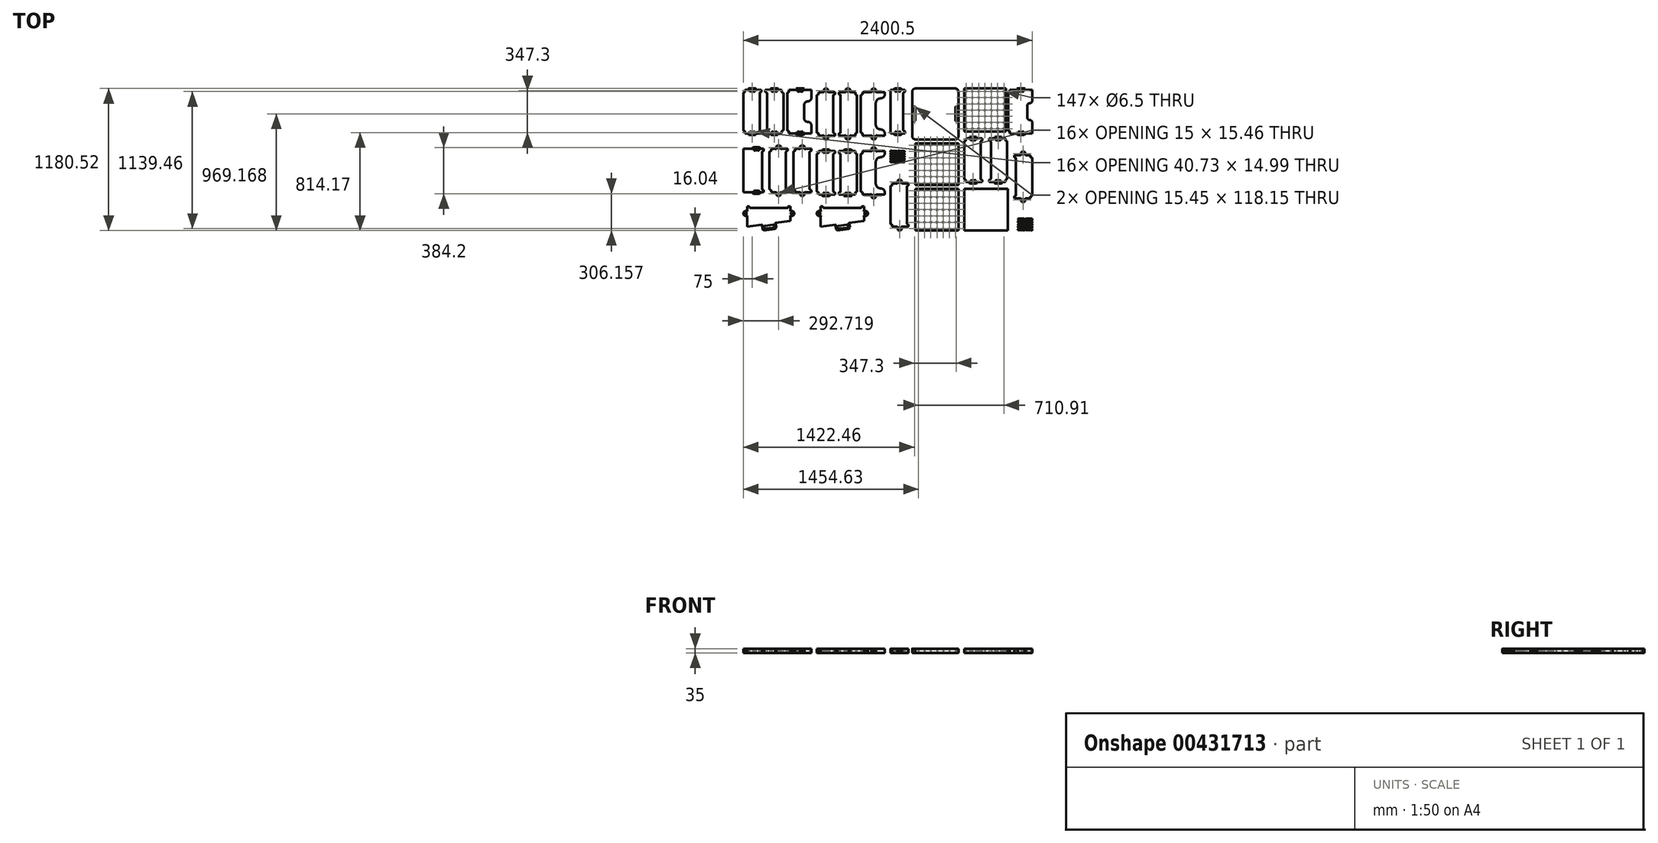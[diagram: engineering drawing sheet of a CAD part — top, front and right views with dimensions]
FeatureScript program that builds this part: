
annotation { "Feature Type Name" : "Feature", "Feature Type Description" : "" }
export const myFeature = defineFeature(function(context is Context, id is Id, definition is map)
    precondition{}
    {
        {
            var Q0;
            Q0=qCreatedBy(makeId("Top.planeOp"),FACE);
            var sketch = newSketch(context, id + "F0", { "sketchPlane" : qUnion([Q0])});
            skArc(sketch, "E0", {"start": v(1194.81, -507.13) * mm, "mid": v(1198.63, -505.83) * mm, "end": v(1200.25, -502.15) * mm});
            skLineSegment(sketch, "E1", {"start": v(1195.25, -492.72) * mm, "end": v(1150.25, -492.72) * mm});
            skArc(sketch, "E2", {"start": v(1150.25, -492.72) * mm, "mid": v(1145, -497.73) * mm, "end": v(1149.8, -503.19) * mm});
            skArc(sketch, "E3", {"start": v(1200.25, -497.72) * mm, "mid": v(1198.79, -494.18) * mm, "end": v(1195.25, -492.72) * mm});
            skLineSegment(sketch, "E4", {"start": v(1200.25, -502.15) * mm, "end": v(1200.25, -497.72) * mm});
            skLineSegment(sketch, "E5", {"start": v(1149.8, -503.19) * mm, "end": v(1194.81, -507.13) * mm});
            skArc(sketch, "E6", {"start": v(1136.95, -580.84) * mm, "mid": v(1135.49, -577.3) * mm, "end": v(1131.95, -575.84) * mm});
            skLineSegment(sketch, "E7", {"start": v(1131.95, -575.84) * mm, "end": v(1086.95, -575.84) * mm});
            skArc(sketch, "E8", {"start": v(1086.95, -575.84) * mm, "mid": v(1081.7, -580.86) * mm, "end": v(1086.5, -586.31) * mm});
            skLineSegment(sketch, "E9", {"start": v(1136.95, -585.27) * mm, "end": v(1136.95, -580.84) * mm});
            skArc(sketch, "E10", {"start": v(1131.52, -590.25) * mm, "mid": v(1135.33, -588.96) * mm, "end": v(1136.95, -585.27) * mm});
            skLineSegment(sketch, "E11", {"start": v(1086.5, -586.31) * mm, "end": v(1131.52, -590.25) * mm});
            skArc(sketch, "E12", {"start": v(91.86, -8.3) * mm, "mid": v(88.05, -9.6) * mm, "end": v(86.42, -13.28) * mm});
            skLineSegment(sketch, "E13", {"start": v(136.88, -12.24) * mm, "end": v(91.86, -8.3) * mm});
            skLineSegment(sketch, "E14", {"start": v(91.42, -22.71) * mm, "end": v(136.42, -22.71) * mm});
            skArc(sketch, "E15", {"start": v(136.42, -22.71) * mm, "mid": v(141.67, -17.7) * mm, "end": v(136.88, -12.24) * mm});
            skArc(sketch, "E16", {"start": v(86.42, -17.71) * mm, "mid": v(87.89, -21.25) * mm, "end": v(91.42, -22.71) * mm});
            skLineSegment(sketch, "E17", {"start": v(86.42, -13.28) * mm, "end": v(86.42, -17.71) * mm});
            skLineSegment(sketch, "E18", {"start": v(28.12, -22.71) * mm, "end": v(73.12, -22.71) * mm});
            skArc(sketch, "E19", {"start": v(28.56, -8.3) * mm, "mid": v(24.75, -9.6) * mm, "end": v(23.12, -13.28) * mm});
            skArc(sketch, "E20", {"start": v(23.12, -17.71) * mm, "mid": v(24.59, -21.25) * mm, "end": v(28.12, -22.71) * mm});
            skLineSegment(sketch, "E21", {"start": v(73.58, -12.24) * mm, "end": v(28.56, -8.3) * mm});
            skArc(sketch, "E22", {"start": v(73.12, -22.71) * mm, "mid": v(78.37, -17.7) * mm, "end": v(73.58, -12.24) * mm});
            skLineSegment(sketch, "E23", {"start": v(23.12, -13.28) * mm, "end": v(23.12, -17.71) * mm});
            skLineSegment(sketch, "E24", {"start": v(73.58, 8.54) * mm, "end": v(28.56, 12.48) * mm});
            skArc(sketch, "E25", {"start": v(28.56, 12.48) * mm, "mid": v(24.75, 11.19) * mm, "end": v(23.12, 7.5) * mm});
            skArc(sketch, "E26", {"start": v(73.12, -1.93) * mm, "mid": v(78.37, 3.09) * mm, "end": v(73.58, 8.54) * mm});
            skArc(sketch, "E27", {"start": v(23.12, 3.07) * mm, "mid": v(24.59, -0.47) * mm, "end": v(28.12, -1.93) * mm});
            skLineSegment(sketch, "E28", {"start": v(28.12, -1.93) * mm, "end": v(73.12, -1.93) * mm});
            skLineSegment(sketch, "E29", {"start": v(23.12, 7.5) * mm, "end": v(23.12, 3.07) * mm});
            skArc(sketch, "E30", {"start": v(91.86, 12.48) * mm, "mid": v(88.05, 11.19) * mm, "end": v(86.42, 7.5) * mm});
            skLineSegment(sketch, "E31", {"start": v(136.88, 8.54) * mm, "end": v(91.86, 12.48) * mm});
            skArc(sketch, "E32", {"start": v(136.42, -1.93) * mm, "mid": v(141.67, 3.09) * mm, "end": v(136.88, 8.54) * mm});
            skArc(sketch, "E33", {"start": v(86.42, 3.07) * mm, "mid": v(87.89, -0.47) * mm, "end": v(91.42, -1.93) * mm});
            skLineSegment(sketch, "E34", {"start": v(91.42, -1.93) * mm, "end": v(136.42, -1.93) * mm});
            skLineSegment(sketch, "E35", {"start": v(86.42, 7.5) * mm, "end": v(86.42, 3.07) * mm});
            skArc(sketch, "E36", {"start": v(136.42, 18.85) * mm, "mid": v(141.67, 23.87) * mm, "end": v(136.88, 29.32) * mm});
            skLineSegment(sketch, "E37", {"start": v(136.88, 29.32) * mm, "end": v(91.86, 33.26) * mm});
            skArc(sketch, "E38", {"start": v(91.86, 33.26) * mm, "mid": v(88.05, 31.97) * mm, "end": v(86.42, 28.28) * mm});
            skArc(sketch, "E39", {"start": v(86.42, 23.85) * mm, "mid": v(87.89, 20.31) * mm, "end": v(91.42, 18.85) * mm});
            skLineSegment(sketch, "E40", {"start": v(91.42, 18.85) * mm, "end": v(136.42, 18.85) * mm});
            skLineSegment(sketch, "E41", {"start": v(86.42, 28.28) * mm, "end": v(86.42, 23.85) * mm});
            skArc(sketch, "E42", {"start": v(28.56, 33.26) * mm, "mid": v(24.75, 31.97) * mm, "end": v(23.12, 28.28) * mm});
            skLineSegment(sketch, "E43", {"start": v(73.58, 29.32) * mm, "end": v(28.56, 33.26) * mm});
            skArc(sketch, "E44", {"start": v(73.12, 18.85) * mm, "mid": v(78.37, 23.87) * mm, "end": v(73.58, 29.32) * mm});
            skArc(sketch, "E45", {"start": v(23.12, 23.85) * mm, "mid": v(24.59, 20.31) * mm, "end": v(28.12, 18.85) * mm});
            skLineSegment(sketch, "E46", {"start": v(28.12, 18.85) * mm, "end": v(73.12, 18.85) * mm});
            skLineSegment(sketch, "E47", {"start": v(23.12, 28.28) * mm, "end": v(23.12, 23.85) * mm});
            skArc(sketch, "E48", {"start": v(23.12, 44.63) * mm, "mid": v(24.59, 41.1) * mm, "end": v(28.12, 39.63) * mm});
            skArc(sketch, "E49", {"start": v(28.56, 54.04) * mm, "mid": v(24.75, 52.75) * mm, "end": v(23.12, 49.06) * mm});
            skArc(sketch, "E50", {"start": v(73.12, 39.63) * mm, "mid": v(78.37, 44.65) * mm, "end": v(73.58, 50.1) * mm});
            skLineSegment(sketch, "E51", {"start": v(73.58, 50.1) * mm, "end": v(28.56, 54.04) * mm});
            skLineSegment(sketch, "E52", {"start": v(28.12, 39.63) * mm, "end": v(73.12, 39.63) * mm});
            skLineSegment(sketch, "E53", {"start": v(23.12, 49.06) * mm, "end": v(23.12, 44.63) * mm});
            skLineSegment(sketch, "E54", {"start": v(91.42, 39.63) * mm, "end": v(136.42, 39.63) * mm});
            skArc(sketch, "E55", {"start": v(91.86, 54.04) * mm, "mid": v(88.05, 52.75) * mm, "end": v(86.42, 49.06) * mm});
            skLineSegment(sketch, "E56", {"start": v(136.88, 50.1) * mm, "end": v(91.86, 54.04) * mm});
            skArc(sketch, "E57", {"start": v(136.42, 39.63) * mm, "mid": v(141.67, 44.65) * mm, "end": v(136.88, 50.1) * mm});
            skArc(sketch, "E58", {"start": v(86.42, 44.63) * mm, "mid": v(87.89, 41.1) * mm, "end": v(91.42, 39.63) * mm});
            skLineSegment(sketch, "E59", {"start": v(86.42, 49.06) * mm, "end": v(86.42, 44.63) * mm});
            skArc(sketch, "E60", {"start": v(136.42, 60.41) * mm, "mid": v(141.67, 65.43) * mm, "end": v(136.88, 70.88) * mm});
            skArc(sketch, "E61", {"start": v(91.86, 74.82) * mm, "mid": v(88.05, 73.53) * mm, "end": v(86.42, 69.84) * mm});
            skLineSegment(sketch, "E62", {"start": v(136.88, 70.88) * mm, "end": v(91.86, 74.82) * mm});
            skArc(sketch, "E63", {"start": v(86.42, 65.41) * mm, "mid": v(87.89, 61.88) * mm, "end": v(91.42, 60.41) * mm});
            skLineSegment(sketch, "E64", {"start": v(91.42, 60.41) * mm, "end": v(136.42, 60.41) * mm});
            skLineSegment(sketch, "E65", {"start": v(86.42, 69.84) * mm, "end": v(86.42, 65.41) * mm});
            skArc(sketch, "E66", {"start": v(28.56, 74.82) * mm, "mid": v(24.75, 73.53) * mm, "end": v(23.12, 69.84) * mm});
            skLineSegment(sketch, "E67", {"start": v(73.58, 70.88) * mm, "end": v(28.56, 74.82) * mm});
            skArc(sketch, "E68", {"start": v(73.12, 60.41) * mm, "mid": v(78.37, 65.43) * mm, "end": v(73.58, 70.88) * mm});
            skLineSegment(sketch, "E69", {"start": v(28.12, 60.41) * mm, "end": v(73.12, 60.41) * mm});
            skArc(sketch, "E70", {"start": v(23.12, 65.41) * mm, "mid": v(24.59, 61.88) * mm, "end": v(28.12, 60.41) * mm});
            skLineSegment(sketch, "E71", {"start": v(23.12, 69.84) * mm, "end": v(23.12, 65.41) * mm});
            skArc(sketch, "E72", {"start": v(1194.81, -527.9) * mm, "mid": v(1198.63, -526.61) * mm, "end": v(1200.25, -522.93) * mm});
            skLineSegment(sketch, "E73", {"start": v(1149.8, -523.97) * mm, "end": v(1194.81, -527.9) * mm});
            skArc(sketch, "E74", {"start": v(1150.25, -513.5) * mm, "mid": v(1145, -518.51) * mm, "end": v(1149.8, -523.97) * mm});
            skLineSegment(sketch, "E75", {"start": v(1195.25, -513.5) * mm, "end": v(1150.25, -513.5) * mm});
            skArc(sketch, "E76", {"start": v(1200.25, -518.5) * mm, "mid": v(1198.79, -514.96) * mm, "end": v(1195.25, -513.5) * mm});
            skLineSegment(sketch, "E77", {"start": v(1200.25, -522.93) * mm, "end": v(1200.25, -518.5) * mm});
            skArc(sketch, "E78", {"start": v(1150.25, -534.28) * mm, "mid": v(1145, -539.3) * mm, "end": v(1149.8, -544.75) * mm});
            skArc(sketch, "E79", {"start": v(1194.81, -548.69) * mm, "mid": v(1198.63, -547.4) * mm, "end": v(1200.25, -543.7) * mm});
            skLineSegment(sketch, "E80", {"start": v(1149.8, -544.75) * mm, "end": v(1194.81, -548.69) * mm});
            skLineSegment(sketch, "E81", {"start": v(1195.25, -534.28) * mm, "end": v(1150.25, -534.28) * mm});
            skArc(sketch, "E82", {"start": v(1200.25, -539.28) * mm, "mid": v(1198.79, -535.74) * mm, "end": v(1195.25, -534.28) * mm});
            skLineSegment(sketch, "E83", {"start": v(1200.25, -543.7) * mm, "end": v(1200.25, -539.28) * mm});
            skArc(sketch, "E84", {"start": v(1194.81, -569.47) * mm, "mid": v(1198.63, -568.17) * mm, "end": v(1200.25, -564.49) * mm});
            skLineSegment(sketch, "E85", {"start": v(1149.8, -565.53) * mm, "end": v(1194.81, -569.47) * mm});
            skArc(sketch, "E86", {"start": v(1150.25, -555.06) * mm, "mid": v(1145, -560.08) * mm, "end": v(1149.8, -565.53) * mm});
            skLineSegment(sketch, "E87", {"start": v(1195.25, -555.06) * mm, "end": v(1150.25, -555.06) * mm});
            skArc(sketch, "E88", {"start": v(1200.25, -560.06) * mm, "mid": v(1198.79, -556.52) * mm, "end": v(1195.25, -555.06) * mm});
            skLineSegment(sketch, "E89", {"start": v(1200.25, -564.49) * mm, "end": v(1200.25, -560.06) * mm});
            skArc(sketch, "E90", {"start": v(1150.25, -575.84) * mm, "mid": v(1145, -580.86) * mm, "end": v(1149.8, -586.31) * mm});
            skArc(sketch, "E91", {"start": v(1194.81, -590.25) * mm, "mid": v(1198.63, -588.96) * mm, "end": v(1200.25, -585.27) * mm});
            skLineSegment(sketch, "E92", {"start": v(1149.8, -586.31) * mm, "end": v(1194.81, -590.25) * mm});
            skLineSegment(sketch, "E93", {"start": v(1195.25, -575.84) * mm, "end": v(1150.25, -575.84) * mm});
            skArc(sketch, "E94", {"start": v(1200.25, -580.84) * mm, "mid": v(1198.79, -577.3) * mm, "end": v(1195.25, -575.84) * mm});
            skLineSegment(sketch, "E95", {"start": v(1200.25, -585.27) * mm, "end": v(1200.25, -580.84) * mm});
            skArc(sketch, "E96", {"start": v(1131.52, -569.47) * mm, "mid": v(1135.33, -568.17) * mm, "end": v(1136.95, -564.49) * mm});
            skLineSegment(sketch, "E97", {"start": v(1086.5, -565.53) * mm, "end": v(1131.52, -569.47) * mm});
            skLineSegment(sketch, "E98", {"start": v(1131.95, -555.06) * mm, "end": v(1086.95, -555.06) * mm});
            skArc(sketch, "E99", {"start": v(1086.95, -555.06) * mm, "mid": v(1081.7, -560.08) * mm, "end": v(1086.5, -565.53) * mm});
            skArc(sketch, "E100", {"start": v(1136.95, -560.06) * mm, "mid": v(1135.49, -556.52) * mm, "end": v(1131.95, -555.06) * mm});
            skLineSegment(sketch, "E101", {"start": v(1136.95, -564.49) * mm, "end": v(1136.95, -560.06) * mm});
            skArc(sketch, "E102", {"start": v(1131.52, -548.69) * mm, "mid": v(1135.33, -547.4) * mm, "end": v(1136.95, -543.7) * mm});
            skLineSegment(sketch, "E103", {"start": v(1086.5, -544.75) * mm, "end": v(1131.52, -548.69) * mm});
            skArc(sketch, "E104", {"start": v(1086.95, -534.28) * mm, "mid": v(1081.7, -539.3) * mm, "end": v(1086.5, -544.75) * mm});
            skLineSegment(sketch, "E105", {"start": v(1131.95, -534.28) * mm, "end": v(1086.95, -534.28) * mm});
            skArc(sketch, "E106", {"start": v(1136.95, -539.28) * mm, "mid": v(1135.49, -535.74) * mm, "end": v(1131.95, -534.28) * mm});
            skLineSegment(sketch, "E107", {"start": v(1136.95, -543.7) * mm, "end": v(1136.95, -539.28) * mm});
            skArc(sketch, "E108", {"start": v(1131.52, -527.9) * mm, "mid": v(1135.33, -526.61) * mm, "end": v(1136.95, -522.93) * mm});
            skLineSegment(sketch, "E109", {"start": v(1086.5, -523.97) * mm, "end": v(1131.52, -527.9) * mm});
            skArc(sketch, "E110", {"start": v(1086.95, -513.5) * mm, "mid": v(1081.7, -518.51) * mm, "end": v(1086.5, -523.97) * mm});
            skArc(sketch, "E111", {"start": v(1136.95, -518.5) * mm, "mid": v(1135.49, -514.96) * mm, "end": v(1131.95, -513.5) * mm});
            skLineSegment(sketch, "E112", {"start": v(1131.95, -513.5) * mm, "end": v(1086.95, -513.5) * mm});
            skLineSegment(sketch, "E113", {"start": v(1136.95, -522.93) * mm, "end": v(1136.95, -518.5) * mm});
            skLineSegment(sketch, "E114", {"start": v(1131.95, -492.72) * mm, "end": v(1086.95, -492.72) * mm});
            skArc(sketch, "E115", {"start": v(1131.52, -507.13) * mm, "mid": v(1135.33, -505.83) * mm, "end": v(1136.95, -502.15) * mm});
            skLineSegment(sketch, "E116", {"start": v(1086.5, -503.19) * mm, "end": v(1131.52, -507.13) * mm});
            skArc(sketch, "E117", {"start": v(1086.95, -492.72) * mm, "mid": v(1081.7, -497.73) * mm, "end": v(1086.5, -503.19) * mm});
            skArc(sketch, "E118", {"start": v(1136.95, -497.72) * mm, "mid": v(1135.49, -494.18) * mm, "end": v(1131.95, -492.72) * mm});
            skLineSegment(sketch, "E119", {"start": v(1136.95, -502.15) * mm, "end": v(1136.95, -497.72) * mm});
            skCircle(sketch, "E120", {"center": v(860.47, 462.18) * mm, "radius": 3.25 * mm});
            skCircle(sketch, "E121", {"center": v(860.47, 565.23) * mm, "radius": 3.25 * mm});
            skLineSegment(sketch, "E122", {"start": v(634.81, 231.05) * mm, "end": v(981.31, 231.05) * mm});
            skCircle(sketch, "E123", {"center": v(965.3, 462.18) * mm, "radius": 3.25 * mm});
            skCircle(sketch, "E124", {"center": v(965.3, 410.65) * mm, "radius": 3.25 * mm});
            skCircle(sketch, "E125", {"center": v(965.3, 513.7) * mm, "radius": 3.25 * mm});
            skCircle(sketch, "E126", {"center": v(965.3, 307.6) * mm, "radius": 3.25 * mm});
            skCircle(sketch, "E127", {"center": v(912.88, 462.18) * mm, "radius": 3.25 * mm});
            skCircle(sketch, "E128", {"center": v(860.47, 513.7) * mm, "radius": 3.25 * mm});
            skCircle(sketch, "E129", {"center": v(912.88, 513.7) * mm, "radius": 3.25 * mm});
            skCircle(sketch, "E130", {"center": v(912.88, 565.23) * mm, "radius": 3.25 * mm});
            skCircle(sketch, "E131", {"center": v(965.3, 565.23) * mm, "radius": 3.25 * mm});
            skCircle(sketch, "E132", {"center": v(965.3, 359.12) * mm, "radius": 3.25 * mm});
            skCircle(sketch, "E133", {"center": v(860.47, 410.65) * mm, "radius": 3.25 * mm});
            skCircle(sketch, "E134", {"center": v(912.88, 410.65) * mm, "radius": 3.25 * mm});
            skCircle(sketch, "E135", {"center": v(860.47, 359.12) * mm, "radius": 3.25 * mm});
            skCircle(sketch, "E136", {"center": v(912.88, 359.12) * mm, "radius": 3.25 * mm});
            skCircle(sketch, "E137", {"center": v(755.65, 462.18) * mm, "radius": 3.25 * mm});
            skCircle(sketch, "E138", {"center": v(860.47, 307.6) * mm, "radius": 3.25 * mm});
            skCircle(sketch, "E139", {"center": v(912.88, 307.6) * mm, "radius": 3.25 * mm});
            skCircle(sketch, "E140", {"center": v(860.47, 256.07) * mm, "radius": 3.25 * mm});
            skCircle(sketch, "E141", {"center": v(912.88, 256.07) * mm, "radius": 3.25 * mm});
            skCircle(sketch, "E142", {"center": v(965.3, 256.07) * mm, "radius": 3.25 * mm});
            skCircle(sketch, "E143", {"center": v(755.65, 513.7) * mm, "radius": 3.25 * mm});
            skCircle(sketch, "E144", {"center": v(650.83, 462.18) * mm, "radius": 3.25 * mm});
            skCircle(sketch, "E145", {"center": v(650.83, 513.7) * mm, "radius": 3.25 * mm});
            skCircle(sketch, "E146", {"center": v(808.06, 462.18) * mm, "radius": 3.25 * mm});
            skCircle(sketch, "E147", {"center": v(755.65, 359.12) * mm, "radius": 3.25 * mm});
            skCircle(sketch, "E148", {"center": v(703.24, 462.18) * mm, "radius": 3.25 * mm});
            skCircle(sketch, "E149", {"center": v(808.06, 513.7) * mm, "radius": 3.25 * mm});
            skCircle(sketch, "E150", {"center": v(703.24, 513.7) * mm, "radius": 3.25 * mm});
            skCircle(sketch, "E151", {"center": v(808.06, 565.23) * mm, "radius": 3.25 * mm});
            skCircle(sketch, "E152", {"center": v(755.65, 565.23) * mm, "radius": 3.25 * mm});
            skCircle(sketch, "E153", {"center": v(703.24, 565.23) * mm, "radius": 3.25 * mm});
            skCircle(sketch, "E154", {"center": v(703.24, 359.12) * mm, "radius": 3.25 * mm});
            skCircle(sketch, "E155", {"center": v(650.83, 565.23) * mm, "radius": 3.25 * mm});
            skCircle(sketch, "E156", {"center": v(650.83, 410.65) * mm, "radius": 3.25 * mm});
            skCircle(sketch, "E157", {"center": v(650.83, 359.12) * mm, "radius": 3.25 * mm});
            skCircle(sketch, "E158", {"center": v(650.83, 307.6) * mm, "radius": 3.25 * mm});
            skCircle(sketch, "E159", {"center": v(808.06, 410.65) * mm, "radius": 3.25 * mm});
            skCircle(sketch, "E160", {"center": v(755.65, 410.65) * mm, "radius": 3.25 * mm});
            skCircle(sketch, "E161", {"center": v(703.24, 410.65) * mm, "radius": 3.25 * mm});
            skCircle(sketch, "E162", {"center": v(808.06, 359.12) * mm, "radius": 3.25 * mm});
            skCircle(sketch, "E163", {"center": v(808.06, 307.6) * mm, "radius": 3.25 * mm});
            skLineSegment(sketch, "E164", {"start": v(634.81, 590.25) * mm, "end": v(981.31, 590.25) * mm});
            skCircle(sketch, "E165", {"center": v(755.65, 307.6) * mm, "radius": 3.25 * mm});
            skCircle(sketch, "E166", {"center": v(703.24, 307.6) * mm, "radius": 3.25 * mm});
            skCircle(sketch, "E167", {"center": v(808.06, 256.07) * mm, "radius": 3.25 * mm});
            skCircle(sketch, "E168", {"center": v(755.65, 256.07) * mm, "radius": 3.25 * mm});
            skCircle(sketch, "E169", {"center": v(703.24, 256.07) * mm, "radius": 3.25 * mm});
            skCircle(sketch, "E170", {"center": v(650.83, 256.07) * mm, "radius": 3.25 * mm});
            skLineSegment(sketch, "E171", {"start": v(634.81, 590.25) * mm, "end": v(634.81, 231.05) * mm});
            skLineSegment(sketch, "E172", {"start": v(981.31, 590.25) * mm, "end": v(981.31, 231.05) * mm});
            skArc(sketch, "E173", {"start": v(1092.97, 217.38) * mm, "mid": v(1092.64, 217.32) * mm, "end": v(1092.34, 217.15) * mm});
            skArc(sketch, "E174", {"start": v(1087.86, 572.6) * mm, "mid": v(1087.8, 572.94) * mm, "end": v(1087.63, 573.24) * mm});
            skArc(sketch, "E175", {"start": v(1122.16, 564.45) * mm, "mid": v(1126.64, 564.68) * mm, "end": v(1126.87, 569.16) * mm});
            skLineSegment(sketch, "E176", {"start": v(1014.25, 564.45) * mm, "end": v(1014.25, 577.55) * mm});
            skArc(sketch, "E177", {"start": v(1087.63, 569.16) * mm, "mid": v(1087.8, 569.46) * mm, "end": v(1087.86, 569.8) * mm});
            skLineSegment(sketch, "E178", {"start": v(1087.86, 569.8) * mm, "end": v(1087.86, 572.6) * mm});
            skArc(sketch, "E179", {"start": v(1087.63, 569.16) * mm, "mid": v(1087.86, 564.68) * mm, "end": v(1092.34, 564.45) * mm});
            skArc(sketch, "E180", {"start": v(1092.97, 564.68) * mm, "mid": v(1092.64, 564.62) * mm, "end": v(1092.34, 564.45) * mm});
            skArc(sketch, "E181", {"start": v(1200.25, 307.55) * mm, "mid": v(1194.4, 321.7) * mm, "end": v(1180.25, 327.55) * mm});
            skArc(sketch, "E182", {"start": v(1122.16, 564.45) * mm, "mid": v(1121.86, 564.62) * mm, "end": v(1121.53, 564.68) * mm});
            skLineSegment(sketch, "E183", {"start": v(1121.53, 564.68) * mm, "end": v(1092.97, 564.68) * mm});
            skArc(sketch, "E184", {"start": v(1126.64, 569.8) * mm, "mid": v(1126.7, 569.46) * mm, "end": v(1126.87, 569.16) * mm});
            skLineSegment(sketch, "E185", {"start": v(1126.64, 572.6) * mm, "end": v(1126.64, 569.8) * mm});
            skArc(sketch, "E186", {"start": v(1126.87, 573.24) * mm, "mid": v(1126.7, 572.94) * mm, "end": v(1126.64, 572.6) * mm});
            skArc(sketch, "E187", {"start": v(1126.87, 573.24) * mm, "mid": v(1126.64, 577.72) * mm, "end": v(1122.16, 577.95) * mm});
            skArc(sketch, "E188", {"start": v(1121.53, 577.72) * mm, "mid": v(1121.86, 577.78) * mm, "end": v(1122.16, 577.95) * mm});
            skArc(sketch, "E189", {"start": v(1075.16, 582.66) * mm, "mid": v(1075.22, 582.33) * mm, "end": v(1075.39, 582.03) * mm});
            skLineSegment(sketch, "E190", {"start": v(1092.97, 577.72) * mm, "end": v(1121.53, 577.72) * mm});
            skArc(sketch, "E191", {"start": v(1092.34, 577.95) * mm, "mid": v(1092.64, 577.78) * mm, "end": v(1092.97, 577.72) * mm});
            skArc(sketch, "E192", {"start": v(1092.34, 577.95) * mm, "mid": v(1087.86, 577.72) * mm, "end": v(1087.63, 573.24) * mm});
            skLineSegment(sketch, "E193", {"start": v(1014.25, 577.55) * mm, "end": v(1070.05, 577.55) * mm});
            skArc(sketch, "E194", {"start": v(1070.68, 577.32) * mm, "mid": v(1070.38, 577.5) * mm, "end": v(1070.05, 577.55) * mm});
            skArc(sketch, "E195", {"start": v(1070.68, 577.32) * mm, "mid": v(1075.16, 577.55) * mm, "end": v(1075.39, 582.03) * mm});
            skArc(sketch, "E196", {"start": v(1180.25, 467.55) * mm, "mid": v(1194.4, 473.4) * mm, "end": v(1200.25, 487.55) * mm});
            skLineSegment(sketch, "E197", {"start": v(1075.16, 582.66) * mm, "end": v(1075.16, 586.46) * mm});
            skLineSegment(sketch, "E198", {"start": v(1075.16, 586.46) * mm, "end": v(1078.95, 590.25) * mm});
            skArc(sketch, "E199", {"start": v(1180.25, 467.55) * mm, "mid": v(1166.1, 461.7) * mm, "end": v(1160.25, 447.55) * mm});
            skLineSegment(sketch, "E200", {"start": v(1078.95, 590.25) * mm, "end": v(1135.55, 590.25) * mm});
            skLineSegment(sketch, "E201", {"start": v(1135.55, 590.25) * mm, "end": v(1139.34, 586.46) * mm});
            skLineSegment(sketch, "E202", {"start": v(1139.34, 586.46) * mm, "end": v(1139.34, 582.66) * mm});
            skArc(sketch, "E203", {"start": v(1139.11, 582.03) * mm, "mid": v(1139.28, 582.33) * mm, "end": v(1139.34, 582.66) * mm});
            skArc(sketch, "E204", {"start": v(1139.11, 582.03) * mm, "mid": v(1139.34, 577.55) * mm, "end": v(1143.82, 577.32) * mm});
            skArc(sketch, "E205", {"start": v(1144.45, 577.55) * mm, "mid": v(1144.12, 577.5) * mm, "end": v(1143.82, 577.32) * mm});
            skLineSegment(sketch, "E206", {"start": v(1144.45, 577.55) * mm, "end": v(1200.25, 577.55) * mm});
            skArc(sketch, "E207", {"start": v(1143.82, 217.78) * mm, "mid": v(1144.12, 217.6) * mm, "end": v(1144.45, 217.55) * mm});
            skLineSegment(sketch, "E208", {"start": v(1200.25, 577.55) * mm, "end": v(1200.25, 487.55) * mm});
            skLineSegment(sketch, "E209", {"start": v(1160.25, 347.55) * mm, "end": v(1160.25, 447.55) * mm});
            skArc(sketch, "E210", {"start": v(1160.25, 347.55) * mm, "mid": v(1166.1, 333.4) * mm, "end": v(1180.25, 327.55) * mm});
            skLineSegment(sketch, "E211", {"start": v(1200.25, 217.55) * mm, "end": v(1200.25, 307.55) * mm});
            skLineSegment(sketch, "E212", {"start": v(1144.45, 217.55) * mm, "end": v(1200.25, 217.55) * mm});
            skArc(sketch, "E213", {"start": v(1143.82, 217.78) * mm, "mid": v(1139.34, 217.55) * mm, "end": v(1139.11, 213.07) * mm});
            skLineSegment(sketch, "E214", {"start": v(1139.34, 208.64) * mm, "end": v(1139.34, 212.44) * mm});
            skArc(sketch, "E215", {"start": v(1139.34, 212.44) * mm, "mid": v(1139.28, 212.77) * mm, "end": v(1139.11, 213.07) * mm});
            skLineSegment(sketch, "E216", {"start": v(1135.55, 204.85) * mm, "end": v(1139.34, 208.64) * mm});
            skLineSegment(sketch, "E217", {"start": v(1078.95, 204.85) * mm, "end": v(1135.55, 204.85) * mm});
            skLineSegment(sketch, "E218", {"start": v(1075.16, 208.64) * mm, "end": v(1078.95, 204.85) * mm});
            skLineSegment(sketch, "E219", {"start": v(1075.16, 212.44) * mm, "end": v(1075.16, 208.64) * mm});
            skArc(sketch, "E220", {"start": v(1075.39, 213.07) * mm, "mid": v(1075.22, 212.77) * mm, "end": v(1075.16, 212.44) * mm});
            skArc(sketch, "E221", {"start": v(1075.39, 213.07) * mm, "mid": v(1075.16, 217.55) * mm, "end": v(1070.68, 217.78) * mm});
            skArc(sketch, "E222", {"start": v(1070.05, 217.55) * mm, "mid": v(1070.38, 217.6) * mm, "end": v(1070.68, 217.78) * mm});
            skLineSegment(sketch, "E223", {"start": v(1014.25, 217.55) * mm, "end": v(1070.05, 217.55) * mm});
            skLineSegment(sketch, "E224", {"start": v(1014.25, 230.65) * mm, "end": v(1014.25, 217.55) * mm});
            skArc(sketch, "E225", {"start": v(1014.25, 230.65) * mm, "mid": v(1012.2, 235.6) * mm, "end": v(1007.25, 237.65) * mm});
            skArc(sketch, "E226", {"start": v(1000.25, 244.65) * mm, "mid": v(1002.3, 239.7) * mm, "end": v(1007.25, 237.65) * mm});
            skLineSegment(sketch, "E227", {"start": v(1000.25, 550.45) * mm, "end": v(1000.25, 244.65) * mm});
            skLineSegment(sketch, "E228", {"start": v(1126.64, 222.5) * mm, "end": v(1126.64, 225.3) * mm});
            skArc(sketch, "E229", {"start": v(1007.25, 557.45) * mm, "mid": v(1002.3, 555.4) * mm, "end": v(1000.25, 550.45) * mm});
            skArc(sketch, "E230", {"start": v(1087.86, 225.3) * mm, "mid": v(1087.8, 225.64) * mm, "end": v(1087.63, 225.94) * mm});
            skArc(sketch, "E231", {"start": v(1007.25, 557.45) * mm, "mid": v(1012.2, 559.5) * mm, "end": v(1014.25, 564.45) * mm});
            skArc(sketch, "E232", {"start": v(1122.16, 217.15) * mm, "mid": v(1121.86, 217.32) * mm, "end": v(1121.53, 217.38) * mm});
            skLineSegment(sketch, "E233", {"start": v(1092.97, 217.38) * mm, "end": v(1121.53, 217.38) * mm});
            skArc(sketch, "E234", {"start": v(1122.16, 217.15) * mm, "mid": v(1126.64, 217.38) * mm, "end": v(1126.87, 221.86) * mm});
            skArc(sketch, "E235", {"start": v(1126.64, 222.5) * mm, "mid": v(1126.7, 222.16) * mm, "end": v(1126.87, 221.86) * mm});
            skArc(sketch, "E236", {"start": v(1126.87, 225.94) * mm, "mid": v(1126.7, 225.64) * mm, "end": v(1126.64, 225.3) * mm});
            skArc(sketch, "E237", {"start": v(1126.87, 225.94) * mm, "mid": v(1126.64, 230.42) * mm, "end": v(1122.16, 230.65) * mm});
            skArc(sketch, "E238", {"start": v(1121.53, 230.42) * mm, "mid": v(1121.86, 230.48) * mm, "end": v(1122.16, 230.65) * mm});
            skLineSegment(sketch, "E239", {"start": v(1121.53, 230.42) * mm, "end": v(1092.97, 230.42) * mm});
            skArc(sketch, "E240", {"start": v(1092.34, 230.65) * mm, "mid": v(1092.64, 230.48) * mm, "end": v(1092.97, 230.42) * mm});
            skArc(sketch, "E241", {"start": v(1092.34, 230.65) * mm, "mid": v(1087.86, 230.42) * mm, "end": v(1087.63, 225.94) * mm});
            skArc(sketch, "E242", {"start": v(1087.63, 221.86) * mm, "mid": v(1087.86, 217.38) * mm, "end": v(1092.34, 217.15) * mm});
            skLineSegment(sketch, "E243", {"start": v(1087.86, 225.3) * mm, "end": v(1087.86, 222.5) * mm});
            skArc(sketch, "E244", {"start": v(1087.63, 221.86) * mm, "mid": v(1087.8, 222.16) * mm, "end": v(1087.86, 222.5) * mm});
            skArc(sketch, "E245", {"start": v(1149.1, -323.83) * mm, "mid": v(1144.47, -323.93) * mm, "end": v(1144.37, -328.55) * mm});
            skLineSegment(sketch, "E246", {"start": v(1186.25, -310.83) * mm, "end": v(1186.25, -323.93) * mm});
            skArc(sketch, "E247", {"start": v(1131.77, -337.9) * mm, "mid": v(1131.8, -338.04) * mm, "end": v(1131.87, -338.16) * mm});
            skArc(sketch, "E248", {"start": v(1123.35, 55.02) * mm, "mid": v(1123.48, 54.94) * mm, "end": v(1123.62, 54.92) * mm});
            skArc(sketch, "E249", {"start": v(1149.1, -323.83) * mm, "mid": v(1149.22, -323.9) * mm, "end": v(1149.36, -323.93) * mm});
            skLineSegment(sketch, "E250", {"start": v(1186.25, -323.93) * mm, "end": v(1149.36, -323.93) * mm});
            skArc(sketch, "E251", {"start": v(1106.13, -328.55) * mm, "mid": v(1106.03, -323.93) * mm, "end": v(1101.4, -323.83) * mm});
            skArc(sketch, "E252", {"start": v(1144.47, -328.82) * mm, "mid": v(1144.44, -328.68) * mm, "end": v(1144.37, -328.55) * mm});
            skLineSegment(sketch, "E253", {"start": v(1144.47, -343.24) * mm, "end": v(1132.23, -355.48) * mm});
            skLineSegment(sketch, "E254", {"start": v(1144.47, -328.82) * mm, "end": v(1144.47, -343.24) * mm});
            skLineSegment(sketch, "E255", {"start": v(1132.23, -355.48) * mm, "end": v(1118.27, -355.48) * mm});
            skLineSegment(sketch, "E256", {"start": v(1118.27, -355.48) * mm, "end": v(1106.03, -343.24) * mm});
            skLineSegment(sketch, "E257", {"start": v(1106.03, -343.24) * mm, "end": v(1106.03, -328.82) * mm});
            skArc(sketch, "E258", {"start": v(1106.13, -328.55) * mm, "mid": v(1106.06, -328.68) * mm, "end": v(1106.03, -328.82) * mm});
            skArc(sketch, "E259", {"start": v(1050.25, 23.37) * mm, "mid": v(1052.3, 18.42) * mm, "end": v(1057.25, 16.37) * mm});
            skArc(sketch, "E260", {"start": v(1101.14, -323.93) * mm, "mid": v(1101.28, -323.9) * mm, "end": v(1101.4, -323.83) * mm});
            skLineSegment(sketch, "E261", {"start": v(1101.14, -323.93) * mm, "end": v(1050.25, -323.93) * mm});
            skLineSegment(sketch, "E262", {"start": v(1050.25, -323.93) * mm, "end": v(1050.25, -311.23) * mm});
            skArc(sketch, "E263", {"start": v(1057.25, -304.23) * mm, "mid": v(1052.3, -306.28) * mm, "end": v(1050.25, -311.23) * mm});
            skArc(sketch, "E264", {"start": v(1057.25, -304.23) * mm, "mid": v(1062.2, -302.18) * mm, "end": v(1064.25, -297.23) * mm});
            skArc(sketch, "E265", {"start": v(1101.4, 35.96) * mm, "mid": v(1106.03, 36.07) * mm, "end": v(1106.13, 40.69) * mm});
            skLineSegment(sketch, "E266", {"start": v(1064.25, 9.37) * mm, "end": v(1064.25, -297.23) * mm});
            skArc(sketch, "E267", {"start": v(1064.25, 9.37) * mm, "mid": v(1062.2, 14.32) * mm, "end": v(1057.25, 16.37) * mm});
            skLineSegment(sketch, "E268", {"start": v(1050.25, 36.07) * mm, "end": v(1050.25, 23.37) * mm});
            skArc(sketch, "E269", {"start": v(1101.4, 35.96) * mm, "mid": v(1101.28, 36.04) * mm, "end": v(1101.14, 36.07) * mm});
            skLineSegment(sketch, "E270", {"start": v(1101.14, 36.07) * mm, "end": v(1050.25, 36.07) * mm});
            skArc(sketch, "E271", {"start": v(1106.03, 40.96) * mm, "mid": v(1106.06, 40.81) * mm, "end": v(1106.13, 40.69) * mm});
            skArc(sketch, "E272", {"start": v(1127.15, 41.31) * mm, "mid": v(1127.02, 41.4) * mm, "end": v(1126.88, 41.42) * mm});
            skLineSegment(sketch, "E273", {"start": v(1106.03, 55.38) * mm, "end": v(1106.03, 40.96) * mm});
            skLineSegment(sketch, "E274", {"start": v(1118.27, 67.62) * mm, "end": v(1106.03, 55.38) * mm});
            skLineSegment(sketch, "E275", {"start": v(1132.23, 67.62) * mm, "end": v(1118.27, 67.62) * mm});
            skArc(sketch, "E276", {"start": v(1186.25, 22.97) * mm, "mid": v(1188.3, 18.02) * mm, "end": v(1193.25, 15.97) * mm});
            skLineSegment(sketch, "E277", {"start": v(1144.47, 55.38) * mm, "end": v(1132.23, 67.62) * mm});
            skArc(sketch, "E278", {"start": v(1123.62, 41.42) * mm, "mid": v(1123.48, 41.4) * mm, "end": v(1123.35, 41.31) * mm});
            skLineSegment(sketch, "E279", {"start": v(1144.47, 40.96) * mm, "end": v(1144.47, 55.38) * mm});
            skArc(sketch, "E280", {"start": v(1144.37, 40.69) * mm, "mid": v(1144.44, 40.81) * mm, "end": v(1144.47, 40.96) * mm});
            skArc(sketch, "E281", {"start": v(1144.37, 40.69) * mm, "mid": v(1144.47, 36.07) * mm, "end": v(1149.1, 35.96) * mm});
            skArc(sketch, "E282", {"start": v(1149.36, 36.07) * mm, "mid": v(1149.22, 36.04) * mm, "end": v(1149.1, 35.96) * mm});
            skLineSegment(sketch, "E283", {"start": v(1186.25, 36.07) * mm, "end": v(1149.36, 36.07) * mm});
            skLineSegment(sketch, "E284", {"start": v(1186.25, 22.97) * mm, "end": v(1186.25, 36.07) * mm});
            skArc(sketch, "E285", {"start": v(1200.25, 8.97) * mm, "mid": v(1198.2, 13.92) * mm, "end": v(1193.25, 15.97) * mm});
            skLineSegment(sketch, "E286", {"start": v(1200.25, -296.83) * mm, "end": v(1200.25, 8.97) * mm});
            skArc(sketch, "E287", {"start": v(1193.25, -303.83) * mm, "mid": v(1198.2, -301.78) * mm, "end": v(1200.25, -296.83) * mm});
            skArc(sketch, "E288", {"start": v(1193.25, -303.83) * mm, "mid": v(1188.3, -305.88) * mm, "end": v(1186.25, -310.83) * mm});
            skArc(sketch, "E289", {"start": v(1123.35, 55.02) * mm, "mid": v(1118.73, 54.92) * mm, "end": v(1118.63, 50.3) * mm});
            skArc(sketch, "E290", {"start": v(1118.73, 50.03) * mm, "mid": v(1118.7, 50.17) * mm, "end": v(1118.63, 50.3) * mm});
            skLineSegment(sketch, "E291", {"start": v(1118.73, 50.03) * mm, "end": v(1118.73, 46.3) * mm});
            skArc(sketch, "E292", {"start": v(1118.63, 46.04) * mm, "mid": v(1118.7, 46.16) * mm, "end": v(1118.73, 46.3) * mm});
            skArc(sketch, "E293", {"start": v(1118.63, 46.04) * mm, "mid": v(1118.73, 41.42) * mm, "end": v(1123.35, 41.31) * mm});
            skArc(sketch, "E294", {"start": v(1131.87, 50.3) * mm, "mid": v(1131.8, 50.17) * mm, "end": v(1131.77, 50.03) * mm});
            skLineSegment(sketch, "E295", {"start": v(1123.62, 41.42) * mm, "end": v(1126.88, 41.42) * mm});
            skArc(sketch, "E296", {"start": v(1127.15, 41.31) * mm, "mid": v(1131.77, 41.42) * mm, "end": v(1131.87, 46.04) * mm});
            skArc(sketch, "E297", {"start": v(1131.77, 46.3) * mm, "mid": v(1131.8, 46.16) * mm, "end": v(1131.87, 46.04) * mm});
            skArc(sketch, "E298", {"start": v(1118.73, -334.17) * mm, "mid": v(1118.7, -334.03) * mm, "end": v(1118.63, -333.9) * mm});
            skLineSegment(sketch, "E299", {"start": v(1131.77, 46.3) * mm, "end": v(1131.77, 50.03) * mm});
            skArc(sketch, "E300", {"start": v(1131.87, 50.3) * mm, "mid": v(1131.77, 54.92) * mm, "end": v(1127.15, 55.02) * mm});
            skArc(sketch, "E301", {"start": v(1126.88, 54.92) * mm, "mid": v(1127.02, 54.94) * mm, "end": v(1127.15, 55.02) * mm});
            skArc(sketch, "E302", {"start": v(1123.35, -329.18) * mm, "mid": v(1118.73, -329.28) * mm, "end": v(1118.63, -333.9) * mm});
            skLineSegment(sketch, "E303", {"start": v(1126.88, 54.92) * mm, "end": v(1123.62, 54.92) * mm});
            skLineSegment(sketch, "E304", {"start": v(1131.77, -334.17) * mm, "end": v(1131.77, -337.9) * mm});
            skArc(sketch, "E305", {"start": v(1131.87, -333.9) * mm, "mid": v(1131.8, -334.03) * mm, "end": v(1131.77, -334.17) * mm});
            skArc(sketch, "E306", {"start": v(1131.87, -333.9) * mm, "mid": v(1131.77, -329.28) * mm, "end": v(1127.15, -329.18) * mm});
            skArc(sketch, "E307", {"start": v(1126.88, -329.28) * mm, "mid": v(1127.02, -329.26) * mm, "end": v(1127.15, -329.18) * mm});
            skArc(sketch, "E308", {"start": v(1123.62, -342.78) * mm, "mid": v(1123.48, -342.8) * mm, "end": v(1123.35, -342.89) * mm});
            skLineSegment(sketch, "E309", {"start": v(1123.62, -329.28) * mm, "end": v(1126.88, -329.28) * mm});
            skArc(sketch, "E310", {"start": v(1123.35, -329.18) * mm, "mid": v(1123.48, -329.26) * mm, "end": v(1123.62, -329.28) * mm});
            skArc(sketch, "E311", {"start": v(1127.15, -342.89) * mm, "mid": v(1127.02, -342.8) * mm, "end": v(1126.88, -342.78) * mm});
            skLineSegment(sketch, "E312", {"start": v(1118.73, -337.9) * mm, "end": v(1118.73, -334.17) * mm});
            skArc(sketch, "E313", {"start": v(1118.63, -338.16) * mm, "mid": v(1118.73, -342.78) * mm, "end": v(1123.35, -342.89) * mm});
            skArc(sketch, "E314", {"start": v(1118.63, -338.16) * mm, "mid": v(1118.7, -338.04) * mm, "end": v(1118.73, -337.9) * mm});
            skLineSegment(sketch, "E315", {"start": v(1126.88, -342.78) * mm, "end": v(1123.62, -342.78) * mm});
            skArc(sketch, "E316", {"start": v(1127.15, -342.89) * mm, "mid": v(1131.77, -342.78) * mm, "end": v(1131.87, -338.16) * mm});
            skArc(sketch, "E317", {"start": v(931.8, 173.82) * mm, "mid": v(932.14, 173.88) * mm, "end": v(932.44, 174.05) * mm});
            skArc(sketch, "E318", {"start": v(936.92, -181.4) * mm, "mid": v(936.98, -181.74) * mm, "end": v(937.15, -182.04) * mm});
            skLineSegment(sketch, "E319", {"start": v(978.53, -173.25) * mm, "end": v(978.53, -186.35) * mm});
            skArc(sketch, "E320", {"start": v(937.15, -177.96) * mm, "mid": v(936.98, -178.26) * mm, "end": v(936.92, -178.6) * mm});
            skLineSegment(sketch, "E321", {"start": v(936.92, -178.6) * mm, "end": v(936.92, -181.4) * mm});
            skArc(sketch, "E322", {"start": v(937.15, -177.96) * mm, "mid": v(936.92, -173.48) * mm, "end": v(932.44, -173.25) * mm});
            skArc(sketch, "E323", {"start": v(903.25, -186.52) * mm, "mid": v(902.92, -186.58) * mm, "end": v(902.62, -186.75) * mm});
            skArc(sketch, "E324", {"start": v(931.8, -173.48) * mm, "mid": v(932.14, -173.42) * mm, "end": v(932.44, -173.25) * mm});
            skArc(sketch, "E325", {"start": v(932.44, -186.75) * mm, "mid": v(932.14, -186.58) * mm, "end": v(931.8, -186.52) * mm});
            skLineSegment(sketch, "E326", {"start": v(903.25, -173.48) * mm, "end": v(931.8, -173.48) * mm});
            skArc(sketch, "E327", {"start": v(902.62, -173.25) * mm, "mid": v(902.92, -173.42) * mm, "end": v(903.25, -173.48) * mm});
            skArc(sketch, "E328", {"start": v(902.62, -173.25) * mm, "mid": v(898.14, -173.48) * mm, "end": v(897.92, -177.96) * mm});
            skArc(sketch, "E329", {"start": v(898.14, -178.6) * mm, "mid": v(898.08, -178.26) * mm, "end": v(897.92, -177.96) * mm});
            skLineSegment(sketch, "E330", {"start": v(978.53, -186.35) * mm, "end": v(954.73, -186.35) * mm});
            skLineSegment(sketch, "E331", {"start": v(898.14, -181.4) * mm, "end": v(898.14, -178.6) * mm});
            skArc(sketch, "E332", {"start": v(897.92, -182.04) * mm, "mid": v(898.08, -181.74) * mm, "end": v(898.14, -181.4) * mm});
            skArc(sketch, "E333", {"start": v(897.92, -182.04) * mm, "mid": v(898.14, -186.52) * mm, "end": v(902.62, -186.75) * mm});
            skLineSegment(sketch, "E334", {"start": v(931.8, -186.52) * mm, "end": v(903.25, -186.52) * mm});
            skArc(sketch, "E335", {"start": v(932.44, -186.75) * mm, "mid": v(936.92, -186.52) * mm, "end": v(937.15, -182.04) * mm});
            skArc(sketch, "E336", {"start": v(954.1, -186.12) * mm, "mid": v(954.4, -186.3) * mm, "end": v(954.73, -186.35) * mm});
            skArc(sketch, "E337", {"start": v(954.1, -186.12) * mm, "mid": v(949.62, -186.35) * mm, "end": v(949.4, -190.83) * mm});
            skArc(sketch, "E338", {"start": v(949.62, -191.46) * mm, "mid": v(949.56, -191.13) * mm, "end": v(949.4, -190.83) * mm});
            skLineSegment(sketch, "E339", {"start": v(949.62, -191.46) * mm, "end": v(949.62, -195.26) * mm});
            skLineSegment(sketch, "E340", {"start": v(949.62, -195.26) * mm, "end": v(945.83, -199.05) * mm});
            skLineSegment(sketch, "E341", {"start": v(945.83, -199.05) * mm, "end": v(889.23, -199.05) * mm});
            skLineSegment(sketch, "E342", {"start": v(889.23, -199.05) * mm, "end": v(885.44, -195.26) * mm});
            skLineSegment(sketch, "E343", {"start": v(885.44, -195.26) * mm, "end": v(885.44, -191.46) * mm});
            skArc(sketch, "E344", {"start": v(885.67, -190.83) * mm, "mid": v(885.5, -191.13) * mm, "end": v(885.44, -191.46) * mm});
            skArc(sketch, "E345", {"start": v(885.67, -190.83) * mm, "mid": v(885.44, -186.35) * mm, "end": v(880.96, -186.12) * mm});
            skArc(sketch, "E346", {"start": v(880.33, -186.35) * mm, "mid": v(880.66, -186.3) * mm, "end": v(880.96, -186.12) * mm});
            skLineSegment(sketch, "E347", {"start": v(880.33, -186.35) * mm, "end": v(842.53, -186.35) * mm});
            skLineSegment(sketch, "E348", {"start": v(842.53, -186.35) * mm, "end": v(842.53, -173.65) * mm});
            skArc(sketch, "E349", {"start": v(849.53, -166.65) * mm, "mid": v(844.58, -168.7) * mm, "end": v(842.53, -173.65) * mm});
            skArc(sketch, "E350", {"start": v(849.53, -166.65) * mm, "mid": v(854.48, -164.6) * mm, "end": v(856.53, -159.65) * mm});
            skLineSegment(sketch, "E351", {"start": v(856.53, 146.95) * mm, "end": v(856.53, -159.65) * mm});
            skArc(sketch, "E352", {"start": v(842.53, 160.95) * mm, "mid": v(844.58, 156) * mm, "end": v(849.53, 153.95) * mm});
            skArc(sketch, "E353", {"start": v(856.53, 146.95) * mm, "mid": v(854.48, 151.9) * mm, "end": v(849.53, 153.95) * mm});
            skArc(sketch, "E354", {"start": v(880.96, 173.42) * mm, "mid": v(880.66, 173.6) * mm, "end": v(880.33, 173.65) * mm});
            skLineSegment(sketch, "E355", {"start": v(880.33, 173.65) * mm, "end": v(842.53, 173.65) * mm});
            skLineSegment(sketch, "E356", {"start": v(842.53, 173.65) * mm, "end": v(842.53, 160.95) * mm});
            skArc(sketch, "E357", {"start": v(949.4, 178.13) * mm, "mid": v(949.56, 178.43) * mm, "end": v(949.62, 178.76) * mm});
            skArc(sketch, "E358", {"start": v(880.96, 173.42) * mm, "mid": v(885.44, 173.65) * mm, "end": v(885.67, 178.13) * mm});
            skArc(sketch, "E359", {"start": v(885.44, 178.76) * mm, "mid": v(885.5, 178.43) * mm, "end": v(885.67, 178.13) * mm});
            skLineSegment(sketch, "E360", {"start": v(885.44, 182.56) * mm, "end": v(885.44, 178.76) * mm});
            skLineSegment(sketch, "E361", {"start": v(889.23, 186.35) * mm, "end": v(885.44, 182.56) * mm});
            skLineSegment(sketch, "E362", {"start": v(945.83, 186.35) * mm, "end": v(889.23, 186.35) * mm});
            skLineSegment(sketch, "E363", {"start": v(949.62, 182.56) * mm, "end": v(945.83, 186.35) * mm});
            skLineSegment(sketch, "E364", {"start": v(949.62, 178.76) * mm, "end": v(949.62, 182.56) * mm});
            skArc(sketch, "E365", {"start": v(949.4, 178.13) * mm, "mid": v(949.62, 173.65) * mm, "end": v(954.1, 173.42) * mm});
            skArc(sketch, "E366", {"start": v(954.73, 173.65) * mm, "mid": v(954.4, 173.6) * mm, "end": v(954.1, 173.42) * mm});
            skLineSegment(sketch, "E367", {"start": v(978.53, 173.65) * mm, "end": v(954.73, 173.65) * mm});
            skLineSegment(sketch, "E368", {"start": v(978.53, 160.55) * mm, "end": v(978.53, 173.65) * mm});
            skArc(sketch, "E369", {"start": v(978.53, 160.55) * mm, "mid": v(980.58, 155.6) * mm, "end": v(985.53, 153.55) * mm});
            skArc(sketch, "E370", {"start": v(992.53, 146.55) * mm, "mid": v(990.48, 151.5) * mm, "end": v(985.53, 153.55) * mm});
            skLineSegment(sketch, "E371", {"start": v(992.53, -159.25) * mm, "end": v(992.53, 146.55) * mm});
            skArc(sketch, "E372", {"start": v(985.53, -166.25) * mm, "mid": v(990.48, -164.2) * mm, "end": v(992.53, -159.25) * mm});
            skArc(sketch, "E373", {"start": v(985.53, -166.25) * mm, "mid": v(980.58, -168.3) * mm, "end": v(978.53, -173.25) * mm});
            skLineSegment(sketch, "E374", {"start": v(931.8, 173.82) * mm, "end": v(903.25, 173.82) * mm});
            skArc(sketch, "E375", {"start": v(937.15, 169.34) * mm, "mid": v(936.92, 173.82) * mm, "end": v(932.44, 174.05) * mm});
            skArc(sketch, "E376", {"start": v(902.62, 174.05) * mm, "mid": v(902.92, 173.88) * mm, "end": v(903.25, 173.82) * mm});
            skArc(sketch, "E377", {"start": v(902.62, 174.05) * mm, "mid": v(898.14, 173.82) * mm, "end": v(897.92, 169.34) * mm});
            skArc(sketch, "E378", {"start": v(898.14, 168.7) * mm, "mid": v(898.08, 169.04) * mm, "end": v(897.92, 169.34) * mm});
            skLineSegment(sketch, "E379", {"start": v(898.14, 168.7) * mm, "end": v(898.14, 165.9) * mm});
            skArc(sketch, "E380", {"start": v(897.92, 165.26) * mm, "mid": v(898.08, 165.56) * mm, "end": v(898.14, 165.9) * mm});
            skArc(sketch, "E381", {"start": v(897.92, 165.26) * mm, "mid": v(898.14, 160.78) * mm, "end": v(902.62, 160.55) * mm});
            skArc(sketch, "E382", {"start": v(903.25, 160.78) * mm, "mid": v(902.92, 160.72) * mm, "end": v(902.62, 160.55) * mm});
            skLineSegment(sketch, "E383", {"start": v(903.25, 160.78) * mm, "end": v(931.8, 160.78) * mm});
            skArc(sketch, "E384", {"start": v(932.44, 160.55) * mm, "mid": v(932.14, 160.72) * mm, "end": v(931.8, 160.78) * mm});
            skArc(sketch, "E385", {"start": v(932.44, 160.55) * mm, "mid": v(936.92, 160.78) * mm, "end": v(937.15, 165.26) * mm});
            skArc(sketch, "E386", {"start": v(936.92, 165.9) * mm, "mid": v(936.98, 165.56) * mm, "end": v(937.15, 165.26) * mm});
            skLineSegment(sketch, "E387", {"start": v(936.92, 165.9) * mm, "end": v(936.92, 168.7) * mm});
            skArc(sketch, "E388", {"start": v(937.15, 169.34) * mm, "mid": v(936.98, 169.04) * mm, "end": v(936.92, 168.7) * mm});
            skArc(sketch, "E389", {"start": v(695.54, -186.52) * mm, "mid": v(695.2, -186.58) * mm, "end": v(694.9, -186.75) * mm});
            skArc(sketch, "E390", {"start": v(690.42, 168.7) * mm, "mid": v(690.36, 169.04) * mm, "end": v(690.2, 169.34) * mm});
            skLineSegment(sketch, "E391", {"start": v(648.81, 160.55) * mm, "end": v(648.81, 173.65) * mm});
            skLineSegment(sketch, "E392", {"start": v(690.42, 165.9) * mm, "end": v(690.42, 168.7) * mm});
            skArc(sketch, "E393", {"start": v(690.2, 165.26) * mm, "mid": v(690.36, 165.56) * mm, "end": v(690.42, 165.9) * mm});
            skArc(sketch, "E394", {"start": v(690.2, 165.26) * mm, "mid": v(690.42, 160.78) * mm, "end": v(694.9, 160.55) * mm});
            skArc(sketch, "E395", {"start": v(695.54, 160.78) * mm, "mid": v(695.2, 160.72) * mm, "end": v(694.9, 160.55) * mm});
            skArc(sketch, "E396", {"start": v(724.72, 160.55) * mm, "mid": v(724.42, 160.72) * mm, "end": v(724.09, 160.78) * mm});
            skLineSegment(sketch, "E397", {"start": v(724.09, 160.78) * mm, "end": v(695.54, 160.78) * mm});
            skArc(sketch, "E398", {"start": v(729.2, 165.9) * mm, "mid": v(729.26, 165.56) * mm, "end": v(729.43, 165.26) * mm});
            skArc(sketch, "E399", {"start": v(724.72, 160.55) * mm, "mid": v(729.2, 160.78) * mm, "end": v(729.43, 165.26) * mm});
            skLineSegment(sketch, "E400", {"start": v(729.2, 168.7) * mm, "end": v(729.2, 165.9) * mm});
            skArc(sketch, "E401", {"start": v(729.43, 169.34) * mm, "mid": v(729.26, 169.04) * mm, "end": v(729.2, 168.7) * mm});
            skArc(sketch, "E402", {"start": v(729.43, 169.34) * mm, "mid": v(729.2, 173.82) * mm, "end": v(724.72, 174.05) * mm});
            skLineSegment(sketch, "E403", {"start": v(695.54, 173.82) * mm, "end": v(724.09, 173.82) * mm});
            skArc(sketch, "E404", {"start": v(724.09, 173.82) * mm, "mid": v(724.42, 173.88) * mm, "end": v(724.72, 174.05) * mm});
            skArc(sketch, "E405", {"start": v(694.9, 174.05) * mm, "mid": v(695.2, 173.88) * mm, "end": v(695.54, 173.82) * mm});
            skArc(sketch, "E406", {"start": v(694.9, 174.05) * mm, "mid": v(690.42, 173.82) * mm, "end": v(690.2, 169.34) * mm});
            skLineSegment(sketch, "E407", {"start": v(648.81, 173.65) * mm, "end": v(672.6, 173.65) * mm});
            skArc(sketch, "E408", {"start": v(673.24, 173.42) * mm, "mid": v(672.94, 173.6) * mm, "end": v(672.6, 173.65) * mm});
            skArc(sketch, "E409", {"start": v(677.72, 178.76) * mm, "mid": v(677.78, 178.43) * mm, "end": v(677.95, 178.13) * mm});
            skArc(sketch, "E410", {"start": v(673.24, 173.42) * mm, "mid": v(677.72, 173.65) * mm, "end": v(677.95, 178.13) * mm});
            skLineSegment(sketch, "E411", {"start": v(677.72, 178.76) * mm, "end": v(677.72, 182.56) * mm});
            skLineSegment(sketch, "E412", {"start": v(677.72, 182.56) * mm, "end": v(681.52, 186.35) * mm});
            skLineSegment(sketch, "E413", {"start": v(681.52, 186.35) * mm, "end": v(738.1, 186.35) * mm});
            skLineSegment(sketch, "E414", {"start": v(738.1, 186.35) * mm, "end": v(741.9, 182.56) * mm});
            skLineSegment(sketch, "E415", {"start": v(741.9, 182.56) * mm, "end": v(741.9, 178.76) * mm});
            skArc(sketch, "E416", {"start": v(741.68, 178.13) * mm, "mid": v(741.84, 178.43) * mm, "end": v(741.9, 178.76) * mm});
            skArc(sketch, "E417", {"start": v(741.68, 178.13) * mm, "mid": v(741.9, 173.65) * mm, "end": v(746.38, 173.42) * mm});
            skArc(sketch, "E418", {"start": v(747.02, 173.65) * mm, "mid": v(746.68, 173.6) * mm, "end": v(746.38, 173.42) * mm});
            skLineSegment(sketch, "E419", {"start": v(747.02, 173.65) * mm, "end": v(784.81, 173.65) * mm});
            skLineSegment(sketch, "E420", {"start": v(784.81, 173.65) * mm, "end": v(784.81, 160.95) * mm});
            skArc(sketch, "E421", {"start": v(777.81, 153.95) * mm, "mid": v(782.76, 156) * mm, "end": v(784.81, 160.95) * mm});
            skArc(sketch, "E422", {"start": v(777.81, 153.95) * mm, "mid": v(772.86, 151.9) * mm, "end": v(770.81, 146.95) * mm});
            skLineSegment(sketch, "E423", {"start": v(770.81, -159.65) * mm, "end": v(770.81, 146.95) * mm});
            skArc(sketch, "E424", {"start": v(770.81, -159.65) * mm, "mid": v(772.86, -164.6) * mm, "end": v(777.81, -166.65) * mm});
            skArc(sketch, "E425", {"start": v(784.81, -173.65) * mm, "mid": v(782.76, -168.7) * mm, "end": v(777.81, -166.65) * mm});
            skLineSegment(sketch, "E426", {"start": v(784.81, -186.35) * mm, "end": v(784.81, -173.65) * mm});
            skArc(sketch, "E427", {"start": v(677.95, -190.83) * mm, "mid": v(677.78, -191.13) * mm, "end": v(677.72, -191.46) * mm});
            skLineSegment(sketch, "E428", {"start": v(747.02, -186.35) * mm, "end": v(784.81, -186.35) * mm});
            skArc(sketch, "E429", {"start": v(746.38, -186.12) * mm, "mid": v(746.68, -186.3) * mm, "end": v(747.02, -186.35) * mm});
            skArc(sketch, "E430", {"start": v(746.38, -186.12) * mm, "mid": v(741.9, -186.35) * mm, "end": v(741.68, -190.83) * mm});
            skArc(sketch, "E431", {"start": v(741.9, -191.46) * mm, "mid": v(741.84, -191.13) * mm, "end": v(741.68, -190.83) * mm});
            skLineSegment(sketch, "E432", {"start": v(741.9, -195.26) * mm, "end": v(741.9, -191.46) * mm});
            skLineSegment(sketch, "E433", {"start": v(738.1, -199.05) * mm, "end": v(741.9, -195.26) * mm});
            skLineSegment(sketch, "E434", {"start": v(681.52, -199.05) * mm, "end": v(738.1, -199.05) * mm});
            skArc(sketch, "E435", {"start": v(634.81, -159.25) * mm, "mid": v(636.86, -164.2) * mm, "end": v(641.81, -166.25) * mm});
            skLineSegment(sketch, "E436", {"start": v(677.72, -195.26) * mm, "end": v(681.52, -199.05) * mm});
            skLineSegment(sketch, "E437", {"start": v(677.72, -191.46) * mm, "end": v(677.72, -195.26) * mm});
            skArc(sketch, "E438", {"start": v(677.95, -190.83) * mm, "mid": v(677.72, -186.35) * mm, "end": v(673.24, -186.12) * mm});
            skArc(sketch, "E439", {"start": v(672.6, -186.35) * mm, "mid": v(672.94, -186.3) * mm, "end": v(673.24, -186.12) * mm});
            skLineSegment(sketch, "E440", {"start": v(648.81, -186.35) * mm, "end": v(672.6, -186.35) * mm});
            skLineSegment(sketch, "E441", {"start": v(648.81, -173.25) * mm, "end": v(648.81, -186.35) * mm});
            skArc(sketch, "E442", {"start": v(648.81, -173.25) * mm, "mid": v(646.76, -168.3) * mm, "end": v(641.81, -166.25) * mm});
            skArc(sketch, "E443", {"start": v(641.81, 153.55) * mm, "mid": v(636.86, 151.5) * mm, "end": v(634.81, 146.55) * mm});
            skLineSegment(sketch, "E444", {"start": v(634.81, 146.55) * mm, "end": v(634.81, -159.25) * mm});
            skLineSegment(sketch, "E445", {"start": v(729.2, -181.4) * mm, "end": v(729.2, -178.6) * mm});
            skArc(sketch, "E446", {"start": v(641.81, 153.55) * mm, "mid": v(646.76, 155.6) * mm, "end": v(648.81, 160.55) * mm});
            skLineSegment(sketch, "E447", {"start": v(695.54, -186.52) * mm, "end": v(724.09, -186.52) * mm});
            skArc(sketch, "E448", {"start": v(724.72, -186.75) * mm, "mid": v(724.42, -186.58) * mm, "end": v(724.09, -186.52) * mm});
            skArc(sketch, "E449", {"start": v(724.72, -186.75) * mm, "mid": v(729.2, -186.52) * mm, "end": v(729.43, -182.04) * mm});
            skArc(sketch, "E450", {"start": v(729.2, -181.4) * mm, "mid": v(729.26, -181.74) * mm, "end": v(729.43, -182.04) * mm});
            skArc(sketch, "E451", {"start": v(729.43, -177.96) * mm, "mid": v(729.2, -173.48) * mm, "end": v(724.72, -173.25) * mm});
            skArc(sketch, "E452", {"start": v(729.43, -177.96) * mm, "mid": v(729.26, -178.26) * mm, "end": v(729.2, -178.6) * mm});
            skArc(sketch, "E453", {"start": v(724.09, -173.48) * mm, "mid": v(724.42, -173.42) * mm, "end": v(724.72, -173.25) * mm});
            skLineSegment(sketch, "E454", {"start": v(724.09, -173.48) * mm, "end": v(695.54, -173.48) * mm});
            skArc(sketch, "E455", {"start": v(694.9, -173.25) * mm, "mid": v(695.2, -173.42) * mm, "end": v(695.54, -173.48) * mm});
            skArc(sketch, "E456", {"start": v(694.9, -173.25) * mm, "mid": v(690.42, -173.48) * mm, "end": v(690.2, -177.96) * mm});
            skArc(sketch, "E457", {"start": v(690.42, -178.6) * mm, "mid": v(690.36, -178.26) * mm, "end": v(690.2, -177.96) * mm});
            skLineSegment(sketch, "E458", {"start": v(690.42, -178.6) * mm, "end": v(690.42, -181.4) * mm});
            skArc(sketch, "E459", {"start": v(690.2, -182.04) * mm, "mid": v(690.36, -181.74) * mm, "end": v(690.42, -181.4) * mm});
            skArc(sketch, "E460", {"start": v(690.2, -182.04) * mm, "mid": v(690.42, -186.52) * mm, "end": v(694.9, -186.75) * mm});
            skLineSegment(sketch, "E461", {"start": v(997.82, -590.25) * mm, "end": v(997.82, -243.75) * mm});
            skLineSegment(sketch, "E462", {"start": v(634.81, -590.25) * mm, "end": v(997.82, -590.25) * mm});
            skLineSegment(sketch, "E463", {"start": v(634.81, -243.75) * mm, "end": v(634.81, -590.25) * mm});
            skLineSegment(sketch, "E464", {"start": v(634.81, -243.75) * mm, "end": v(997.82, -243.75) * mm});
            skCircle(sketch, "E465", {"center": v(357.44, -259.77) * mm, "radius": 3.25 * mm});
            skCircle(sketch, "E466", {"center": v(357.44, -574.23) * mm, "radius": 3.25 * mm});
            skCircle(sketch, "E467", {"center": v(305.9, -312.18) * mm, "radius": 3.25 * mm});
            skCircle(sketch, "E468", {"center": v(254.38, -364.6) * mm, "radius": 3.25 * mm});
            skLineSegment(sketch, "E469", {"start": v(588.56, -590.25) * mm, "end": v(588.56, -243.75) * mm});
            skCircle(sketch, "E470", {"center": v(254.38, -312.18) * mm, "radius": 3.25 * mm});
            skCircle(sketch, "E471", {"center": v(305.9, -259.77) * mm, "radius": 3.25 * mm});
            skCircle(sketch, "E472", {"center": v(357.44, -364.6) * mm, "radius": 3.25 * mm});
            skCircle(sketch, "E473", {"center": v(357.44, -312.18) * mm, "radius": 3.25 * mm});
            skCircle(sketch, "E474", {"center": v(305.9, -364.6) * mm, "radius": 3.25 * mm});
            skCircle(sketch, "E475", {"center": v(460.49, -364.6) * mm, "radius": 3.25 * mm});
            skCircle(sketch, "E476", {"center": v(357.44, -521.82) * mm, "radius": 3.25 * mm});
            skCircle(sketch, "E477", {"center": v(305.9, -469.4) * mm, "radius": 3.25 * mm});
            skCircle(sketch, "E478", {"center": v(254.38, -259.77) * mm, "radius": 3.25 * mm});
            skCircle(sketch, "E479", {"center": v(408.96, -259.77) * mm, "radius": 3.25 * mm});
            skCircle(sketch, "E480", {"center": v(460.49, -259.77) * mm, "radius": 3.25 * mm});
            skCircle(sketch, "E481", {"center": v(512.02, -259.77) * mm, "radius": 3.25 * mm});
            skCircle(sketch, "E482", {"center": v(408.96, -364.6) * mm, "radius": 3.25 * mm});
            skCircle(sketch, "E483", {"center": v(408.96, -312.18) * mm, "radius": 3.25 * mm});
            skCircle(sketch, "E484", {"center": v(512.02, -521.82) * mm, "radius": 3.25 * mm});
            skCircle(sketch, "E485", {"center": v(460.49, -312.18) * mm, "radius": 3.25 * mm});
            skCircle(sketch, "E486", {"center": v(512.02, -364.6) * mm, "radius": 3.25 * mm});
            skCircle(sketch, "E487", {"center": v(512.02, -312.18) * mm, "radius": 3.25 * mm});
            skCircle(sketch, "E488", {"center": v(563.54, -364.6) * mm, "radius": 3.25 * mm});
            skCircle(sketch, "E489", {"center": v(563.54, -312.18) * mm, "radius": 3.25 * mm});
            skCircle(sketch, "E490", {"center": v(563.54, -259.77) * mm, "radius": 3.25 * mm});
            skCircle(sketch, "E491", {"center": v(254.38, -417) * mm, "radius": 3.25 * mm});
            skCircle(sketch, "E492", {"center": v(460.49, -469.4) * mm, "radius": 3.25 * mm});
            skCircle(sketch, "E493", {"center": v(305.9, -574.23) * mm, "radius": 3.25 * mm});
            skCircle(sketch, "E494", {"center": v(357.44, -417) * mm, "radius": 3.25 * mm});
            skCircle(sketch, "E495", {"center": v(357.44, -469.4) * mm, "radius": 3.25 * mm});
            skCircle(sketch, "E496", {"center": v(305.9, -417) * mm, "radius": 3.25 * mm});
            skCircle(sketch, "E497", {"center": v(305.9, -521.82) * mm, "radius": 3.25 * mm});
            skCircle(sketch, "E498", {"center": v(254.38, -469.4) * mm, "radius": 3.25 * mm});
            skCircle(sketch, "E499", {"center": v(254.38, -521.82) * mm, "radius": 3.25 * mm});
            skCircle(sketch, "E500", {"center": v(254.38, -574.23) * mm, "radius": 3.25 * mm});
            skCircle(sketch, "E501", {"center": v(408.96, -574.23) * mm, "radius": 3.25 * mm});
            skCircle(sketch, "E502", {"center": v(460.49, -574.23) * mm, "radius": 3.25 * mm});
            skCircle(sketch, "E503", {"center": v(512.02, -574.23) * mm, "radius": 3.25 * mm});
            skCircle(sketch, "E504", {"center": v(408.96, -417) * mm, "radius": 3.25 * mm});
            skCircle(sketch, "E505", {"center": v(408.96, -469.4) * mm, "radius": 3.25 * mm});
            skCircle(sketch, "E506", {"center": v(408.96, -521.82) * mm, "radius": 3.25 * mm});
            skCircle(sketch, "E507", {"center": v(460.49, -417) * mm, "radius": 3.25 * mm});
            skCircle(sketch, "E508", {"center": v(460.49, -521.82) * mm, "radius": 3.25 * mm});
            skCircle(sketch, "E509", {"center": v(512.02, -417) * mm, "radius": 3.25 * mm});
            skCircle(sketch, "E510", {"center": v(512.02, -469.4) * mm, "radius": 3.25 * mm});
            skCircle(sketch, "E511", {"center": v(563.54, -417) * mm, "radius": 3.25 * mm});
            skCircle(sketch, "E512", {"center": v(563.54, -469.4) * mm, "radius": 3.25 * mm});
            skCircle(sketch, "E513", {"center": v(563.54, -521.82) * mm, "radius": 3.25 * mm});
            skCircle(sketch, "E514", {"center": v(563.54, -574.23) * mm, "radius": 3.25 * mm});
            skLineSegment(sketch, "E515", {"start": v(229.36, -590.25) * mm, "end": v(588.56, -590.25) * mm});
            skLineSegment(sketch, "E516", {"start": v(229.36, -590.25) * mm, "end": v(229.36, -243.75) * mm});
            skLineSegment(sketch, "E517", {"start": v(229.36, -243.75) * mm, "end": v(588.56, -243.75) * mm});
            skArc(sketch, "E518", {"start": v(74.28, -198.8) * mm, "mid": v(78.9, -198.7) * mm, "end": v(79, -194.08) * mm});
            skArc(sketch, "E519", {"start": v(91.6, -184.74) * mm, "mid": v(91.58, -184.6) * mm, "end": v(91.5, -184.47) * mm});
            skLineSegment(sketch, "E520", {"start": v(37.12, -211.8) * mm, "end": v(37.12, -198.7) * mm});
            skArc(sketch, "E521", {"start": v(100.02, -577.65) * mm, "mid": v(99.9, -577.58) * mm, "end": v(99.75, -577.55) * mm});
            skLineSegment(sketch, "E522", {"start": v(37.12, -198.7) * mm, "end": v(74.01, -198.7) * mm});
            skArc(sketch, "E523", {"start": v(74.28, -198.8) * mm, "mid": v(74.16, -198.73) * mm, "end": v(74.01, -198.7) * mm});
            skArc(sketch, "E524", {"start": v(78.9, -193.8) * mm, "mid": v(78.93, -193.95) * mm, "end": v(79, -194.08) * mm});
            skLineSegment(sketch, "E525", {"start": v(78.9, -193.8) * mm, "end": v(78.9, -179.4) * mm});
            skLineSegment(sketch, "E526", {"start": v(78.9, -179.4) * mm, "end": v(91.15, -167.15) * mm});
            skLineSegment(sketch, "E527", {"start": v(91.15, -167.15) * mm, "end": v(105.1, -167.15) * mm});
            skLineSegment(sketch, "E528", {"start": v(105.1, -167.15) * mm, "end": v(117.35, -179.4) * mm});
            skArc(sketch, "E529", {"start": v(117.24, -194.08) * mm, "mid": v(117.32, -193.95) * mm, "end": v(117.34, -193.8) * mm});
            skLineSegment(sketch, "E530", {"start": v(117.35, -179.4) * mm, "end": v(117.35, -193.8) * mm});
            skArc(sketch, "E531", {"start": v(117.24, -194.08) * mm, "mid": v(117.34, -198.7) * mm, "end": v(121.97, -198.8) * mm});
            skArc(sketch, "E532", {"start": v(122.24, -198.7) * mm, "mid": v(122.1, -198.73) * mm, "end": v(121.97, -198.8) * mm});
            skArc(sketch, "E533", {"start": v(173.12, -546) * mm, "mid": v(171.07, -541.05) * mm, "end": v(166.12, -539) * mm});
            skLineSegment(sketch, "E534", {"start": v(122.24, -198.7) * mm, "end": v(173.12, -198.7) * mm});
            skLineSegment(sketch, "E535", {"start": v(173.12, -198.7) * mm, "end": v(173.12, -211.4) * mm});
            skArc(sketch, "E536", {"start": v(166.12, -218.4) * mm, "mid": v(171.07, -216.35) * mm, "end": v(173.12, -211.4) * mm});
            skArc(sketch, "E537", {"start": v(166.12, -218.4) * mm, "mid": v(161.18, -220.45) * mm, "end": v(159.12, -225.4) * mm});
            skLineSegment(sketch, "E538", {"start": v(159.13, -532) * mm, "end": v(159.13, -225.4) * mm});
            skArc(sketch, "E539", {"start": v(159.12, -532) * mm, "mid": v(161.18, -536.95) * mm, "end": v(166.12, -539) * mm});
            skArc(sketch, "E540", {"start": v(121.97, -558.6) * mm, "mid": v(117.34, -558.7) * mm, "end": v(117.24, -563.32) * mm});
            skLineSegment(sketch, "E541", {"start": v(173.12, -558.7) * mm, "end": v(173.12, -546) * mm});
            skLineSegment(sketch, "E542", {"start": v(122.24, -558.7) * mm, "end": v(173.12, -558.7) * mm});
            skArc(sketch, "E543", {"start": v(121.97, -558.6) * mm, "mid": v(122.1, -558.67) * mm, "end": v(122.24, -558.7) * mm});
            skArc(sketch, "E544", {"start": v(117.34, -563.6) * mm, "mid": v(117.32, -563.45) * mm, "end": v(117.24, -563.32) * mm});
            skLineSegment(sketch, "E545", {"start": v(117.35, -578) * mm, "end": v(117.35, -563.6) * mm});
            skLineSegment(sketch, "E546", {"start": v(105.1, -590.25) * mm, "end": v(117.35, -578) * mm});
            skLineSegment(sketch, "E547", {"start": v(91.15, -590.25) * mm, "end": v(105.1, -590.25) * mm});
            skLineSegment(sketch, "E548", {"start": v(78.9, -578) * mm, "end": v(91.15, -590.25) * mm});
            skLineSegment(sketch, "E549", {"start": v(78.9, -563.6) * mm, "end": v(78.9, -578) * mm});
            skArc(sketch, "E550", {"start": v(79, -563.32) * mm, "mid": v(78.93, -563.45) * mm, "end": v(78.9, -563.6) * mm});
            skArc(sketch, "E551", {"start": v(79, -563.32) * mm, "mid": v(78.9, -558.7) * mm, "end": v(74.28, -558.6) * mm});
            skArc(sketch, "E552", {"start": v(74.01, -558.7) * mm, "mid": v(74.16, -558.67) * mm, "end": v(74.28, -558.6) * mm});
            skLineSegment(sketch, "E553", {"start": v(37.12, -545.6) * mm, "end": v(37.12, -558.7) * mm});
            skLineSegment(sketch, "E554", {"start": v(37.12, -558.7) * mm, "end": v(74.01, -558.7) * mm});
            skArc(sketch, "E555", {"start": v(37.12, -545.6) * mm, "mid": v(35.07, -540.65) * mm, "end": v(30.12, -538.6) * mm});
            skArc(sketch, "E556", {"start": v(23.12, -531.6) * mm, "mid": v(25.18, -536.55) * mm, "end": v(30.12, -538.6) * mm});
            skArc(sketch, "E557", {"start": v(99.75, -564.05) * mm, "mid": v(99.9, -564.02) * mm, "end": v(100.02, -563.95) * mm});
            skArc(sketch, "E558", {"start": v(30.12, -218.8) * mm, "mid": v(25.18, -220.85) * mm, "end": v(23.12, -225.8) * mm});
            skLineSegment(sketch, "E559", {"start": v(23.12, -225.8) * mm, "end": v(23.12, -531.6) * mm});
            skArc(sketch, "E560", {"start": v(30.12, -218.8) * mm, "mid": v(35.07, -216.75) * mm, "end": v(37.12, -211.8) * mm});
            skArc(sketch, "E561", {"start": v(100.02, -577.65) * mm, "mid": v(104.65, -577.55) * mm, "end": v(104.75, -572.93) * mm});
            skArc(sketch, "E562", {"start": v(104.65, -572.66) * mm, "mid": v(104.67, -572.8) * mm, "end": v(104.75, -572.93) * mm});
            skLineSegment(sketch, "E563", {"start": v(104.64, -572.66) * mm, "end": v(104.64, -568.94) * mm});
            skArc(sketch, "E564", {"start": v(104.75, -568.67) * mm, "mid": v(104.67, -568.8) * mm, "end": v(104.65, -568.94) * mm});
            skArc(sketch, "E565", {"start": v(104.75, -568.67) * mm, "mid": v(104.64, -564.05) * mm, "end": v(100.02, -563.95) * mm});
            skLineSegment(sketch, "E566", {"start": v(99.75, -564.05) * mm, "end": v(96.5, -564.05) * mm});
            skArc(sketch, "E567", {"start": v(96.23, -563.95) * mm, "mid": v(96.35, -564.02) * mm, "end": v(96.5, -564.05) * mm});
            skArc(sketch, "E568", {"start": v(96.23, -563.95) * mm, "mid": v(91.6, -564.05) * mm, "end": v(91.5, -568.67) * mm});
            skArc(sketch, "E569", {"start": v(91.6, -568.94) * mm, "mid": v(91.58, -568.8) * mm, "end": v(91.5, -568.67) * mm});
            skLineSegment(sketch, "E570", {"start": v(91.6, -568.94) * mm, "end": v(91.6, -572.66) * mm});
            skArc(sketch, "E571", {"start": v(91.5, -572.93) * mm, "mid": v(91.58, -572.8) * mm, "end": v(91.6, -572.66) * mm});
            skArc(sketch, "E572", {"start": v(91.5, -572.93) * mm, "mid": v(91.6, -577.55) * mm, "end": v(96.23, -577.65) * mm});
            skArc(sketch, "E573", {"start": v(96.5, -577.55) * mm, "mid": v(96.35, -577.58) * mm, "end": v(96.23, -577.65) * mm});
            skArc(sketch, "E574", {"start": v(100.02, -193.45) * mm, "mid": v(99.9, -193.38) * mm, "end": v(99.75, -193.35) * mm});
            skLineSegment(sketch, "E575", {"start": v(96.5, -577.55) * mm, "end": v(99.75, -577.55) * mm});
            skLineSegment(sketch, "E576", {"start": v(91.6, -188.46) * mm, "end": v(91.6, -184.74) * mm});
            skArc(sketch, "E577", {"start": v(99.75, -179.85) * mm, "mid": v(99.9, -179.82) * mm, "end": v(100.02, -179.75) * mm});
            skArc(sketch, "E578", {"start": v(91.5, -188.73) * mm, "mid": v(91.58, -188.6) * mm, "end": v(91.6, -188.46) * mm});
            skArc(sketch, "E579", {"start": v(91.5, -188.73) * mm, "mid": v(91.6, -193.35) * mm, "end": v(96.23, -193.45) * mm});
            skLineSegment(sketch, "E580", {"start": v(99.75, -193.35) * mm, "end": v(96.5, -193.35) * mm});
            skArc(sketch, "E581", {"start": v(96.5, -193.35) * mm, "mid": v(96.35, -193.38) * mm, "end": v(96.23, -193.45) * mm});
            skArc(sketch, "E582", {"start": v(100.02, -193.45) * mm, "mid": v(104.65, -193.35) * mm, "end": v(104.75, -188.73) * mm});
            skArc(sketch, "E583", {"start": v(104.65, -188.46) * mm, "mid": v(104.67, -188.6) * mm, "end": v(104.75, -188.73) * mm});
            skLineSegment(sketch, "E584", {"start": v(104.64, -184.74) * mm, "end": v(104.64, -188.46) * mm});
            skArc(sketch, "E585", {"start": v(104.75, -184.47) * mm, "mid": v(104.67, -184.6) * mm, "end": v(104.65, -184.74) * mm});
            skArc(sketch, "E586", {"start": v(104.75, -184.47) * mm, "mid": v(104.64, -179.85) * mm, "end": v(100.02, -179.75) * mm});
            skLineSegment(sketch, "E587", {"start": v(96.5, -179.85) * mm, "end": v(99.75, -179.85) * mm});
            skArc(sketch, "E588", {"start": v(96.23, -179.75) * mm, "mid": v(96.35, -179.82) * mm, "end": v(96.5, -179.85) * mm});
            skArc(sketch, "E589", {"start": v(96.23, -179.75) * mm, "mid": v(91.6, -179.85) * mm, "end": v(91.5, -184.47) * mm});
            skCircle(sketch, "E590", {"center": v(408.96, 118.25) * mm, "radius": 3.25 * mm});
            skCircle(sketch, "E591", {"center": v(357.44, 65.84) * mm, "radius": 3.25 * mm});
            skCircle(sketch, "E592", {"center": v(305.9, 13.43) * mm, "radius": 3.25 * mm});
            skLineSegment(sketch, "E593", {"start": v(588.56, -212.23) * mm, "end": v(588.56, 134.27) * mm});
            skCircle(sketch, "E594", {"center": v(357.44, 118.25) * mm, "radius": 3.25 * mm});
            skCircle(sketch, "E595", {"center": v(305.9, 118.25) * mm, "radius": 3.25 * mm});
            skCircle(sketch, "E596", {"center": v(460.49, 65.84) * mm, "radius": 3.25 * mm});
            skCircle(sketch, "E597", {"center": v(357.44, 13.43) * mm, "radius": 3.25 * mm});
            skCircle(sketch, "E598", {"center": v(460.49, 118.25) * mm, "radius": 3.25 * mm});
            skCircle(sketch, "E599", {"center": v(305.9, 65.84) * mm, "radius": 3.25 * mm});
            skCircle(sketch, "E600", {"center": v(254.38, 13.43) * mm, "radius": 3.25 * mm});
            skCircle(sketch, "E601", {"center": v(254.38, 65.84) * mm, "radius": 3.25 * mm});
            skCircle(sketch, "E602", {"center": v(254.38, 118.25) * mm, "radius": 3.25 * mm});
            skCircle(sketch, "E603", {"center": v(512.02, 13.43) * mm, "radius": 3.25 * mm});
            skCircle(sketch, "E604", {"center": v(512.02, 118.25) * mm, "radius": 3.25 * mm});
            skCircle(sketch, "E605", {"center": v(563.54, 13.43) * mm, "radius": 3.25 * mm});
            skCircle(sketch, "E606", {"center": v(408.96, 13.43) * mm, "radius": 3.25 * mm});
            skCircle(sketch, "E607", {"center": v(512.02, -143.8) * mm, "radius": 3.25 * mm});
            skCircle(sketch, "E608", {"center": v(408.96, 65.84) * mm, "radius": 3.25 * mm});
            skCircle(sketch, "E609", {"center": v(460.49, 13.43) * mm, "radius": 3.25 * mm});
            skCircle(sketch, "E610", {"center": v(512.02, 65.84) * mm, "radius": 3.25 * mm});
            skCircle(sketch, "E611", {"center": v(305.9, -143.8) * mm, "radius": 3.25 * mm});
            skCircle(sketch, "E612", {"center": v(563.54, 65.84) * mm, "radius": 3.25 * mm});
            skCircle(sketch, "E613", {"center": v(563.54, 118.25) * mm, "radius": 3.25 * mm});
            skCircle(sketch, "E614", {"center": v(357.44, -196.21) * mm, "radius": 3.25 * mm});
            skCircle(sketch, "E615", {"center": v(305.9, -196.21) * mm, "radius": 3.25 * mm});
            skCircle(sketch, "E616", {"center": v(357.44, -38.98) * mm, "radius": 3.25 * mm});
            skCircle(sketch, "E617", {"center": v(357.44, -91.4) * mm, "radius": 3.25 * mm});
            skCircle(sketch, "E618", {"center": v(357.44, -143.8) * mm, "radius": 3.25 * mm});
            skCircle(sketch, "E619", {"center": v(305.9, -38.98) * mm, "radius": 3.25 * mm});
            skCircle(sketch, "E620", {"center": v(305.9, -91.4) * mm, "radius": 3.25 * mm});
            skCircle(sketch, "E621", {"center": v(254.38, -38.98) * mm, "radius": 3.25 * mm});
            skCircle(sketch, "E622", {"center": v(254.38, -91.4) * mm, "radius": 3.25 * mm});
            skCircle(sketch, "E623", {"center": v(254.38, -143.8) * mm, "radius": 3.25 * mm});
            skCircle(sketch, "E624", {"center": v(254.38, -196.21) * mm, "radius": 3.25 * mm});
            skCircle(sketch, "E625", {"center": v(408.96, -196.21) * mm, "radius": 3.25 * mm});
            skCircle(sketch, "E626", {"center": v(460.49, -196.21) * mm, "radius": 3.25 * mm});
            skCircle(sketch, "E627", {"center": v(512.02, -196.21) * mm, "radius": 3.25 * mm});
            skCircle(sketch, "E628", {"center": v(512.02, -91.4) * mm, "radius": 3.25 * mm});
            skCircle(sketch, "E629", {"center": v(408.96, -38.98) * mm, "radius": 3.25 * mm});
            skCircle(sketch, "E630", {"center": v(408.96, -91.4) * mm, "radius": 3.25 * mm});
            skCircle(sketch, "E631", {"center": v(408.96, -143.8) * mm, "radius": 3.25 * mm});
            skCircle(sketch, "E632", {"center": v(460.49, -38.98) * mm, "radius": 3.25 * mm});
            skCircle(sketch, "E633", {"center": v(460.49, -91.4) * mm, "radius": 3.25 * mm});
            skCircle(sketch, "E634", {"center": v(460.49, -143.8) * mm, "radius": 3.25 * mm});
            skCircle(sketch, "E635", {"center": v(512.02, -38.98) * mm, "radius": 3.25 * mm});
            skCircle(sketch, "E636", {"center": v(563.54, -38.98) * mm, "radius": 3.25 * mm});
            skCircle(sketch, "E637", {"center": v(563.54, -91.4) * mm, "radius": 3.25 * mm});
            skCircle(sketch, "E638", {"center": v(563.54, -143.8) * mm, "radius": 3.25 * mm});
            skCircle(sketch, "E639", {"center": v(563.54, -196.21) * mm, "radius": 3.25 * mm});
            skLineSegment(sketch, "E640", {"start": v(229.36, -212.23) * mm, "end": v(229.36, 134.27) * mm});
            skLineSegment(sketch, "E641", {"start": v(229.36, -212.23) * mm, "end": v(588.56, -212.23) * mm});
            skLineSegment(sketch, "E642", {"start": v(229.36, 134.27) * mm, "end": v(588.56, 134.27) * mm});
            skArc(sketch, "E643", {"start": v(143.12, 230.25) * mm, "mid": v(141.07, 235.2) * mm, "end": v(136.12, 237.25) * mm});
            skArc(sketch, "E644", {"start": v(63.73, 572.51) * mm, "mid": v(63.67, 572.93) * mm, "end": v(63.47, 573.3) * mm});
            skLineSegment(sketch, "E645", {"start": v(129.12, 244.25) * mm, "end": v(129.12, 550.85) * mm});
            skArc(sketch, "E646", {"start": v(98.09, 217.11) * mm, "mid": v(97.72, 217.31) * mm, "end": v(97.3, 217.38) * mm});
            skArc(sketch, "E647", {"start": v(129.12, 244.25) * mm, "mid": v(131.18, 239.3) * mm, "end": v(136.12, 237.25) * mm});
            skLineSegment(sketch, "E648", {"start": v(143.12, 217.55) * mm, "end": v(143.12, 230.25) * mm});
            skLineSegment(sketch, "E649", {"start": v(115.21, 217.55) * mm, "end": v(143.12, 217.55) * mm});
            skLineSegment(sketch, "E650", {"start": v(57.38, 204.85) * mm, "end": v(108.87, 204.85) * mm});
            skLineSegment(sketch, "E651", {"start": v(115.21, 211.2) * mm, "end": v(115.21, 217.55) * mm});
            skLineSegment(sketch, "E652", {"start": v(108.87, 204.85) * mm, "end": v(115.21, 211.2) * mm});
            skLineSegment(sketch, "E653", {"start": v(51.04, 211.2) * mm, "end": v(57.38, 204.85) * mm});
            skLineSegment(sketch, "E654", {"start": v(51.04, 217.55) * mm, "end": v(51.04, 211.2) * mm});
            skLineSegment(sketch, "E655", {"start": v(23.12, 217.55) * mm, "end": v(51.04, 217.55) * mm});
            skLineSegment(sketch, "E656", {"start": v(23.12, 577.55) * mm, "end": v(23.12, 217.55) * mm});
            skLineSegment(sketch, "E657", {"start": v(23.12, 577.55) * mm, "end": v(51.04, 577.55) * mm});
            skLineSegment(sketch, "E658", {"start": v(51.04, 583.9) * mm, "end": v(57.38, 590.25) * mm});
            skLineSegment(sketch, "E659", {"start": v(51.04, 577.55) * mm, "end": v(51.04, 583.9) * mm});
            skLineSegment(sketch, "E660", {"start": v(57.38, 590.25) * mm, "end": v(108.87, 590.25) * mm});
            skArc(sketch, "E661", {"start": v(136.12, 557.85) * mm, "mid": v(131.18, 555.8) * mm, "end": v(129.12, 550.85) * mm});
            skLineSegment(sketch, "E662", {"start": v(108.87, 590.25) * mm, "end": v(115.21, 583.9) * mm});
            skLineSegment(sketch, "E663", {"start": v(115.21, 583.9) * mm, "end": v(115.21, 577.55) * mm});
            skLineSegment(sketch, "E664", {"start": v(115.21, 577.55) * mm, "end": v(143.12, 577.55) * mm});
            skLineSegment(sketch, "E665", {"start": v(143.12, 577.55) * mm, "end": v(143.12, 564.85) * mm});
            skArc(sketch, "E666", {"start": v(102.78, 226) * mm, "mid": v(102.58, 225.63) * mm, "end": v(102.52, 225.21) * mm});
            skArc(sketch, "E667", {"start": v(136.12, 557.85) * mm, "mid": v(141.07, 559.9) * mm, "end": v(143.12, 564.85) * mm});
            skArc(sketch, "E668", {"start": v(98.09, 217.11) * mm, "mid": v(102.52, 217.38) * mm, "end": v(102.78, 221.8) * mm});
            skArc(sketch, "E669", {"start": v(102.52, 222.59) * mm, "mid": v(102.58, 222.17) * mm, "end": v(102.78, 221.8) * mm});
            skLineSegment(sketch, "E670", {"start": v(102.52, 222.59) * mm, "end": v(102.52, 225.21) * mm});
            skArc(sketch, "E671", {"start": v(63.73, 225.21) * mm, "mid": v(63.67, 225.63) * mm, "end": v(63.47, 226) * mm});
            skArc(sketch, "E672", {"start": v(102.78, 226) * mm, "mid": v(102.51, 230.42) * mm, "end": v(98.09, 230.69) * mm});
            skArc(sketch, "E673", {"start": v(97.3, 230.42) * mm, "mid": v(97.72, 230.49) * mm, "end": v(98.09, 230.69) * mm});
            skLineSegment(sketch, "E674", {"start": v(97.3, 230.42) * mm, "end": v(68.94, 230.42) * mm});
            skArc(sketch, "E675", {"start": v(68.16, 230.69) * mm, "mid": v(68.53, 230.49) * mm, "end": v(68.94, 230.42) * mm});
            skArc(sketch, "E676", {"start": v(63.47, 569.1) * mm, "mid": v(63.67, 569.47) * mm, "end": v(63.73, 569.89) * mm});
            skArc(sketch, "E677", {"start": v(68.16, 230.69) * mm, "mid": v(63.73, 230.42) * mm, "end": v(63.47, 226) * mm});
            skLineSegment(sketch, "E678", {"start": v(63.74, 225.21) * mm, "end": v(63.74, 222.59) * mm});
            skArc(sketch, "E679", {"start": v(63.47, 221.8) * mm, "mid": v(63.67, 222.17) * mm, "end": v(63.73, 222.59) * mm});
            skArc(sketch, "E680", {"start": v(63.47, 221.8) * mm, "mid": v(63.73, 217.38) * mm, "end": v(68.16, 217.11) * mm});
            skArc(sketch, "E681", {"start": v(68.94, 217.38) * mm, "mid": v(68.53, 217.31) * mm, "end": v(68.16, 217.11) * mm});
            skLineSegment(sketch, "E682", {"start": v(68.94, 217.38) * mm, "end": v(97.3, 217.38) * mm});
            skLineSegment(sketch, "E683", {"start": v(63.74, 569.89) * mm, "end": v(63.74, 572.51) * mm});
            skArc(sketch, "E684", {"start": v(102.78, 573.3) * mm, "mid": v(102.58, 572.93) * mm, "end": v(102.52, 572.51) * mm});
            skArc(sketch, "E685", {"start": v(63.47, 569.1) * mm, "mid": v(63.73, 564.68) * mm, "end": v(68.16, 564.41) * mm});
            skArc(sketch, "E686", {"start": v(102.78, 573.3) * mm, "mid": v(102.51, 577.72) * mm, "end": v(98.09, 577.99) * mm});
            skArc(sketch, "E687", {"start": v(68.94, 564.68) * mm, "mid": v(68.53, 564.61) * mm, "end": v(68.16, 564.41) * mm});
            skLineSegment(sketch, "E688", {"start": v(97.3, 564.68) * mm, "end": v(68.94, 564.68) * mm});
            skArc(sketch, "E689", {"start": v(98.09, 564.41) * mm, "mid": v(97.72, 564.61) * mm, "end": v(97.3, 564.68) * mm});
            skArc(sketch, "E690", {"start": v(98.09, 564.41) * mm, "mid": v(102.52, 564.68) * mm, "end": v(102.78, 569.1) * mm});
            skArc(sketch, "E691", {"start": v(102.52, 569.89) * mm, "mid": v(102.58, 569.47) * mm, "end": v(102.78, 569.1) * mm});
            skArc(sketch, "E692", {"start": v(68.16, 577.99) * mm, "mid": v(63.73, 577.72) * mm, "end": v(63.47, 573.3) * mm});
            skLineSegment(sketch, "E693", {"start": v(102.52, 572.51) * mm, "end": v(102.52, 569.89) * mm});
            skArc(sketch, "E694", {"start": v(97.3, 577.72) * mm, "mid": v(97.72, 577.79) * mm, "end": v(98.09, 577.99) * mm});
            skArc(sketch, "E695", {"start": v(68.16, 577.99) * mm, "mid": v(68.53, 577.79) * mm, "end": v(68.94, 577.72) * mm});
            skLineSegment(sketch, "E696", {"start": v(68.94, 577.72) * mm, "end": v(97.3, 577.72) * mm});
            skArc(sketch, "E697", {"start": v(219.89, 437.27) * mm, "mid": v(220.26, 437.07) * mm, "end": v(220.67, 437) * mm});
            skArc(sketch, "E698", {"start": v(215.46, 431.79) * mm, "mid": v(215.4, 432.2) * mm, "end": v(215.2, 432.57) * mm});
            skArc(sketch, "E699", {"start": v(558.56, 165.78) * mm, "mid": v(579.78, 174.57) * mm, "end": v(588.56, 195.78) * mm});
            skArc(sketch, "E700", {"start": v(223.75, 437) * mm, "mid": v(224.17, 437.07) * mm, "end": v(224.54, 437.27) * mm});
            skArc(sketch, "E701", {"start": v(571.05, 437) * mm, "mid": v(571.47, 437.07) * mm, "end": v(571.84, 437.27) * mm});
            skLineSegment(sketch, "E702", {"start": v(223.75, 437) * mm, "end": v(220.67, 437) * mm});
            skArc(sketch, "E703", {"start": v(219.89, 437.27) * mm, "mid": v(215.46, 437) * mm, "end": v(215.2, 432.57) * mm});
            skArc(sketch, "E704", {"start": v(224.54, 320.53) * mm, "mid": v(228.96, 320.8) * mm, "end": v(229.23, 325.22) * mm});
            skArc(sketch, "E705", {"start": v(562.76, 431.79) * mm, "mid": v(562.7, 432.2) * mm, "end": v(562.5, 432.57) * mm});
            skArc(sketch, "E706", {"start": v(215.2, 325.22) * mm, "mid": v(215.4, 325.6) * mm, "end": v(215.46, 326) * mm});
            skLineSegment(sketch, "E707", {"start": v(215.46, 431.79) * mm, "end": v(215.46, 326) * mm});
            skArc(sketch, "E708", {"start": v(215.2, 325.22) * mm, "mid": v(215.46, 320.8) * mm, "end": v(219.89, 320.53) * mm});
            skArc(sketch, "E709", {"start": v(229.23, 432.57) * mm, "mid": v(228.96, 437) * mm, "end": v(224.54, 437.27) * mm});
            skArc(sketch, "E710", {"start": v(220.67, 320.8) * mm, "mid": v(220.26, 320.73) * mm, "end": v(219.89, 320.53) * mm});
            skLineSegment(sketch, "E711", {"start": v(220.67, 320.8) * mm, "end": v(223.75, 320.8) * mm});
            skArc(sketch, "E712", {"start": v(224.54, 320.53) * mm, "mid": v(224.17, 320.73) * mm, "end": v(223.75, 320.8) * mm});
            skArc(sketch, "E713", {"start": v(228.96, 326) * mm, "mid": v(229.03, 325.6) * mm, "end": v(229.23, 325.22) * mm});
            skArc(sketch, "E714", {"start": v(229.23, 432.57) * mm, "mid": v(229.03, 432.2) * mm, "end": v(228.96, 431.79) * mm});
            skLineSegment(sketch, "E715", {"start": v(228.96, 326) * mm, "end": v(228.96, 431.79) * mm});
            skLineSegment(sketch, "E716", {"start": v(571.05, 437) * mm, "end": v(567.97, 437) * mm});
            skArc(sketch, "E717", {"start": v(567.19, 437.27) * mm, "mid": v(567.56, 437.07) * mm, "end": v(567.97, 437) * mm});
            skArc(sketch, "E718", {"start": v(567.19, 437.27) * mm, "mid": v(562.76, 437) * mm, "end": v(562.5, 432.57) * mm});
            skLineSegment(sketch, "E719", {"start": v(562.76, 431.79) * mm, "end": v(562.76, 326) * mm});
            skArc(sketch, "E720", {"start": v(562.5, 325.22) * mm, "mid": v(562.7, 325.6) * mm, "end": v(562.76, 326) * mm});
            skArc(sketch, "E721", {"start": v(562.5, 325.22) * mm, "mid": v(562.76, 320.8) * mm, "end": v(567.19, 320.53) * mm});
            skArc(sketch, "E722", {"start": v(567.97, 320.8) * mm, "mid": v(567.56, 320.73) * mm, "end": v(567.19, 320.53) * mm});
            skArc(sketch, "E723", {"start": v(203.16, 195.78) * mm, "mid": v(211.95, 174.57) * mm, "end": v(233.16, 165.78) * mm});
            skArc(sketch, "E724", {"start": v(571.84, 320.53) * mm, "mid": v(571.47, 320.73) * mm, "end": v(571.05, 320.8) * mm});
            skLineSegment(sketch, "E725", {"start": v(567.97, 320.8) * mm, "end": v(571.05, 320.8) * mm});
            skArc(sketch, "E726", {"start": v(571.84, 320.53) * mm, "mid": v(576.26, 320.8) * mm, "end": v(576.53, 325.22) * mm});
            skArc(sketch, "E727", {"start": v(576.26, 326) * mm, "mid": v(576.33, 325.6) * mm, "end": v(576.53, 325.22) * mm});
            skLineSegment(sketch, "E728", {"start": v(576.26, 326) * mm, "end": v(576.26, 431.79) * mm});
            skArc(sketch, "E729", {"start": v(576.53, 432.57) * mm, "mid": v(576.33, 432.2) * mm, "end": v(576.26, 431.79) * mm});
            skArc(sketch, "E730", {"start": v(588.56, 560.25) * mm, "mid": v(579.78, 581.46) * mm, "end": v(558.56, 590.25) * mm});
            skArc(sketch, "E731", {"start": v(576.53, 432.57) * mm, "mid": v(576.26, 437) * mm, "end": v(571.84, 437.27) * mm});
            skLineSegment(sketch, "E732", {"start": v(233.16, 165.78) * mm, "end": v(558.56, 165.78) * mm});
            skLineSegment(sketch, "E733", {"start": v(203.16, 560.25) * mm, "end": v(203.16, 195.78) * mm});
            skArc(sketch, "E734", {"start": v(233.16, 590.25) * mm, "mid": v(211.95, 581.46) * mm, "end": v(203.16, 560.25) * mm});
            skLineSegment(sketch, "E735", {"start": v(558.56, 590.25) * mm, "end": v(233.16, 590.25) * mm});
            skLineSegment(sketch, "E736", {"start": v(588.56, 195.78) * mm, "end": v(588.56, 560.25) * mm});
            skArc(sketch, "E737", {"start": v(-520.08, 572.66) * mm, "mid": v(-520.1, 572.8) * mm, "end": v(-520.19, 572.93) * mm});
            skLineSegment(sketch, "E738", {"start": v(-574.56, 545.6) * mm, "end": v(-574.56, 558.7) * mm});
            skArc(sketch, "E739", {"start": v(-511.66, 179.75) * mm, "mid": v(-511.79, 179.82) * mm, "end": v(-511.93, 179.85) * mm});
            skLineSegment(sketch, "E740", {"start": v(-574.56, 558.7) * mm, "end": v(-537.67, 558.7) * mm});
            skArc(sketch, "E741", {"start": v(-537.4, 558.6) * mm, "mid": v(-537.53, 558.67) * mm, "end": v(-537.67, 558.7) * mm});
            skArc(sketch, "E742", {"start": v(-537.4, 558.6) * mm, "mid": v(-532.78, 558.7) * mm, "end": v(-532.68, 563.32) * mm});
            skArc(sketch, "E743", {"start": v(-532.78, 563.6) * mm, "mid": v(-532.76, 563.45) * mm, "end": v(-532.68, 563.32) * mm});
            skArc(sketch, "E744", {"start": v(-445.56, 539) * mm, "mid": v(-440.61, 541.05) * mm, "end": v(-438.56, 546) * mm});
            skLineSegment(sketch, "E745", {"start": v(-532.78, 563.6) * mm, "end": v(-532.78, 578) * mm});
            skLineSegment(sketch, "E746", {"start": v(-532.78, 578) * mm, "end": v(-520.54, 590.25) * mm});
            skLineSegment(sketch, "E747", {"start": v(-520.54, 590.25) * mm, "end": v(-506.58, 590.25) * mm});
            skLineSegment(sketch, "E748", {"start": v(-506.58, 590.25) * mm, "end": v(-494.34, 578) * mm});
            skArc(sketch, "E749", {"start": v(-494.45, 563.32) * mm, "mid": v(-494.37, 563.45) * mm, "end": v(-494.34, 563.6) * mm});
            skLineSegment(sketch, "E750", {"start": v(-494.34, 578) * mm, "end": v(-494.34, 563.6) * mm});
            skArc(sketch, "E751", {"start": v(-489.72, 198.8) * mm, "mid": v(-489.6, 198.73) * mm, "end": v(-489.45, 198.7) * mm});
            skArc(sketch, "E752", {"start": v(-494.45, 563.32) * mm, "mid": v(-494.34, 558.7) * mm, "end": v(-489.72, 558.6) * mm});
            skArc(sketch, "E753", {"start": v(-489.45, 558.7) * mm, "mid": v(-489.6, 558.67) * mm, "end": v(-489.72, 558.6) * mm});
            skLineSegment(sketch, "E754", {"start": v(-489.45, 558.7) * mm, "end": v(-438.56, 558.7) * mm});
            skArc(sketch, "E755", {"start": v(-489.72, 198.8) * mm, "mid": v(-494.34, 198.7) * mm, "end": v(-494.45, 194.08) * mm});
            skLineSegment(sketch, "E756", {"start": v(-438.56, 558.7) * mm, "end": v(-438.56, 546) * mm});
            skArc(sketch, "E757", {"start": v(-445.56, 539) * mm, "mid": v(-450.51, 536.95) * mm, "end": v(-452.56, 532) * mm});
            skLineSegment(sketch, "E758", {"start": v(-452.56, 225.4) * mm, "end": v(-452.56, 532) * mm});
            skArc(sketch, "E759", {"start": v(-452.56, 225.4) * mm, "mid": v(-450.51, 220.45) * mm, "end": v(-445.56, 218.4) * mm});
            skArc(sketch, "E760", {"start": v(-438.56, 211.4) * mm, "mid": v(-440.61, 216.35) * mm, "end": v(-445.56, 218.4) * mm});
            skLineSegment(sketch, "E761", {"start": v(-438.56, 198.7) * mm, "end": v(-438.56, 211.4) * mm});
            skLineSegment(sketch, "E762", {"start": v(-489.45, 198.7) * mm, "end": v(-438.56, 198.7) * mm});
            skArc(sketch, "E763", {"start": v(-494.34, 193.8) * mm, "mid": v(-494.37, 193.95) * mm, "end": v(-494.45, 194.08) * mm});
            skLineSegment(sketch, "E764", {"start": v(-494.34, 179.4) * mm, "end": v(-494.34, 193.8) * mm});
            skLineSegment(sketch, "E765", {"start": v(-506.58, 167.15) * mm, "end": v(-494.34, 179.4) * mm});
            skLineSegment(sketch, "E766", {"start": v(-520.54, 167.15) * mm, "end": v(-506.58, 167.15) * mm});
            skLineSegment(sketch, "E767", {"start": v(-532.78, 179.4) * mm, "end": v(-520.54, 167.15) * mm});
            skLineSegment(sketch, "E768", {"start": v(-574.56, 211.8) * mm, "end": v(-574.56, 198.7) * mm});
            skLineSegment(sketch, "E769", {"start": v(-532.78, 193.8) * mm, "end": v(-532.78, 179.4) * mm});
            skArc(sketch, "E770", {"start": v(-532.68, 194.08) * mm, "mid": v(-532.76, 193.95) * mm, "end": v(-532.78, 193.8) * mm});
            skArc(sketch, "E771", {"start": v(-532.68, 194.08) * mm, "mid": v(-532.78, 198.7) * mm, "end": v(-537.4, 198.8) * mm});
            skArc(sketch, "E772", {"start": v(-537.67, 198.7) * mm, "mid": v(-537.53, 198.73) * mm, "end": v(-537.4, 198.8) * mm});
            skLineSegment(sketch, "E773", {"start": v(-574.56, 198.7) * mm, "end": v(-537.67, 198.7) * mm});
            skArc(sketch, "E774", {"start": v(-574.56, 211.8) * mm, "mid": v(-576.61, 216.75) * mm, "end": v(-581.56, 218.8) * mm});
            skArc(sketch, "E775", {"start": v(-588.56, 225.8) * mm, "mid": v(-586.51, 220.85) * mm, "end": v(-581.56, 218.8) * mm});
            skArc(sketch, "E776", {"start": v(-581.56, 538.6) * mm, "mid": v(-586.51, 536.55) * mm, "end": v(-588.56, 531.6) * mm});
            skLineSegment(sketch, "E777", {"start": v(-588.56, 531.6) * mm, "end": v(-588.56, 225.8) * mm});
            skArc(sketch, "E778", {"start": v(-581.56, 538.6) * mm, "mid": v(-576.61, 540.65) * mm, "end": v(-574.56, 545.6) * mm});
            skArc(sketch, "E779", {"start": v(-511.66, 179.75) * mm, "mid": v(-507.04, 179.85) * mm, "end": v(-506.94, 184.47) * mm});
            skArc(sketch, "E780", {"start": v(-507.04, 184.74) * mm, "mid": v(-507.02, 184.6) * mm, "end": v(-506.94, 184.47) * mm});
            skArc(sketch, "E781", {"start": v(-520.19, 568.67) * mm, "mid": v(-520.08, 564.05) * mm, "end": v(-515.46, 563.95) * mm});
            skLineSegment(sketch, "E782", {"start": v(-507.04, 184.74) * mm, "end": v(-507.04, 188.46) * mm});
            skArc(sketch, "E783", {"start": v(-506.94, 188.73) * mm, "mid": v(-507.04, 193.35) * mm, "end": v(-511.66, 193.45) * mm});
            skArc(sketch, "E784", {"start": v(-506.94, 188.73) * mm, "mid": v(-507.02, 188.6) * mm, "end": v(-507.04, 188.46) * mm});
            skArc(sketch, "E785", {"start": v(-511.93, 193.35) * mm, "mid": v(-511.79, 193.38) * mm, "end": v(-511.66, 193.45) * mm});
            skLineSegment(sketch, "E786", {"start": v(-511.93, 193.35) * mm, "end": v(-515.2, 193.35) * mm});
            skArc(sketch, "E787", {"start": v(-515.46, 193.45) * mm, "mid": v(-520.08, 193.35) * mm, "end": v(-520.19, 188.73) * mm});
            skArc(sketch, "E788", {"start": v(-515.46, 193.45) * mm, "mid": v(-515.34, 193.38) * mm, "end": v(-515.2, 193.35) * mm});
            skArc(sketch, "E789", {"start": v(-520.08, 188.46) * mm, "mid": v(-520.1, 188.6) * mm, "end": v(-520.19, 188.73) * mm});
            skArc(sketch, "E790", {"start": v(-520.19, 184.47) * mm, "mid": v(-520.1, 184.6) * mm, "end": v(-520.08, 184.74) * mm});
            skLineSegment(sketch, "E791", {"start": v(-520.08, 188.46) * mm, "end": v(-520.08, 184.74) * mm});
            skArc(sketch, "E792", {"start": v(-520.19, 184.47) * mm, "mid": v(-520.08, 179.85) * mm, "end": v(-515.46, 179.75) * mm});
            skArc(sketch, "E793", {"start": v(-515.2, 179.85) * mm, "mid": v(-515.34, 179.82) * mm, "end": v(-515.46, 179.75) * mm});
            skLineSegment(sketch, "E794", {"start": v(-515.2, 179.85) * mm, "end": v(-511.93, 179.85) * mm});
            skLineSegment(sketch, "E795", {"start": v(-520.08, 568.94) * mm, "end": v(-520.08, 572.66) * mm});
            skArc(sketch, "E796", {"start": v(-520.19, 568.67) * mm, "mid": v(-520.1, 568.8) * mm, "end": v(-520.08, 568.94) * mm});
            skArc(sketch, "E797", {"start": v(-507.04, 568.94) * mm, "mid": v(-507.02, 568.8) * mm, "end": v(-506.94, 568.67) * mm});
            skArc(sketch, "E798", {"start": v(-515.2, 564.05) * mm, "mid": v(-515.34, 564.02) * mm, "end": v(-515.46, 563.95) * mm});
            skLineSegment(sketch, "E799", {"start": v(-511.93, 564.05) * mm, "end": v(-515.2, 564.05) * mm});
            skArc(sketch, "E800", {"start": v(-511.66, 563.95) * mm, "mid": v(-511.79, 564.02) * mm, "end": v(-511.93, 564.05) * mm});
            skArc(sketch, "E801", {"start": v(-511.66, 563.95) * mm, "mid": v(-507.04, 564.05) * mm, "end": v(-506.94, 568.67) * mm});
            skArc(sketch, "E802", {"start": v(-515.46, 577.65) * mm, "mid": v(-515.34, 577.58) * mm, "end": v(-515.2, 577.55) * mm});
            skArc(sketch, "E803", {"start": v(-506.94, 572.93) * mm, "mid": v(-507.02, 572.8) * mm, "end": v(-507.04, 572.66) * mm});
            skLineSegment(sketch, "E804", {"start": v(-507.04, 572.66) * mm, "end": v(-507.04, 568.94) * mm});
            skArc(sketch, "E805", {"start": v(-506.94, 572.93) * mm, "mid": v(-507.04, 577.55) * mm, "end": v(-511.66, 577.65) * mm});
            skArc(sketch, "E806", {"start": v(-511.93, 577.55) * mm, "mid": v(-511.79, 577.58) * mm, "end": v(-511.66, 577.65) * mm});
            skLineSegment(sketch, "E807", {"start": v(-515.2, 577.55) * mm, "end": v(-511.93, 577.55) * mm});
            skArc(sketch, "E808", {"start": v(-515.46, 577.65) * mm, "mid": v(-520.08, 577.55) * mm, "end": v(-520.19, 572.93) * mm});
            skArc(sketch, "E809", {"start": v(-307, 198.8) * mm, "mid": v(-306.88, 198.73) * mm, "end": v(-306.73, 198.7) * mm});
            skArc(sketch, "E810", {"start": v(-311.62, 193.8) * mm, "mid": v(-311.65, 193.95) * mm, "end": v(-311.73, 194.08) * mm});
            skArc(sketch, "E811", {"start": v(-324.32, 184.74) * mm, "mid": v(-324.3, 184.6) * mm, "end": v(-324.22, 184.47) * mm});
            skArc(sketch, "E812", {"start": v(-332.74, 577.65) * mm, "mid": v(-332.62, 577.58) * mm, "end": v(-332.47, 577.55) * mm});
            skLineSegment(sketch, "E813", {"start": v(-269.84, 211.8) * mm, "end": v(-269.84, 198.7) * mm});
            skLineSegment(sketch, "E814", {"start": v(-323.86, 167.15) * mm, "end": v(-337.82, 167.15) * mm});
            skLineSegment(sketch, "E815", {"start": v(-269.84, 198.7) * mm, "end": v(-306.73, 198.7) * mm});
            skArc(sketch, "E816", {"start": v(-354.95, 198.7) * mm, "mid": v(-354.8, 198.73) * mm, "end": v(-354.68, 198.8) * mm});
            skArc(sketch, "E817", {"start": v(-307, 198.8) * mm, "mid": v(-311.62, 198.7) * mm, "end": v(-311.73, 194.08) * mm});
            skLineSegment(sketch, "E818", {"start": v(-311.62, 193.8) * mm, "end": v(-311.62, 179.4) * mm});
            skLineSegment(sketch, "E819", {"start": v(-311.62, 179.4) * mm, "end": v(-323.86, 167.15) * mm});
            skLineSegment(sketch, "E820", {"start": v(-337.82, 167.15) * mm, "end": v(-350.06, 179.4) * mm});
            skLineSegment(sketch, "E821", {"start": v(-350.06, 179.4) * mm, "end": v(-350.06, 193.8) * mm});
            skArc(sketch, "E822", {"start": v(-350.06, 563.6) * mm, "mid": v(-350.04, 563.45) * mm, "end": v(-349.96, 563.32) * mm});
            skArc(sketch, "E823", {"start": v(-349.96, 194.08) * mm, "mid": v(-350.04, 193.95) * mm, "end": v(-350.06, 193.8) * mm});
            skArc(sketch, "E824", {"start": v(-349.96, 194.08) * mm, "mid": v(-350.06, 198.7) * mm, "end": v(-354.68, 198.8) * mm});
            skLineSegment(sketch, "E825", {"start": v(-354.95, 198.7) * mm, "end": v(-405.84, 198.7) * mm});
            skLineSegment(sketch, "E826", {"start": v(-405.84, 198.7) * mm, "end": v(-405.84, 211.4) * mm});
            skArc(sketch, "E827", {"start": v(-398.84, 218.4) * mm, "mid": v(-403.8, 216.35) * mm, "end": v(-405.84, 211.4) * mm});
            skArc(sketch, "E828", {"start": v(-398.84, 218.4) * mm, "mid": v(-393.9, 220.45) * mm, "end": v(-391.84, 225.4) * mm});
            skLineSegment(sketch, "E829", {"start": v(-391.84, 532) * mm, "end": v(-391.84, 225.4) * mm});
            skArc(sketch, "E830", {"start": v(-391.84, 532) * mm, "mid": v(-393.9, 536.95) * mm, "end": v(-398.84, 539) * mm});
            skArc(sketch, "E831", {"start": v(-405.84, 546) * mm, "mid": v(-403.8, 541.05) * mm, "end": v(-398.84, 539) * mm});
            skLineSegment(sketch, "E832", {"start": v(-405.84, 558.7) * mm, "end": v(-405.84, 546) * mm});
            skArc(sketch, "E833", {"start": v(-354.68, 558.6) * mm, "mid": v(-354.8, 558.67) * mm, "end": v(-354.95, 558.7) * mm});
            skLineSegment(sketch, "E834", {"start": v(-354.95, 558.7) * mm, "end": v(-405.84, 558.7) * mm});
            skArc(sketch, "E835", {"start": v(-354.68, 558.6) * mm, "mid": v(-350.06, 558.7) * mm, "end": v(-349.96, 563.32) * mm});
            skLineSegment(sketch, "E836", {"start": v(-337.82, 590.25) * mm, "end": v(-350.06, 578) * mm});
            skLineSegment(sketch, "E837", {"start": v(-350.06, 578) * mm, "end": v(-350.06, 563.6) * mm});
            skLineSegment(sketch, "E838", {"start": v(-323.86, 590.25) * mm, "end": v(-337.82, 590.25) * mm});
            skLineSegment(sketch, "E839", {"start": v(-311.62, 578) * mm, "end": v(-323.86, 590.25) * mm});
            skArc(sketch, "E840", {"start": v(-328.94, 563.95) * mm, "mid": v(-329.07, 564.02) * mm, "end": v(-329.21, 564.05) * mm});
            skLineSegment(sketch, "E841", {"start": v(-311.62, 563.6) * mm, "end": v(-311.62, 578) * mm});
            skArc(sketch, "E842", {"start": v(-311.73, 563.32) * mm, "mid": v(-311.65, 563.45) * mm, "end": v(-311.62, 563.6) * mm});
            skArc(sketch, "E843", {"start": v(-311.73, 563.32) * mm, "mid": v(-311.62, 558.7) * mm, "end": v(-307, 558.6) * mm});
            skArc(sketch, "E844", {"start": v(-306.73, 558.7) * mm, "mid": v(-306.88, 558.67) * mm, "end": v(-307, 558.6) * mm});
            skLineSegment(sketch, "E845", {"start": v(-269.84, 558.7) * mm, "end": v(-306.73, 558.7) * mm});
            skLineSegment(sketch, "E846", {"start": v(-269.84, 545.6) * mm, "end": v(-269.84, 558.7) * mm});
            skArc(sketch, "E847", {"start": v(-269.84, 545.6) * mm, "mid": v(-267.8, 540.65) * mm, "end": v(-262.84, 538.6) * mm});
            skArc(sketch, "E848", {"start": v(-255.84, 531.6) * mm, "mid": v(-257.9, 536.55) * mm, "end": v(-262.84, 538.6) * mm});
            skLineSegment(sketch, "E849", {"start": v(-255.84, 225.8) * mm, "end": v(-255.84, 531.6) * mm});
            skArc(sketch, "E850", {"start": v(-262.84, 218.8) * mm, "mid": v(-257.9, 220.85) * mm, "end": v(-255.84, 225.8) * mm});
            skArc(sketch, "E851", {"start": v(-262.84, 218.8) * mm, "mid": v(-267.8, 216.75) * mm, "end": v(-269.84, 211.8) * mm});
            skArc(sketch, "E852", {"start": v(-332.74, 577.65) * mm, "mid": v(-337.36, 577.55) * mm, "end": v(-337.47, 572.93) * mm});
            skArc(sketch, "E853", {"start": v(-337.36, 572.66) * mm, "mid": v(-337.4, 572.8) * mm, "end": v(-337.47, 572.93) * mm});
            skArc(sketch, "E854", {"start": v(-337.47, 568.67) * mm, "mid": v(-337.4, 568.8) * mm, "end": v(-337.36, 568.94) * mm});
            skLineSegment(sketch, "E855", {"start": v(-337.36, 572.66) * mm, "end": v(-337.36, 568.94) * mm});
            skArc(sketch, "E856", {"start": v(-337.47, 568.67) * mm, "mid": v(-337.36, 564.05) * mm, "end": v(-332.74, 563.95) * mm});
            skArc(sketch, "E857", {"start": v(-332.47, 564.05) * mm, "mid": v(-332.62, 564.02) * mm, "end": v(-332.74, 563.95) * mm});
            skLineSegment(sketch, "E858", {"start": v(-332.47, 564.05) * mm, "end": v(-329.21, 564.05) * mm});
            skArc(sketch, "E859", {"start": v(-324.32, 568.94) * mm, "mid": v(-324.3, 568.8) * mm, "end": v(-324.22, 568.67) * mm});
            skArc(sketch, "E860", {"start": v(-328.94, 563.95) * mm, "mid": v(-324.32, 564.05) * mm, "end": v(-324.22, 568.67) * mm});
            skLineSegment(sketch, "E861", {"start": v(-324.32, 568.94) * mm, "end": v(-324.32, 572.66) * mm});
            skArc(sketch, "E862", {"start": v(-324.22, 572.93) * mm, "mid": v(-324.3, 572.8) * mm, "end": v(-324.32, 572.66) * mm});
            skArc(sketch, "E863", {"start": v(-329.21, 577.55) * mm, "mid": v(-329.07, 577.58) * mm, "end": v(-328.94, 577.65) * mm});
            skArc(sketch, "E864", {"start": v(-324.22, 572.93) * mm, "mid": v(-324.32, 577.55) * mm, "end": v(-328.94, 577.65) * mm});
            skLineSegment(sketch, "E865", {"start": v(-329.21, 577.55) * mm, "end": v(-332.47, 577.55) * mm});
            skLineSegment(sketch, "E866", {"start": v(-324.32, 188.46) * mm, "end": v(-324.32, 184.74) * mm});
            skArc(sketch, "E867", {"start": v(-324.22, 188.73) * mm, "mid": v(-324.3, 188.6) * mm, "end": v(-324.32, 188.46) * mm});
            skArc(sketch, "E868", {"start": v(-324.22, 188.73) * mm, "mid": v(-324.32, 193.35) * mm, "end": v(-328.94, 193.45) * mm});
            skArc(sketch, "E869", {"start": v(-329.21, 193.35) * mm, "mid": v(-329.07, 193.38) * mm, "end": v(-328.94, 193.45) * mm});
            skLineSegment(sketch, "E870", {"start": v(-332.47, 193.35) * mm, "end": v(-329.21, 193.35) * mm});
            skArc(sketch, "E871", {"start": v(-332.74, 193.45) * mm, "mid": v(-332.62, 193.38) * mm, "end": v(-332.47, 193.35) * mm});
            skArc(sketch, "E872", {"start": v(-332.74, 193.45) * mm, "mid": v(-337.36, 193.35) * mm, "end": v(-337.47, 188.73) * mm});
            skArc(sketch, "E873", {"start": v(-337.36, 188.46) * mm, "mid": v(-337.4, 188.6) * mm, "end": v(-337.47, 188.73) * mm});
            skLineSegment(sketch, "E874", {"start": v(-337.36, 184.74) * mm, "end": v(-337.36, 188.46) * mm});
            skArc(sketch, "E875", {"start": v(-337.47, 184.47) * mm, "mid": v(-337.4, 184.6) * mm, "end": v(-337.36, 184.74) * mm});
            skArc(sketch, "E876", {"start": v(-337.47, 184.47) * mm, "mid": v(-337.36, 179.85) * mm, "end": v(-332.74, 179.75) * mm});
            skArc(sketch, "E877", {"start": v(-332.47, 179.85) * mm, "mid": v(-332.62, 179.82) * mm, "end": v(-332.74, 179.75) * mm});
            skLineSegment(sketch, "E878", {"start": v(-329.21, 179.85) * mm, "end": v(-332.47, 179.85) * mm});
            skArc(sketch, "E879", {"start": v(-328.94, 179.75) * mm, "mid": v(-329.07, 179.82) * mm, "end": v(-329.21, 179.85) * mm});
            skArc(sketch, "E880", {"start": v(-328.94, 179.75) * mm, "mid": v(-324.32, 179.85) * mm, "end": v(-324.22, 184.47) * mm});
            skArc(sketch, "E881", {"start": v(-92.42, 198.93) * mm, "mid": v(-96.9, 198.7) * mm, "end": v(-97.13, 194.22) * mm});
            skArc(sketch, "E882", {"start": v(-122.65, 572.66) * mm, "mid": v(-122.67, 572.8) * mm, "end": v(-122.75, 572.93) * mm});
            skLineSegment(sketch, "E883", {"start": v(-209.12, 545.6) * mm, "end": v(-209.12, 558.7) * mm});
            skArc(sketch, "E884", {"start": v(-114.23, 179.75) * mm, "mid": v(-114.35, 179.82) * mm, "end": v(-114.5, 179.85) * mm});
            skArc(sketch, "E885", {"start": v(-139.83, 558.47) * mm, "mid": v(-135.34, 558.7) * mm, "end": v(-135.12, 563.18) * mm});
            skLineSegment(sketch, "E886", {"start": v(-209.12, 558.7) * mm, "end": v(-140.46, 558.7) * mm});
            skArc(sketch, "E887", {"start": v(-139.83, 558.47) * mm, "mid": v(-140.12, 558.64) * mm, "end": v(-140.46, 558.7) * mm});
            skArc(sketch, "E888", {"start": v(-135.35, 563.81) * mm, "mid": v(-135.29, 563.48) * mm, "end": v(-135.12, 563.18) * mm});
            skLineSegment(sketch, "E889", {"start": v(-135.35, 563.81) * mm, "end": v(-135.35, 577.79) * mm});
            skLineSegment(sketch, "E890", {"start": v(-135.35, 577.79) * mm, "end": v(-122.88, 590.25) * mm});
            skLineSegment(sketch, "E891", {"start": v(-122.88, 590.25) * mm, "end": v(-109.37, 590.25) * mm});
            skLineSegment(sketch, "E892", {"start": v(-109.37, 590.25) * mm, "end": v(-96.9, 577.79) * mm});
            skLineSegment(sketch, "E893", {"start": v(-96.9, 577.79) * mm, "end": v(-96.9, 563.81) * mm});
            skArc(sketch, "E894", {"start": v(-97.13, 563.18) * mm, "mid": v(-96.96, 563.48) * mm, "end": v(-96.9, 563.81) * mm});
            skArc(sketch, "E895", {"start": v(-97.13, 563.18) * mm, "mid": v(-96.9, 558.7) * mm, "end": v(-92.42, 558.47) * mm});
            skArc(sketch, "E896", {"start": v(-91.8, 558.7) * mm, "mid": v(-92.13, 558.64) * mm, "end": v(-92.42, 558.47) * mm});
            skLineSegment(sketch, "E897", {"start": v(-91.8, 558.7) * mm, "end": v(-23.13, 558.7) * mm});
            skLineSegment(sketch, "E898", {"start": v(-23.12, 558.7) * mm, "end": v(-23.12, 545.6) * mm});
            skArc(sketch, "E899", {"start": v(-61.12, 507.6) * mm, "mid": v(-34.25, 518.73) * mm, "end": v(-23.12, 545.6) * mm});
            skArc(sketch, "E900", {"start": v(-61.12, 507.6) * mm, "mid": v(-88, 496.47) * mm, "end": v(-99.12, 469.6) * mm});
            skLineSegment(sketch, "E901", {"start": v(-99.12, 287.8) * mm, "end": v(-99.12, 469.6) * mm});
            skArc(sketch, "E902", {"start": v(-99.12, 287.8) * mm, "mid": v(-88, 260.93) * mm, "end": v(-61.12, 249.8) * mm});
            skArc(sketch, "E903", {"start": v(-23.12, 211.8) * mm, "mid": v(-34.25, 238.67) * mm, "end": v(-61.12, 249.8) * mm});
            skLineSegment(sketch, "E904", {"start": v(-23.12, 198.7) * mm, "end": v(-23.12, 211.8) * mm});
            skArc(sketch, "E905", {"start": v(-118.02, 193.45) * mm, "mid": v(-122.65, 193.35) * mm, "end": v(-122.75, 188.73) * mm});
            skLineSegment(sketch, "E906", {"start": v(-91.8, 198.7) * mm, "end": v(-23.13, 198.7) * mm});
            skArc(sketch, "E907", {"start": v(-122.75, 184.47) * mm, "mid": v(-122.65, 179.85) * mm, "end": v(-118.02, 179.75) * mm});
            skArc(sketch, "E908", {"start": v(-92.42, 198.93) * mm, "mid": v(-92.13, 198.76) * mm, "end": v(-91.8, 198.7) * mm});
            skArc(sketch, "E909", {"start": v(-96.9, 193.59) * mm, "mid": v(-96.96, 193.92) * mm, "end": v(-97.13, 194.22) * mm});
            skLineSegment(sketch, "E910", {"start": v(-96.9, 179.61) * mm, "end": v(-96.9, 193.59) * mm});
            skLineSegment(sketch, "E911", {"start": v(-109.37, 167.15) * mm, "end": v(-96.9, 179.61) * mm});
            skLineSegment(sketch, "E912", {"start": v(-122.88, 167.15) * mm, "end": v(-109.37, 167.15) * mm});
            skLineSegment(sketch, "E913", {"start": v(-135.35, 179.61) * mm, "end": v(-122.88, 167.15) * mm});
            skArc(sketch, "E914", {"start": v(-122.75, 568.67) * mm, "mid": v(-122.67, 568.8) * mm, "end": v(-122.65, 568.94) * mm});
            skLineSegment(sketch, "E915", {"start": v(-135.35, 193.59) * mm, "end": v(-135.35, 179.61) * mm});
            skArc(sketch, "E916", {"start": v(-135.12, 194.22) * mm, "mid": v(-135.29, 193.92) * mm, "end": v(-135.35, 193.59) * mm});
            skArc(sketch, "E917", {"start": v(-135.12, 194.22) * mm, "mid": v(-135.34, 198.7) * mm, "end": v(-139.83, 198.93) * mm});
            skArc(sketch, "E918", {"start": v(-140.46, 198.7) * mm, "mid": v(-140.12, 198.76) * mm, "end": v(-139.83, 198.93) * mm});
            skLineSegment(sketch, "E919", {"start": v(-209.12, 198.7) * mm, "end": v(-140.46, 198.7) * mm});
            skLineSegment(sketch, "E920", {"start": v(-209.12, 211.8) * mm, "end": v(-209.12, 198.7) * mm});
            skArc(sketch, "E921", {"start": v(-209.12, 211.8) * mm, "mid": v(-211.18, 216.75) * mm, "end": v(-216.12, 218.8) * mm});
            skArc(sketch, "E922", {"start": v(-223.13, 225.8) * mm, "mid": v(-221.07, 220.85) * mm, "end": v(-216.12, 218.8) * mm});
            skLineSegment(sketch, "E923", {"start": v(-223.13, 531.6) * mm, "end": v(-223.13, 225.8) * mm});
            skArc(sketch, "E924", {"start": v(-216.12, 538.6) * mm, "mid": v(-221.07, 536.55) * mm, "end": v(-223.13, 531.6) * mm});
            skArc(sketch, "E925", {"start": v(-216.12, 538.6) * mm, "mid": v(-211.18, 540.65) * mm, "end": v(-209.12, 545.6) * mm});
            skArc(sketch, "E926", {"start": v(-114.23, 179.75) * mm, "mid": v(-109.6, 179.85) * mm, "end": v(-109.5, 184.47) * mm});
            skArc(sketch, "E927", {"start": v(-109.6, 184.74) * mm, "mid": v(-109.58, 184.6) * mm, "end": v(-109.5, 184.47) * mm});
            skLineSegment(sketch, "E928", {"start": v(-109.6, 184.74) * mm, "end": v(-109.6, 188.46) * mm});
            skArc(sketch, "E929", {"start": v(-109.5, 188.73) * mm, "mid": v(-109.58, 188.6) * mm, "end": v(-109.6, 188.46) * mm});
            skArc(sketch, "E930", {"start": v(-114.5, 193.35) * mm, "mid": v(-114.35, 193.38) * mm, "end": v(-114.23, 193.45) * mm});
            skArc(sketch, "E931", {"start": v(-109.5, 188.73) * mm, "mid": v(-109.6, 193.35) * mm, "end": v(-114.23, 193.45) * mm});
            skLineSegment(sketch, "E932", {"start": v(-114.5, 193.35) * mm, "end": v(-117.75, 193.35) * mm});
            skArc(sketch, "E933", {"start": v(-118.02, 193.45) * mm, "mid": v(-117.9, 193.38) * mm, "end": v(-117.75, 193.35) * mm});
            skArc(sketch, "E934", {"start": v(-122.65, 188.46) * mm, "mid": v(-122.67, 188.6) * mm, "end": v(-122.75, 188.73) * mm});
            skLineSegment(sketch, "E935", {"start": v(-122.64, 188.46) * mm, "end": v(-122.64, 184.74) * mm});
            skArc(sketch, "E936", {"start": v(-122.75, 184.47) * mm, "mid": v(-122.67, 184.6) * mm, "end": v(-122.65, 184.74) * mm});
            skArc(sketch, "E937", {"start": v(-117.75, 179.85) * mm, "mid": v(-117.9, 179.82) * mm, "end": v(-118.02, 179.75) * mm});
            skLineSegment(sketch, "E938", {"start": v(-117.75, 179.85) * mm, "end": v(-114.5, 179.85) * mm});
            skLineSegment(sketch, "E939", {"start": v(-122.64, 568.94) * mm, "end": v(-122.64, 572.66) * mm});
            skArc(sketch, "E940", {"start": v(-122.75, 568.67) * mm, "mid": v(-122.65, 564.05) * mm, "end": v(-118.02, 563.95) * mm});
            skArc(sketch, "E941", {"start": v(-117.75, 564.05) * mm, "mid": v(-117.9, 564.02) * mm, "end": v(-118.02, 563.95) * mm});
            skLineSegment(sketch, "E942", {"start": v(-114.5, 564.05) * mm, "end": v(-117.75, 564.05) * mm});
            skArc(sketch, "E943", {"start": v(-114.23, 563.95) * mm, "mid": v(-114.35, 564.02) * mm, "end": v(-114.5, 564.05) * mm});
            skArc(sketch, "E944", {"start": v(-114.23, 563.95) * mm, "mid": v(-109.6, 564.05) * mm, "end": v(-109.5, 568.67) * mm});
            skArc(sketch, "E945", {"start": v(-109.6, 568.94) * mm, "mid": v(-109.58, 568.8) * mm, "end": v(-109.5, 568.67) * mm});
            skArc(sketch, "E946", {"start": v(-109.5, 572.93) * mm, "mid": v(-109.58, 572.8) * mm, "end": v(-109.6, 572.66) * mm});
            skLineSegment(sketch, "E947", {"start": v(-109.6, 572.66) * mm, "end": v(-109.6, 568.94) * mm});
            skArc(sketch, "E948", {"start": v(-118.02, 577.65) * mm, "mid": v(-122.65, 577.55) * mm, "end": v(-122.75, 572.93) * mm});
            skArc(sketch, "E949", {"start": v(-109.5, 572.93) * mm, "mid": v(-109.6, 577.55) * mm, "end": v(-114.23, 577.65) * mm});
            skArc(sketch, "E950", {"start": v(-114.5, 577.55) * mm, "mid": v(-114.35, 577.58) * mm, "end": v(-114.23, 577.65) * mm});
            skLineSegment(sketch, "E951", {"start": v(-117.75, 577.55) * mm, "end": v(-114.5, 577.55) * mm});
            skArc(sketch, "E952", {"start": v(-118.02, 577.65) * mm, "mid": v(-117.9, 577.58) * mm, "end": v(-117.75, 577.55) * mm});
            skArc(sketch, "E953", {"start": v(-135.12, -295.34) * mm, "mid": v(-135.34, -290.86) * mm, "end": v(-139.83, -290.64) * mm});
            skArc(sketch, "E954", {"start": v(-122.65, 83.1) * mm, "mid": v(-122.67, 83.24) * mm, "end": v(-122.75, 83.37) * mm});
            skLineSegment(sketch, "E955", {"start": v(-209.12, 56.04) * mm, "end": v(-209.12, 69.14) * mm});
            skArc(sketch, "E956", {"start": v(-114.23, -309.82) * mm, "mid": v(-114.35, -309.74) * mm, "end": v(-114.5, -309.71) * mm});
            skLineSegment(sketch, "E957", {"start": v(-209.12, 69.14) * mm, "end": v(-140.46, 69.14) * mm});
            skArc(sketch, "E958", {"start": v(-139.83, 68.91) * mm, "mid": v(-140.12, 69.08) * mm, "end": v(-140.46, 69.14) * mm});
            skArc(sketch, "E959", {"start": v(-139.83, 68.91) * mm, "mid": v(-135.34, 69.14) * mm, "end": v(-135.12, 73.62) * mm});
            skArc(sketch, "E960", {"start": v(-135.35, 74.25) * mm, "mid": v(-135.29, 73.92) * mm, "end": v(-135.12, 73.62) * mm});
            skLineSegment(sketch, "E961", {"start": v(-135.35, 74.25) * mm, "end": v(-135.35, 88.22) * mm});
            skLineSegment(sketch, "E962", {"start": v(-135.35, 88.22) * mm, "end": v(-122.88, 100.69) * mm});
            skLineSegment(sketch, "E963", {"start": v(-122.88, 100.69) * mm, "end": v(-109.37, 100.69) * mm});
            skLineSegment(sketch, "E964", {"start": v(-109.37, 100.69) * mm, "end": v(-96.9, 88.22) * mm});
            skLineSegment(sketch, "E965", {"start": v(-96.9, 88.22) * mm, "end": v(-96.9, 74.25) * mm});
            skArc(sketch, "E966", {"start": v(-97.13, 73.62) * mm, "mid": v(-96.96, 73.92) * mm, "end": v(-96.9, 74.25) * mm});
            skArc(sketch, "E967", {"start": v(-97.13, 73.62) * mm, "mid": v(-96.9, 69.14) * mm, "end": v(-92.42, 68.91) * mm});
            skArc(sketch, "E968", {"start": v(-91.8, 69.14) * mm, "mid": v(-92.13, 69.08) * mm, "end": v(-92.42, 68.91) * mm});
            skLineSegment(sketch, "E969", {"start": v(-91.8, 69.14) * mm, "end": v(-23.13, 69.14) * mm});
            skLineSegment(sketch, "E970", {"start": v(-23.12, 69.14) * mm, "end": v(-23.12, 56.04) * mm});
            skArc(sketch, "E971", {"start": v(-61.12, 18.04) * mm, "mid": v(-88, 6.9) * mm, "end": v(-99.12, -19.96) * mm});
            skArc(sketch, "E972", {"start": v(-61.12, 18.04) * mm, "mid": v(-34.25, 29.17) * mm, "end": v(-23.12, 56.04) * mm});
            skLineSegment(sketch, "E973", {"start": v(-99.12, -201.76) * mm, "end": v(-99.12, -19.96) * mm});
            skArc(sketch, "E974", {"start": v(-23.12, -277.76) * mm, "mid": v(-34.25, -250.9) * mm, "end": v(-61.12, -239.76) * mm});
            skArc(sketch, "E975", {"start": v(-99.12, -201.76) * mm, "mid": v(-88, -228.63) * mm, "end": v(-61.12, -239.76) * mm});
            skLineSegment(sketch, "E976", {"start": v(-23.12, -290.86) * mm, "end": v(-23.12, -277.76) * mm});
            skLineSegment(sketch, "E977", {"start": v(-91.8, -290.86) * mm, "end": v(-23.13, -290.86) * mm});
            skArc(sketch, "E978", {"start": v(-92.42, -290.64) * mm, "mid": v(-92.13, -290.8) * mm, "end": v(-91.8, -290.86) * mm});
            skArc(sketch, "E979", {"start": v(-92.42, -290.64) * mm, "mid": v(-96.9, -290.86) * mm, "end": v(-97.13, -295.34) * mm});
            skArc(sketch, "E980", {"start": v(-96.9, -295.98) * mm, "mid": v(-96.96, -295.64) * mm, "end": v(-97.13, -295.34) * mm});
            skLineSegment(sketch, "E981", {"start": v(-96.9, -309.95) * mm, "end": v(-96.9, -295.98) * mm});
            skLineSegment(sketch, "E982", {"start": v(-109.37, -322.41) * mm, "end": v(-96.9, -309.95) * mm});
            skLineSegment(sketch, "E983", {"start": v(-122.88, -322.41) * mm, "end": v(-109.37, -322.41) * mm});
            skLineSegment(sketch, "E984", {"start": v(-135.35, -309.95) * mm, "end": v(-122.88, -322.41) * mm});
            skArc(sketch, "E985", {"start": v(-135.12, -295.34) * mm, "mid": v(-135.29, -295.64) * mm, "end": v(-135.35, -295.98) * mm});
            skLineSegment(sketch, "E986", {"start": v(-135.35, -295.98) * mm, "end": v(-135.35, -309.95) * mm});
            skArc(sketch, "E987", {"start": v(-140.46, -290.86) * mm, "mid": v(-140.12, -290.8) * mm, "end": v(-139.83, -290.64) * mm});
            skLineSegment(sketch, "E988", {"start": v(-209.12, -290.86) * mm, "end": v(-140.46, -290.86) * mm});
            skLineSegment(sketch, "E989", {"start": v(-209.12, -277.76) * mm, "end": v(-209.12, -290.86) * mm});
            skArc(sketch, "E990", {"start": v(-209.12, -277.76) * mm, "mid": v(-211.18, -272.81) * mm, "end": v(-216.12, -270.76) * mm});
            skArc(sketch, "E991", {"start": v(-223.13, -263.76) * mm, "mid": v(-221.07, -268.71) * mm, "end": v(-216.12, -270.76) * mm});
            skLineSegment(sketch, "E992", {"start": v(-223.13, 42.04) * mm, "end": v(-223.13, -263.76) * mm});
            skArc(sketch, "E993", {"start": v(-216.12, 49.04) * mm, "mid": v(-221.07, 46.99) * mm, "end": v(-223.13, 42.04) * mm});
            skArc(sketch, "E994", {"start": v(-216.12, 49.04) * mm, "mid": v(-211.18, 51.09) * mm, "end": v(-209.12, 56.04) * mm});
            skArc(sketch, "E995", {"start": v(-114.23, -309.82) * mm, "mid": v(-109.6, -309.71) * mm, "end": v(-109.5, -305.1) * mm});
            skArc(sketch, "E996", {"start": v(-109.6, -304.82) * mm, "mid": v(-109.58, -304.97) * mm, "end": v(-109.5, -305.1) * mm});
            skLineSegment(sketch, "E997", {"start": v(-109.6, -304.82) * mm, "end": v(-109.6, -301.1) * mm});
            skArc(sketch, "E998", {"start": v(-109.5, -300.83) * mm, "mid": v(-109.6, -296.21) * mm, "end": v(-114.23, -296.1) * mm});
            skArc(sketch, "E999", {"start": v(-109.5, -300.83) * mm, "mid": v(-109.58, -300.96) * mm, "end": v(-109.6, -301.1) * mm});
            skArc(sketch, "E1000", {"start": v(-114.5, -296.21) * mm, "mid": v(-114.35, -296.19) * mm, "end": v(-114.23, -296.1) * mm});
            skLineSegment(sketch, "E1001", {"start": v(-114.5, -296.21) * mm, "end": v(-117.75, -296.21) * mm});
            skArc(sketch, "E1002", {"start": v(-118.02, -296.1) * mm, "mid": v(-117.9, -296.19) * mm, "end": v(-117.75, -296.21) * mm});
            skArc(sketch, "E1003", {"start": v(-118.02, -296.1) * mm, "mid": v(-122.65, -296.21) * mm, "end": v(-122.75, -300.83) * mm});
            skArc(sketch, "E1004", {"start": v(-122.65, -301.1) * mm, "mid": v(-122.67, -300.96) * mm, "end": v(-122.75, -300.83) * mm});
            skLineSegment(sketch, "E1005", {"start": v(-122.64, -301.1) * mm, "end": v(-122.64, -304.82) * mm});
            skArc(sketch, "E1006", {"start": v(-122.75, -305.1) * mm, "mid": v(-122.67, -304.97) * mm, "end": v(-122.65, -304.82) * mm});
            skArc(sketch, "E1007", {"start": v(-122.75, -305.1) * mm, "mid": v(-122.65, -309.71) * mm, "end": v(-118.02, -309.82) * mm});
            skArc(sketch, "E1008", {"start": v(-117.75, -309.71) * mm, "mid": v(-117.9, -309.74) * mm, "end": v(-118.02, -309.82) * mm});
            skLineSegment(sketch, "E1009", {"start": v(-117.75, -309.71) * mm, "end": v(-114.5, -309.71) * mm});
            skLineSegment(sketch, "E1010", {"start": v(-122.64, 79.38) * mm, "end": v(-122.64, 83.1) * mm});
            skArc(sketch, "E1011", {"start": v(-122.75, 79.1) * mm, "mid": v(-122.67, 79.23) * mm, "end": v(-122.65, 79.38) * mm});
            skArc(sketch, "E1012", {"start": v(-122.75, 79.1) * mm, "mid": v(-122.65, 74.49) * mm, "end": v(-118.02, 74.38) * mm});
            skArc(sketch, "E1013", {"start": v(-117.75, 74.49) * mm, "mid": v(-117.9, 74.46) * mm, "end": v(-118.02, 74.38) * mm});
            skLineSegment(sketch, "E1014", {"start": v(-114.5, 74.49) * mm, "end": v(-117.75, 74.49) * mm});
            skArc(sketch, "E1015", {"start": v(-114.23, 74.38) * mm, "mid": v(-114.35, 74.46) * mm, "end": v(-114.5, 74.49) * mm});
            skArc(sketch, "E1016", {"start": v(-114.23, 74.38) * mm, "mid": v(-109.6, 74.49) * mm, "end": v(-109.5, 79.1) * mm});
            skArc(sketch, "E1017", {"start": v(-109.6, 79.38) * mm, "mid": v(-109.58, 79.23) * mm, "end": v(-109.5, 79.1) * mm});
            skLineSegment(sketch, "E1018", {"start": v(-109.6, 83.1) * mm, "end": v(-109.6, 79.38) * mm});
            skArc(sketch, "E1019", {"start": v(-109.5, 83.37) * mm, "mid": v(-109.58, 83.24) * mm, "end": v(-109.6, 83.1) * mm});
            skArc(sketch, "E1020", {"start": v(-109.5, 83.37) * mm, "mid": v(-109.6, 87.99) * mm, "end": v(-114.23, 88.1) * mm});
            skArc(sketch, "E1021", {"start": v(-114.5, 87.99) * mm, "mid": v(-114.35, 88.01) * mm, "end": v(-114.23, 88.1) * mm});
            skLineSegment(sketch, "E1022", {"start": v(-117.75, 87.99) * mm, "end": v(-114.5, 87.99) * mm});
            skArc(sketch, "E1023", {"start": v(-118.02, 88.1) * mm, "mid": v(-117.9, 88.01) * mm, "end": v(-117.75, 87.99) * mm});
            skArc(sketch, "E1024", {"start": v(-118.02, 88.1) * mm, "mid": v(-122.65, 87.99) * mm, "end": v(-122.75, 83.37) * mm});
            skArc(sketch, "E1025", {"start": v(-316.57, 69.3) * mm, "mid": v(-316.23, 69.37) * mm, "end": v(-315.93, 69.53) * mm});
            skArc(sketch, "E1026", {"start": v(-311.45, -285.92) * mm, "mid": v(-311.4, -286.25) * mm, "end": v(-311.23, -286.55) * mm});
            skLineSegment(sketch, "E1027", {"start": v(-269.84, -277.76) * mm, "end": v(-269.84, -290.86) * mm});
            skArc(sketch, "E1028", {"start": v(-311.23, -282.47) * mm, "mid": v(-311.4, -282.77) * mm, "end": v(-311.45, -283.1) * mm});
            skLineSegment(sketch, "E1029", {"start": v(-311.45, -283.1) * mm, "end": v(-311.45, -285.92) * mm});
            skArc(sketch, "E1030", {"start": v(-311.23, -282.47) * mm, "mid": v(-311.45, -278) * mm, "end": v(-315.93, -277.77) * mm});
            skArc(sketch, "E1031", {"start": v(-316.57, -278) * mm, "mid": v(-316.23, -277.93) * mm, "end": v(-315.93, -277.77) * mm});
            skArc(sketch, "E1032", {"start": v(-345.75, -277.77) * mm, "mid": v(-350.23, -278) * mm, "end": v(-350.46, -282.47) * mm});
            skLineSegment(sketch, "E1033", {"start": v(-345.12, -278) * mm, "end": v(-316.57, -278) * mm});
            skArc(sketch, "E1034", {"start": v(-345.75, -277.77) * mm, "mid": v(-345.46, -277.93) * mm, "end": v(-345.12, -278) * mm});
            skArc(sketch, "E1035", {"start": v(-350.23, -283.1) * mm, "mid": v(-350.3, -282.77) * mm, "end": v(-350.46, -282.47) * mm});
            skLineSegment(sketch, "E1036", {"start": v(-350.23, -285.92) * mm, "end": v(-350.23, -283.1) * mm});
            skArc(sketch, "E1037", {"start": v(-350.46, -286.55) * mm, "mid": v(-350.23, -291.03) * mm, "end": v(-345.75, -291.26) * mm});
            skArc(sketch, "E1038", {"start": v(-350.46, -286.55) * mm, "mid": v(-350.3, -286.25) * mm, "end": v(-350.23, -285.92) * mm});
            skArc(sketch, "E1039", {"start": v(-345.12, -291.03) * mm, "mid": v(-345.46, -291.1) * mm, "end": v(-345.75, -291.26) * mm});
            skLineSegment(sketch, "E1040", {"start": v(-316.57, -291.03) * mm, "end": v(-345.12, -291.03) * mm});
            skArc(sketch, "E1041", {"start": v(-315.93, -291.26) * mm, "mid": v(-316.23, -291.1) * mm, "end": v(-316.57, -291.03) * mm});
            skArc(sketch, "E1042", {"start": v(-315.93, -291.26) * mm, "mid": v(-311.45, -291.03) * mm, "end": v(-311.23, -286.55) * mm});
            skLineSegment(sketch, "E1043", {"start": v(-269.84, -290.86) * mm, "end": v(-293.64, -290.86) * mm});
            skArc(sketch, "E1044", {"start": v(-294.27, -290.64) * mm, "mid": v(-293.98, -290.8) * mm, "end": v(-293.64, -290.86) * mm});
            skArc(sketch, "E1045", {"start": v(-294.27, -290.64) * mm, "mid": v(-298.75, -290.86) * mm, "end": v(-298.98, -295.34) * mm});
            skArc(sketch, "E1046", {"start": v(-298.75, -295.98) * mm, "mid": v(-298.81, -295.64) * mm, "end": v(-298.98, -295.34) * mm});
            skLineSegment(sketch, "E1047", {"start": v(-298.75, -295.98) * mm, "end": v(-298.75, -299.77) * mm});
            skLineSegment(sketch, "E1048", {"start": v(-298.75, -299.77) * mm, "end": v(-302.55, -303.56) * mm});
            skLineSegment(sketch, "E1049", {"start": v(-302.55, -303.56) * mm, "end": v(-359.14, -303.56) * mm});
            skLineSegment(sketch, "E1050", {"start": v(-359.14, -303.56) * mm, "end": v(-362.93, -299.77) * mm});
            skLineSegment(sketch, "E1051", {"start": v(-362.93, -299.77) * mm, "end": v(-362.93, -295.98) * mm});
            skArc(sketch, "E1052", {"start": v(-362.7, -295.34) * mm, "mid": v(-362.88, -295.64) * mm, "end": v(-362.93, -295.98) * mm});
            skArc(sketch, "E1053", {"start": v(-362.7, -295.34) * mm, "mid": v(-362.93, -290.86) * mm, "end": v(-367.41, -290.64) * mm});
            skArc(sketch, "E1054", {"start": v(-311.23, 64.83) * mm, "mid": v(-311.45, 69.3) * mm, "end": v(-315.93, 69.53) * mm});
            skArc(sketch, "E1055", {"start": v(-368.05, -290.86) * mm, "mid": v(-367.71, -290.8) * mm, "end": v(-367.41, -290.64) * mm});
            skLineSegment(sketch, "E1056", {"start": v(-368.05, -290.86) * mm, "end": v(-405.84, -290.86) * mm});
            skLineSegment(sketch, "E1057", {"start": v(-405.84, -290.86) * mm, "end": v(-405.84, -278.16) * mm});
            skArc(sketch, "E1058", {"start": v(-398.84, -271.16) * mm, "mid": v(-403.8, -273.21) * mm, "end": v(-405.84, -278.16) * mm});
            skArc(sketch, "E1059", {"start": v(-398.84, -271.16) * mm, "mid": v(-393.9, -269.11) * mm, "end": v(-391.84, -264.16) * mm});
            skLineSegment(sketch, "E1060", {"start": v(-391.84, 42.44) * mm, "end": v(-391.84, -264.16) * mm});
            skArc(sketch, "E1061", {"start": v(-391.84, 42.44) * mm, "mid": v(-393.9, 47.39) * mm, "end": v(-398.84, 49.44) * mm});
            skArc(sketch, "E1062", {"start": v(-405.84, 56.44) * mm, "mid": v(-403.8, 51.49) * mm, "end": v(-398.84, 49.44) * mm});
            skLineSegment(sketch, "E1063", {"start": v(-405.84, 69.14) * mm, "end": v(-405.84, 56.44) * mm});
            skLineSegment(sketch, "E1064", {"start": v(-368.05, 69.14) * mm, "end": v(-405.84, 69.14) * mm});
            skArc(sketch, "E1065", {"start": v(-367.41, 68.91) * mm, "mid": v(-367.71, 69.08) * mm, "end": v(-368.05, 69.14) * mm});
            skArc(sketch, "E1066", {"start": v(-367.41, 68.91) * mm, "mid": v(-362.93, 69.14) * mm, "end": v(-362.7, 73.62) * mm});
            skArc(sketch, "E1067", {"start": v(-362.93, 74.25) * mm, "mid": v(-362.88, 73.92) * mm, "end": v(-362.7, 73.62) * mm});
            skLineSegment(sketch, "E1068", {"start": v(-362.93, 78.04) * mm, "end": v(-362.93, 74.25) * mm});
            skLineSegment(sketch, "E1069", {"start": v(-359.14, 81.84) * mm, "end": v(-362.93, 78.04) * mm});
            skLineSegment(sketch, "E1070", {"start": v(-302.55, 81.84) * mm, "end": v(-359.14, 81.84) * mm});
            skLineSegment(sketch, "E1071", {"start": v(-298.75, 78.04) * mm, "end": v(-302.55, 81.84) * mm});
            skLineSegment(sketch, "E1072", {"start": v(-298.75, 74.25) * mm, "end": v(-298.75, 78.04) * mm});
            skArc(sketch, "E1073", {"start": v(-298.98, 73.62) * mm, "mid": v(-298.81, 73.92) * mm, "end": v(-298.75, 74.25) * mm});
            skArc(sketch, "E1074", {"start": v(-298.98, 73.62) * mm, "mid": v(-298.75, 69.14) * mm, "end": v(-294.27, 68.91) * mm});
            skArc(sketch, "E1075", {"start": v(-293.64, 69.14) * mm, "mid": v(-293.98, 69.08) * mm, "end": v(-294.27, 68.91) * mm});
            skLineSegment(sketch, "E1076", {"start": v(-269.84, 69.14) * mm, "end": v(-293.64, 69.14) * mm});
            skLineSegment(sketch, "E1077", {"start": v(-269.84, 56.04) * mm, "end": v(-269.84, 69.14) * mm});
            skArc(sketch, "E1078", {"start": v(-269.84, 56.04) * mm, "mid": v(-267.8, 51.09) * mm, "end": v(-262.84, 49.04) * mm});
            skArc(sketch, "E1079", {"start": v(-255.84, 42.04) * mm, "mid": v(-257.9, 46.99) * mm, "end": v(-262.84, 49.04) * mm});
            skLineSegment(sketch, "E1080", {"start": v(-255.84, -263.76) * mm, "end": v(-255.84, 42.04) * mm});
            skArc(sketch, "E1081", {"start": v(-262.84, -270.76) * mm, "mid": v(-257.9, -268.71) * mm, "end": v(-255.84, -263.76) * mm});
            skArc(sketch, "E1082", {"start": v(-262.84, -270.76) * mm, "mid": v(-267.8, -272.81) * mm, "end": v(-269.84, -277.76) * mm});
            skLineSegment(sketch, "E1083", {"start": v(-316.57, 69.3) * mm, "end": v(-345.12, 69.3) * mm});
            skArc(sketch, "E1084", {"start": v(-345.75, 69.53) * mm, "mid": v(-345.46, 69.37) * mm, "end": v(-345.12, 69.3) * mm});
            skArc(sketch, "E1085", {"start": v(-345.75, 69.53) * mm, "mid": v(-350.23, 69.3) * mm, "end": v(-350.46, 64.83) * mm});
            skArc(sketch, "E1086", {"start": v(-350.23, 64.2) * mm, "mid": v(-350.3, 64.53) * mm, "end": v(-350.46, 64.83) * mm});
            skLineSegment(sketch, "E1087", {"start": v(-350.23, 64.2) * mm, "end": v(-350.23, 61.38) * mm});
            skArc(sketch, "E1088", {"start": v(-350.46, 60.75) * mm, "mid": v(-350.3, 61.05) * mm, "end": v(-350.23, 61.38) * mm});
            skArc(sketch, "E1089", {"start": v(-350.46, 60.75) * mm, "mid": v(-350.23, 56.27) * mm, "end": v(-345.75, 56.04) * mm});
            skArc(sketch, "E1090", {"start": v(-345.12, 56.27) * mm, "mid": v(-345.46, 56.2) * mm, "end": v(-345.75, 56.04) * mm});
            skLineSegment(sketch, "E1091", {"start": v(-345.12, 56.27) * mm, "end": v(-316.57, 56.27) * mm});
            skArc(sketch, "E1092", {"start": v(-315.93, 56.04) * mm, "mid": v(-316.23, 56.2) * mm, "end": v(-316.57, 56.27) * mm});
            skArc(sketch, "E1093", {"start": v(-315.93, 56.04) * mm, "mid": v(-311.45, 56.27) * mm, "end": v(-311.23, 60.75) * mm});
            skArc(sketch, "E1094", {"start": v(-311.45, 61.38) * mm, "mid": v(-311.4, 61.05) * mm, "end": v(-311.23, 60.75) * mm});
            skArc(sketch, "E1095", {"start": v(-311.23, 64.83) * mm, "mid": v(-311.4, 64.53) * mm, "end": v(-311.45, 64.2) * mm});
            skLineSegment(sketch, "E1096", {"start": v(-311.45, 61.38) * mm, "end": v(-311.45, 64.2) * mm});
            skArc(sketch, "E1097", {"start": v(-527.84, -291.03) * mm, "mid": v(-528.17, -291.1) * mm, "end": v(-528.47, -291.26) * mm});
            skArc(sketch, "E1098", {"start": v(-532.95, 64.2) * mm, "mid": v(-533.01, 64.53) * mm, "end": v(-533.18, 64.83) * mm});
            skLineSegment(sketch, "E1099", {"start": v(-574.56, 56.04) * mm, "end": v(-574.56, 69.14) * mm});
            skLineSegment(sketch, "E1100", {"start": v(-532.95, 61.38) * mm, "end": v(-532.95, 64.2) * mm});
            skArc(sketch, "E1101", {"start": v(-533.18, 60.75) * mm, "mid": v(-533.01, 61.05) * mm, "end": v(-532.95, 61.38) * mm});
            skArc(sketch, "E1102", {"start": v(-533.18, -286.55) * mm, "mid": v(-532.95, -291.03) * mm, "end": v(-528.47, -291.26) * mm});
            skArc(sketch, "E1103", {"start": v(-533.18, 60.75) * mm, "mid": v(-532.95, 56.27) * mm, "end": v(-528.47, 56.04) * mm});
            skArc(sketch, "E1104", {"start": v(-527.84, 56.27) * mm, "mid": v(-528.17, 56.2) * mm, "end": v(-528.47, 56.04) * mm});
            skLineSegment(sketch, "E1105", {"start": v(-499.29, 56.27) * mm, "end": v(-527.84, 56.27) * mm});
            skArc(sketch, "E1106", {"start": v(-498.65, 56.04) * mm, "mid": v(-498.95, 56.2) * mm, "end": v(-499.29, 56.27) * mm});
            skArc(sketch, "E1107", {"start": v(-498.65, 56.04) * mm, "mid": v(-494.17, 56.27) * mm, "end": v(-493.95, 60.75) * mm});
            skArc(sketch, "E1108", {"start": v(-494.17, 61.38) * mm, "mid": v(-494.11, 61.05) * mm, "end": v(-493.95, 60.75) * mm});
            skArc(sketch, "E1109", {"start": v(-493.95, 64.83) * mm, "mid": v(-494.11, 64.53) * mm, "end": v(-494.17, 64.2) * mm});
            skLineSegment(sketch, "E1110", {"start": v(-494.17, 64.2) * mm, "end": v(-494.17, 61.38) * mm});
            skArc(sketch, "E1111", {"start": v(-493.95, 64.83) * mm, "mid": v(-494.17, 69.3) * mm, "end": v(-498.65, 69.53) * mm});
            skArc(sketch, "E1112", {"start": v(-499.29, 69.3) * mm, "mid": v(-498.95, 69.37) * mm, "end": v(-498.65, 69.53) * mm});
            skLineSegment(sketch, "E1113", {"start": v(-527.84, 69.3) * mm, "end": v(-499.29, 69.3) * mm});
            skArc(sketch, "E1114", {"start": v(-528.47, 69.53) * mm, "mid": v(-528.17, 69.37) * mm, "end": v(-527.84, 69.3) * mm});
            skArc(sketch, "E1115", {"start": v(-528.47, 69.53) * mm, "mid": v(-532.95, 69.3) * mm, "end": v(-533.18, 64.83) * mm});
            skArc(sketch, "E1116", {"start": v(-550.13, 68.91) * mm, "mid": v(-550.43, 69.08) * mm, "end": v(-550.77, 69.14) * mm});
            skLineSegment(sketch, "E1117", {"start": v(-574.56, 69.14) * mm, "end": v(-550.77, 69.14) * mm});
            skArc(sketch, "E1118", {"start": v(-550.13, 68.91) * mm, "mid": v(-545.65, 69.14) * mm, "end": v(-545.43, 73.62) * mm});
            skArc(sketch, "E1119", {"start": v(-545.65, 74.25) * mm, "mid": v(-545.6, 73.92) * mm, "end": v(-545.43, 73.62) * mm});
            skLineSegment(sketch, "E1120", {"start": v(-545.65, 74.25) * mm, "end": v(-545.65, 78.04) * mm});
            skLineSegment(sketch, "E1121", {"start": v(-545.65, 78.04) * mm, "end": v(-541.86, 81.84) * mm});
            skLineSegment(sketch, "E1122", {"start": v(-541.86, 81.84) * mm, "end": v(-485.27, 81.84) * mm});
            skLineSegment(sketch, "E1123", {"start": v(-485.27, 81.84) * mm, "end": v(-481.47, 78.04) * mm});
            skLineSegment(sketch, "E1124", {"start": v(-481.47, 78.04) * mm, "end": v(-481.47, 74.25) * mm});
            skArc(sketch, "E1125", {"start": v(-481.7, 73.62) * mm, "mid": v(-481.53, 73.92) * mm, "end": v(-481.47, 74.25) * mm});
            skArc(sketch, "E1126", {"start": v(-481.7, 73.62) * mm, "mid": v(-481.47, 69.14) * mm, "end": v(-477, 68.91) * mm});
            skArc(sketch, "E1127", {"start": v(-476.36, 69.14) * mm, "mid": v(-476.7, 69.08) * mm, "end": v(-477, 68.91) * mm});
            skLineSegment(sketch, "E1128", {"start": v(-476.36, 69.14) * mm, "end": v(-438.56, 69.14) * mm});
            skLineSegment(sketch, "E1129", {"start": v(-438.56, 69.14) * mm, "end": v(-438.56, 56.44) * mm});
            skArc(sketch, "E1130", {"start": v(-445.56, 49.44) * mm, "mid": v(-440.61, 51.49) * mm, "end": v(-438.56, 56.44) * mm});
            skArc(sketch, "E1131", {"start": v(-445.56, 49.44) * mm, "mid": v(-450.51, 47.39) * mm, "end": v(-452.56, 42.44) * mm});
            skLineSegment(sketch, "E1132", {"start": v(-452.56, -264.16) * mm, "end": v(-452.56, 42.44) * mm});
            skArc(sketch, "E1133", {"start": v(-452.56, -264.16) * mm, "mid": v(-450.51, -269.11) * mm, "end": v(-445.56, -271.16) * mm});
            skArc(sketch, "E1134", {"start": v(-438.56, -278.16) * mm, "mid": v(-440.61, -273.21) * mm, "end": v(-445.56, -271.16) * mm});
            skLineSegment(sketch, "E1135", {"start": v(-438.56, -290.86) * mm, "end": v(-438.56, -278.16) * mm});
            skLineSegment(sketch, "E1136", {"start": v(-476.36, -290.86) * mm, "end": v(-438.56, -290.86) * mm});
            skArc(sketch, "E1137", {"start": v(-477, -290.64) * mm, "mid": v(-476.7, -290.8) * mm, "end": v(-476.36, -290.86) * mm});
            skArc(sketch, "E1138", {"start": v(-477, -290.64) * mm, "mid": v(-481.47, -290.86) * mm, "end": v(-481.7, -295.34) * mm});
            skArc(sketch, "E1139", {"start": v(-481.47, -295.98) * mm, "mid": v(-481.53, -295.64) * mm, "end": v(-481.7, -295.34) * mm});
            skLineSegment(sketch, "E1140", {"start": v(-481.47, -299.77) * mm, "end": v(-481.47, -295.98) * mm});
            skLineSegment(sketch, "E1141", {"start": v(-485.27, -303.56) * mm, "end": v(-481.47, -299.77) * mm});
            skLineSegment(sketch, "E1142", {"start": v(-541.86, -303.56) * mm, "end": v(-485.27, -303.56) * mm});
            skLineSegment(sketch, "E1143", {"start": v(-545.65, -299.77) * mm, "end": v(-541.86, -303.56) * mm});
            skLineSegment(sketch, "E1144", {"start": v(-545.65, -295.98) * mm, "end": v(-545.65, -299.77) * mm});
            skArc(sketch, "E1145", {"start": v(-545.43, -295.34) * mm, "mid": v(-545.6, -295.64) * mm, "end": v(-545.65, -295.98) * mm});
            skArc(sketch, "E1146", {"start": v(-545.43, -295.34) * mm, "mid": v(-545.65, -290.86) * mm, "end": v(-550.13, -290.64) * mm});
            skArc(sketch, "E1147", {"start": v(-550.77, -290.86) * mm, "mid": v(-550.43, -290.8) * mm, "end": v(-550.13, -290.64) * mm});
            skLineSegment(sketch, "E1148", {"start": v(-574.56, -290.86) * mm, "end": v(-550.77, -290.86) * mm});
            skLineSegment(sketch, "E1149", {"start": v(-574.56, -277.76) * mm, "end": v(-574.56, -290.86) * mm});
            skArc(sketch, "E1150", {"start": v(-588.56, -263.76) * mm, "mid": v(-586.51, -268.71) * mm, "end": v(-581.56, -270.76) * mm});
            skArc(sketch, "E1151", {"start": v(-574.56, -277.76) * mm, "mid": v(-576.61, -272.81) * mm, "end": v(-581.56, -270.76) * mm});
            skArc(sketch, "E1152", {"start": v(-581.56, 49.04) * mm, "mid": v(-586.51, 46.99) * mm, "end": v(-588.56, 42.04) * mm});
            skLineSegment(sketch, "E1153", {"start": v(-588.56, 42.04) * mm, "end": v(-588.56, -263.76) * mm});
            skArc(sketch, "E1154", {"start": v(-581.56, 49.04) * mm, "mid": v(-576.61, 51.09) * mm, "end": v(-574.56, 56.04) * mm});
            skLineSegment(sketch, "E1155", {"start": v(-527.84, -291.03) * mm, "end": v(-499.29, -291.03) * mm});
            skArc(sketch, "E1156", {"start": v(-498.65, -291.26) * mm, "mid": v(-498.95, -291.1) * mm, "end": v(-499.29, -291.03) * mm});
            skArc(sketch, "E1157", {"start": v(-498.65, -291.26) * mm, "mid": v(-494.17, -291.03) * mm, "end": v(-493.95, -286.55) * mm});
            skArc(sketch, "E1158", {"start": v(-494.17, -285.92) * mm, "mid": v(-494.11, -286.25) * mm, "end": v(-493.95, -286.55) * mm});
            skLineSegment(sketch, "E1159", {"start": v(-494.17, -285.92) * mm, "end": v(-494.17, -283.1) * mm});
            skArc(sketch, "E1160", {"start": v(-493.95, -282.47) * mm, "mid": v(-494.17, -278) * mm, "end": v(-498.65, -277.77) * mm});
            skArc(sketch, "E1161", {"start": v(-493.95, -282.47) * mm, "mid": v(-494.11, -282.77) * mm, "end": v(-494.17, -283.1) * mm});
            skArc(sketch, "E1162", {"start": v(-499.29, -278) * mm, "mid": v(-498.95, -277.93) * mm, "end": v(-498.65, -277.77) * mm});
            skLineSegment(sketch, "E1163", {"start": v(-499.29, -278) * mm, "end": v(-527.84, -278) * mm});
            skArc(sketch, "E1164", {"start": v(-528.47, -277.77) * mm, "mid": v(-528.17, -277.93) * mm, "end": v(-527.84, -278) * mm});
            skArc(sketch, "E1165", {"start": v(-528.47, -277.77) * mm, "mid": v(-532.95, -278) * mm, "end": v(-533.18, -282.47) * mm});
            skArc(sketch, "E1166", {"start": v(-532.95, -283.1) * mm, "mid": v(-533.01, -282.77) * mm, "end": v(-533.18, -282.47) * mm});
            skArc(sketch, "E1167", {"start": v(-533.18, -286.55) * mm, "mid": v(-533.01, -286.25) * mm, "end": v(-532.95, -285.92) * mm});
            skLineSegment(sketch, "E1168", {"start": v(-532.95, -283.1) * mm, "end": v(-532.95, -285.92) * mm});
            skArc(sketch, "E1169", {"start": v(-178.06, -446.98) * mm, "mid": v(-178.14, -447.1) * mm, "end": v(-178.16, -447.25) * mm});
            skArc(sketch, "E1170", {"start": v(-570.97, -455.4) * mm, "mid": v(-571.12, -455.42) * mm, "end": v(-571.24, -455.5) * mm});
            skLineSegment(sketch, "E1171", {"start": v(-342.58, -542.8) * mm, "end": v(-407.95, -551.88) * mm});
            skLineSegment(sketch, "E1172", {"start": v(-314.44, -565.85) * mm, "end": v(-318.99, -533.1) * mm});
            skArc(sketch, "E1173", {"start": v(-407.95, -551.88) * mm, "mid": v(-418.19, -565.41) * mm, "end": v(-404.65, -575.65) * mm});
            skLineSegment(sketch, "E1174", {"start": v(-404.65, -575.65) * mm, "end": v(-339.28, -566.57) * mm});
            skArc(sketch, "E1175", {"start": v(-339.28, -566.57) * mm, "mid": v(-329.04, -553.03) * mm, "end": v(-342.58, -542.8) * mm});
            skLineSegment(sketch, "E1176", {"start": v(-322.97, -577.13) * mm, "end": v(-314.44, -565.85) * mm});
            skLineSegment(sketch, "E1177", {"start": v(-417.46, -590.25) * mm, "end": v(-322.97, -577.13) * mm});
            skLineSegment(sketch, "E1178", {"start": v(-428.74, -581.72) * mm, "end": v(-417.46, -590.25) * mm});
            skLineSegment(sketch, "E1179", {"start": v(-433.3, -548.98) * mm, "end": v(-428.74, -581.72) * mm});
            skArc(sketch, "E1180", {"start": v(-433.3, -548.98) * mm, "mid": v(-430.58, -545.4) * mm, "end": v(-434.16, -542.7) * mm});
            skLineSegment(sketch, "E1181", {"start": v(-557.01, -559.76) * mm, "end": v(-434.16, -542.7) * mm});
            skLineSegment(sketch, "E1182", {"start": v(-557.01, -559.76) * mm, "end": v(-557.01, -473.3) * mm});
            skArc(sketch, "E1183", {"start": v(-556.74, -472.52) * mm, "mid": v(-556.94, -472.9) * mm, "end": v(-557.01, -473.3) * mm});
            skArc(sketch, "E1184", {"start": v(-556.74, -472.52) * mm, "mid": v(-557.01, -468.1) * mm, "end": v(-561.44, -467.83) * mm});
            skArc(sketch, "E1185", {"start": v(-562.22, -468.1) * mm, "mid": v(-561.8, -468.03) * mm, "end": v(-561.44, -467.83) * mm});
            skLineSegment(sketch, "E1186", {"start": v(-562.22, -468.1) * mm, "end": v(-576, -468.1) * mm});
            skLineSegment(sketch, "E1187", {"start": v(-576, -468.1) * mm, "end": v(-588.56, -455.54) * mm});
            skLineSegment(sketch, "E1188", {"start": v(-588.56, -455.54) * mm, "end": v(-588.56, -442.21) * mm});
            skLineSegment(sketch, "E1189", {"start": v(-588.56, -442.21) * mm, "end": v(-576, -429.66) * mm});
            skLineSegment(sketch, "E1190", {"start": v(-576, -429.66) * mm, "end": v(-562.22, -429.66) * mm});
            skArc(sketch, "E1191", {"start": v(-561.44, -429.93) * mm, "mid": v(-561.8, -429.73) * mm, "end": v(-562.22, -429.66) * mm});
            skArc(sketch, "E1192", {"start": v(-561.44, -429.93) * mm, "mid": v(-557.01, -429.66) * mm, "end": v(-556.74, -425.23) * mm});
            skArc(sketch, "E1193", {"start": v(-557.01, -424.45) * mm, "mid": v(-556.94, -424.86) * mm, "end": v(-556.74, -425.23) * mm});
            skLineSegment(sketch, "E1194", {"start": v(-557.01, -424.45) * mm, "end": v(-557.01, -388.88) * mm});
            skLineSegment(sketch, "E1195", {"start": v(-557.01, -388.88) * mm, "end": v(-544.31, -388.88) * mm});
            skArc(sketch, "E1196", {"start": v(-537.31, -395.88) * mm, "mid": v(-539.36, -390.93) * mm, "end": v(-544.31, -388.88) * mm});
            skArc(sketch, "E1197", {"start": v(-537.31, -395.88) * mm, "mid": v(-535.26, -400.83) * mm, "end": v(-530.31, -402.88) * mm});
            skLineSegment(sketch, "E1198", {"start": v(-223.71, -402.88) * mm, "end": v(-530.31, -402.88) * mm});
            skArc(sketch, "E1199", {"start": v(-223.71, -402.88) * mm, "mid": v(-218.76, -400.83) * mm, "end": v(-216.71, -395.88) * mm});
            skArc(sketch, "E1200", {"start": v(-209.71, -388.88) * mm, "mid": v(-214.66, -390.93) * mm, "end": v(-216.71, -395.88) * mm});
            skLineSegment(sketch, "E1201", {"start": v(-197.01, -388.88) * mm, "end": v(-209.71, -388.88) * mm});
            skLineSegment(sketch, "E1202", {"start": v(-197.01, -424.45) * mm, "end": v(-197.01, -388.88) * mm});
            skArc(sketch, "E1203", {"start": v(-197.28, -425.23) * mm, "mid": v(-197.08, -424.86) * mm, "end": v(-197.01, -424.45) * mm});
            skArc(sketch, "E1204", {"start": v(-197.28, -425.23) * mm, "mid": v(-197.01, -429.66) * mm, "end": v(-192.59, -429.93) * mm});
            skArc(sketch, "E1205", {"start": v(-191.8, -429.66) * mm, "mid": v(-192.22, -429.73) * mm, "end": v(-192.59, -429.93) * mm});
            skLineSegment(sketch, "E1206", {"start": v(-178.02, -429.66) * mm, "end": v(-191.8, -429.66) * mm});
            skLineSegment(sketch, "E1207", {"start": v(-165.46, -442.21) * mm, "end": v(-178.02, -429.66) * mm});
            skLineSegment(sketch, "E1208", {"start": v(-165.46, -455.54) * mm, "end": v(-165.46, -442.21) * mm});
            skLineSegment(sketch, "E1209", {"start": v(-178.02, -468.1) * mm, "end": v(-165.46, -455.54) * mm});
            skLineSegment(sketch, "E1210", {"start": v(-191.8, -468.1) * mm, "end": v(-178.02, -468.1) * mm});
            skArc(sketch, "E1211", {"start": v(-192.59, -467.83) * mm, "mid": v(-192.22, -468.03) * mm, "end": v(-191.8, -468.1) * mm});
            skArc(sketch, "E1212", {"start": v(-192.59, -467.83) * mm, "mid": v(-197.01, -468.1) * mm, "end": v(-197.28, -472.52) * mm});
            skArc(sketch, "E1213", {"start": v(-197.01, -473.3) * mm, "mid": v(-197.08, -472.9) * mm, "end": v(-197.28, -472.52) * mm});
            skLineSegment(sketch, "E1214", {"start": v(-197.01, -509.76) * mm, "end": v(-197.01, -473.3) * mm});
            skArc(sketch, "E1215", {"start": v(-319.86, -526.82) * mm, "mid": v(-322.57, -530.4) * mm, "end": v(-318.99, -533.1) * mm});
            skLineSegment(sketch, "E1216", {"start": v(-319.86, -526.82) * mm, "end": v(-197.01, -509.76) * mm});
            skArc(sketch, "E1217", {"start": v(-178.06, -446.98) * mm, "mid": v(-178.16, -442.36) * mm, "end": v(-182.78, -442.25) * mm});
            skArc(sketch, "E1218", {"start": v(-183.05, -442.36) * mm, "mid": v(-182.9, -442.33) * mm, "end": v(-182.78, -442.25) * mm});
            skLineSegment(sketch, "E1219", {"start": v(-183.05, -442.36) * mm, "end": v(-186.77, -442.36) * mm});
            skArc(sketch, "E1220", {"start": v(-187.04, -442.25) * mm, "mid": v(-186.92, -442.33) * mm, "end": v(-186.77, -442.36) * mm});
            skArc(sketch, "E1221", {"start": v(-187.04, -442.25) * mm, "mid": v(-191.66, -442.36) * mm, "end": v(-191.77, -446.98) * mm});
            skArc(sketch, "E1222", {"start": v(-191.66, -447.25) * mm, "mid": v(-191.69, -447.1) * mm, "end": v(-191.77, -446.98) * mm});
            skLineSegment(sketch, "E1223", {"start": v(-191.66, -447.25) * mm, "end": v(-191.66, -450.5) * mm});
            skArc(sketch, "E1224", {"start": v(-191.77, -450.77) * mm, "mid": v(-191.66, -455.4) * mm, "end": v(-187.04, -455.5) * mm});
            skArc(sketch, "E1225", {"start": v(-191.77, -450.77) * mm, "mid": v(-191.69, -450.65) * mm, "end": v(-191.66, -450.5) * mm});
            skArc(sketch, "E1226", {"start": v(-186.77, -455.4) * mm, "mid": v(-186.92, -455.42) * mm, "end": v(-187.04, -455.5) * mm});
            skLineSegment(sketch, "E1227", {"start": v(-186.77, -455.4) * mm, "end": v(-183.05, -455.4) * mm});
            skArc(sketch, "E1228", {"start": v(-182.78, -455.5) * mm, "mid": v(-182.9, -455.42) * mm, "end": v(-183.05, -455.4) * mm});
            skArc(sketch, "E1229", {"start": v(-182.78, -455.5) * mm, "mid": v(-178.16, -455.4) * mm, "end": v(-178.06, -450.77) * mm});
            skArc(sketch, "E1230", {"start": v(-178.16, -450.5) * mm, "mid": v(-178.14, -450.65) * mm, "end": v(-178.06, -450.77) * mm});
            skLineSegment(sketch, "E1231", {"start": v(-178.16, -450.5) * mm, "end": v(-178.16, -447.25) * mm});
            skLineSegment(sketch, "E1232", {"start": v(-567.25, -455.4) * mm, "end": v(-570.97, -455.4) * mm});
            skArc(sketch, "E1233", {"start": v(-566.98, -455.5) * mm, "mid": v(-567.1, -455.42) * mm, "end": v(-567.25, -455.4) * mm});
            skArc(sketch, "E1234", {"start": v(-566.98, -455.5) * mm, "mid": v(-562.36, -455.4) * mm, "end": v(-562.26, -450.77) * mm});
            skArc(sketch, "E1235", {"start": v(-562.36, -450.5) * mm, "mid": v(-562.34, -450.65) * mm, "end": v(-562.26, -450.77) * mm});
            skLineSegment(sketch, "E1236", {"start": v(-562.36, -447.25) * mm, "end": v(-562.36, -450.5) * mm});
            skArc(sketch, "E1237", {"start": v(-562.26, -446.98) * mm, "mid": v(-562.34, -447.1) * mm, "end": v(-562.36, -447.25) * mm});
            skArc(sketch, "E1238", {"start": v(-562.26, -446.98) * mm, "mid": v(-562.36, -442.36) * mm, "end": v(-566.98, -442.25) * mm});
            skArc(sketch, "E1239", {"start": v(-567.25, -442.36) * mm, "mid": v(-567.1, -442.33) * mm, "end": v(-566.98, -442.25) * mm});
            skLineSegment(sketch, "E1240", {"start": v(-570.97, -442.36) * mm, "end": v(-567.25, -442.36) * mm});
            skArc(sketch, "E1241", {"start": v(-571.24, -442.25) * mm, "mid": v(-571.12, -442.33) * mm, "end": v(-570.97, -442.36) * mm});
            skArc(sketch, "E1242", {"start": v(-571.24, -442.25) * mm, "mid": v(-575.86, -442.36) * mm, "end": v(-575.97, -446.98) * mm});
            skArc(sketch, "E1243", {"start": v(-575.86, -447.25) * mm, "mid": v(-575.89, -447.1) * mm, "end": v(-575.97, -446.98) * mm});
            skLineSegment(sketch, "E1244", {"start": v(-575.86, -450.5) * mm, "end": v(-575.86, -447.25) * mm});
            skArc(sketch, "E1245", {"start": v(-575.97, -450.77) * mm, "mid": v(-575.89, -450.65) * mm, "end": v(-575.86, -450.5) * mm});
            skArc(sketch, "E1246", {"start": v(-575.97, -450.77) * mm, "mid": v(-575.86, -455.4) * mm, "end": v(-571.24, -455.5) * mm});
            skArc(sketch, "E1247", {"start": v(-888.42, 92.6) * mm, "mid": v(-888.31, 87.99) * mm, "end": v(-883.7, 87.88) * mm});
            skArc(sketch, "E1248", {"start": v(-914.05, 101.95) * mm, "mid": v(-914.08, 102.1) * mm, "end": v(-914.16, 102.22) * mm});
            skLineSegment(sketch, "E1249", {"start": v(-968.53, 74.89) * mm, "end": v(-968.53, 87.99) * mm});
            skArc(sketch, "E1250", {"start": v(-905.63, -290.97) * mm, "mid": v(-905.76, -290.89) * mm, "end": v(-905.9, -290.86) * mm});
            skLineSegment(sketch, "E1251", {"start": v(-968.53, 87.99) * mm, "end": v(-931.64, 87.99) * mm});
            skArc(sketch, "E1252", {"start": v(-931.37, 87.88) * mm, "mid": v(-931.5, 87.96) * mm, "end": v(-931.64, 87.99) * mm});
            skArc(sketch, "E1253", {"start": v(-931.37, 87.88) * mm, "mid": v(-926.75, 87.99) * mm, "end": v(-926.65, 92.6) * mm});
            skArc(sketch, "E1254", {"start": v(-926.75, 92.88) * mm, "mid": v(-926.72, 92.73) * mm, "end": v(-926.65, 92.6) * mm});
            skLineSegment(sketch, "E1255", {"start": v(-926.75, 92.88) * mm, "end": v(-926.75, 107.3) * mm});
            skLineSegment(sketch, "E1256", {"start": v(-926.75, 107.3) * mm, "end": v(-914.51, 119.54) * mm});
            skLineSegment(sketch, "E1257", {"start": v(-914.51, 119.54) * mm, "end": v(-900.55, 119.54) * mm});
            skLineSegment(sketch, "E1258", {"start": v(-900.55, 119.54) * mm, "end": v(-888.31, 107.3) * mm});
            skLineSegment(sketch, "E1259", {"start": v(-888.31, 107.3) * mm, "end": v(-888.31, 92.88) * mm});
            skArc(sketch, "E1260", {"start": v(-888.42, 92.6) * mm, "mid": v(-888.34, 92.73) * mm, "end": v(-888.31, 92.88) * mm});
            skArc(sketch, "E1261", {"start": v(-883.42, 87.99) * mm, "mid": v(-883.57, 87.96) * mm, "end": v(-883.7, 87.88) * mm});
            skLineSegment(sketch, "E1262", {"start": v(-883.42, 87.99) * mm, "end": v(-832.53, 87.99) * mm});
            skLineSegment(sketch, "E1263", {"start": v(-832.53, 87.99) * mm, "end": v(-832.53, 75.29) * mm});
            skArc(sketch, "E1264", {"start": v(-839.53, 68.29) * mm, "mid": v(-834.58, 70.34) * mm, "end": v(-832.53, 75.29) * mm});
            skLineSegment(sketch, "E1265", {"start": v(-846.53, -245.31) * mm, "end": v(-846.53, 61.29) * mm});
            skArc(sketch, "E1266", {"start": v(-839.53, 68.29) * mm, "mid": v(-844.48, 66.24) * mm, "end": v(-846.53, 61.29) * mm});
            skArc(sketch, "E1267", {"start": v(-846.53, -245.31) * mm, "mid": v(-844.48, -250.26) * mm, "end": v(-839.53, -252.31) * mm});
            skArc(sketch, "E1268", {"start": v(-832.53, -259.31) * mm, "mid": v(-834.58, -254.36) * mm, "end": v(-839.53, -252.31) * mm});
            skLineSegment(sketch, "E1269", {"start": v(-832.53, -272.01) * mm, "end": v(-832.53, -259.31) * mm});
            skLineSegment(sketch, "E1270", {"start": v(-883.42, -272.01) * mm, "end": v(-832.53, -272.01) * mm});
            skArc(sketch, "E1271", {"start": v(-883.7, -271.9) * mm, "mid": v(-883.57, -271.99) * mm, "end": v(-883.42, -272.01) * mm});
            skArc(sketch, "E1272", {"start": v(-883.7, -271.9) * mm, "mid": v(-888.31, -272.01) * mm, "end": v(-888.42, -276.63) * mm});
            skArc(sketch, "E1273", {"start": v(-888.31, -276.9) * mm, "mid": v(-888.34, -276.76) * mm, "end": v(-888.42, -276.63) * mm});
            skLineSegment(sketch, "E1274", {"start": v(-888.31, -291.32) * mm, "end": v(-888.31, -276.9) * mm});
            skLineSegment(sketch, "E1275", {"start": v(-900.55, -303.56) * mm, "end": v(-888.31, -291.32) * mm});
            skLineSegment(sketch, "E1276", {"start": v(-914.51, -303.56) * mm, "end": v(-900.55, -303.56) * mm});
            skLineSegment(sketch, "E1277", {"start": v(-926.75, -291.32) * mm, "end": v(-914.51, -303.56) * mm});
            skLineSegment(sketch, "E1278", {"start": v(-926.75, -276.9) * mm, "end": v(-926.75, -291.32) * mm});
            skArc(sketch, "E1279", {"start": v(-926.65, -276.63) * mm, "mid": v(-926.72, -276.76) * mm, "end": v(-926.75, -276.9) * mm});
            skArc(sketch, "E1280", {"start": v(-926.65, -276.63) * mm, "mid": v(-926.75, -272.01) * mm, "end": v(-931.37, -271.9) * mm});
            skArc(sketch, "E1281", {"start": v(-931.64, -272.01) * mm, "mid": v(-931.5, -271.99) * mm, "end": v(-931.37, -271.9) * mm});
            skLineSegment(sketch, "E1282", {"start": v(-968.53, -272.01) * mm, "end": v(-931.64, -272.01) * mm});
            skLineSegment(sketch, "E1283", {"start": v(-968.53, -258.91) * mm, "end": v(-968.53, -272.01) * mm});
            skArc(sketch, "E1284", {"start": v(-968.53, -258.91) * mm, "mid": v(-970.58, -253.96) * mm, "end": v(-975.53, -251.91) * mm});
            skArc(sketch, "E1285", {"start": v(-982.53, -244.91) * mm, "mid": v(-980.48, -249.86) * mm, "end": v(-975.53, -251.91) * mm});
            skArc(sketch, "E1286", {"start": v(-975.53, 67.89) * mm, "mid": v(-980.48, 65.84) * mm, "end": v(-982.53, 60.89) * mm});
            skLineSegment(sketch, "E1287", {"start": v(-982.53, 60.89) * mm, "end": v(-982.53, -244.91) * mm});
            skArc(sketch, "E1288", {"start": v(-975.53, 67.89) * mm, "mid": v(-970.58, 69.94) * mm, "end": v(-968.53, 74.89) * mm});
            skArc(sketch, "E1289", {"start": v(-905.63, 93.23) * mm, "mid": v(-905.76, 93.31) * mm, "end": v(-905.9, 93.34) * mm});
            skArc(sketch, "E1290", {"start": v(-905.63, -290.97) * mm, "mid": v(-901.01, -290.86) * mm, "end": v(-900.9, -286.24) * mm});
            skArc(sketch, "E1291", {"start": v(-901.01, -285.97) * mm, "mid": v(-900.98, -286.12) * mm, "end": v(-900.9, -286.24) * mm});
            skLineSegment(sketch, "E1292", {"start": v(-901.01, -285.97) * mm, "end": v(-901.01, -282.25) * mm});
            skArc(sketch, "E1293", {"start": v(-900.9, -281.98) * mm, "mid": v(-900.98, -282.1) * mm, "end": v(-901.01, -282.25) * mm});
            skArc(sketch, "E1294", {"start": v(-900.9, -281.98) * mm, "mid": v(-901.01, -277.36) * mm, "end": v(-905.63, -277.26) * mm});
            skArc(sketch, "E1295", {"start": v(-905.9, -277.36) * mm, "mid": v(-905.76, -277.34) * mm, "end": v(-905.63, -277.26) * mm});
            skLineSegment(sketch, "E1296", {"start": v(-905.9, -277.36) * mm, "end": v(-909.16, -277.36) * mm});
            skArc(sketch, "E1297", {"start": v(-909.43, -277.26) * mm, "mid": v(-914.05, -277.36) * mm, "end": v(-914.16, -281.98) * mm});
            skArc(sketch, "E1298", {"start": v(-909.43, -277.26) * mm, "mid": v(-909.3, -277.34) * mm, "end": v(-909.16, -277.36) * mm});
            skArc(sketch, "E1299", {"start": v(-914.05, -282.25) * mm, "mid": v(-914.08, -282.1) * mm, "end": v(-914.16, -281.98) * mm});
            skArc(sketch, "E1300", {"start": v(-914.16, -286.24) * mm, "mid": v(-914.08, -286.12) * mm, "end": v(-914.05, -285.97) * mm});
            skLineSegment(sketch, "E1301", {"start": v(-914.05, -282.25) * mm, "end": v(-914.05, -285.97) * mm});
            skArc(sketch, "E1302", {"start": v(-914.16, -286.24) * mm, "mid": v(-914.05, -290.86) * mm, "end": v(-909.43, -290.97) * mm});
            skArc(sketch, "E1303", {"start": v(-909.16, -290.86) * mm, "mid": v(-909.3, -290.89) * mm, "end": v(-909.43, -290.97) * mm});
            skLineSegment(sketch, "E1304", {"start": v(-909.16, -290.86) * mm, "end": v(-905.9, -290.86) * mm});
            skLineSegment(sketch, "E1305", {"start": v(-914.05, 98.23) * mm, "end": v(-914.05, 101.95) * mm});
            skArc(sketch, "E1306", {"start": v(-914.16, 97.96) * mm, "mid": v(-914.08, 98.08) * mm, "end": v(-914.05, 98.23) * mm});
            skArc(sketch, "E1307", {"start": v(-914.16, 97.96) * mm, "mid": v(-914.05, 93.34) * mm, "end": v(-909.43, 93.23) * mm});
            skArc(sketch, "E1308", {"start": v(-909.16, 93.34) * mm, "mid": v(-909.3, 93.31) * mm, "end": v(-909.43, 93.23) * mm});
            skLineSegment(sketch, "E1309", {"start": v(-905.9, 93.34) * mm, "end": v(-909.16, 93.34) * mm});
            skArc(sketch, "E1310", {"start": v(-905.63, 93.23) * mm, "mid": v(-901.01, 93.34) * mm, "end": v(-900.9, 97.96) * mm});
            skArc(sketch, "E1311", {"start": v(-901.01, 98.23) * mm, "mid": v(-900.98, 98.08) * mm, "end": v(-900.9, 97.96) * mm});
            skLineSegment(sketch, "E1312", {"start": v(-901.01, 101.95) * mm, "end": v(-901.01, 98.23) * mm});
            skArc(sketch, "E1313", {"start": v(-900.9, 102.22) * mm, "mid": v(-900.98, 102.1) * mm, "end": v(-901.01, 101.95) * mm});
            skArc(sketch, "E1314", {"start": v(-900.9, 102.22) * mm, "mid": v(-901.01, 106.84) * mm, "end": v(-905.63, 106.94) * mm});
            skArc(sketch, "E1315", {"start": v(-905.9, 106.84) * mm, "mid": v(-905.76, 106.86) * mm, "end": v(-905.63, 106.94) * mm});
            skLineSegment(sketch, "E1316", {"start": v(-909.16, 106.84) * mm, "end": v(-905.9, 106.84) * mm});
            skArc(sketch, "E1317", {"start": v(-909.43, 106.94) * mm, "mid": v(-914.05, 106.84) * mm, "end": v(-914.16, 102.22) * mm});
            skArc(sketch, "E1318", {"start": v(-909.43, 106.94) * mm, "mid": v(-909.3, 106.86) * mm, "end": v(-909.16, 106.84) * mm});
            skArc(sketch, "E1319", {"start": v(-716.33, 101.95) * mm, "mid": v(-716.36, 102.1) * mm, "end": v(-716.44, 102.22) * mm});
            skArc(sketch, "E1320", {"start": v(-707.91, -290.97) * mm, "mid": v(-708.04, -290.89) * mm, "end": v(-708.18, -290.86) * mm});
            skLineSegment(sketch, "E1321", {"start": v(-770.81, 74.89) * mm, "end": v(-770.81, 87.99) * mm});
            skLineSegment(sketch, "E1322", {"start": v(-770.81, 87.99) * mm, "end": v(-733.92, 87.99) * mm});
            skArc(sketch, "E1323", {"start": v(-733.65, 87.88) * mm, "mid": v(-733.78, 87.96) * mm, "end": v(-733.92, 87.99) * mm});
            skArc(sketch, "E1324", {"start": v(-733.65, 87.88) * mm, "mid": v(-729.03, 87.99) * mm, "end": v(-728.93, 92.6) * mm});
            skArc(sketch, "E1325", {"start": v(-729.03, 92.88) * mm, "mid": v(-729, 92.73) * mm, "end": v(-728.93, 92.6) * mm});
            skLineSegment(sketch, "E1326", {"start": v(-729.03, 92.88) * mm, "end": v(-729.03, 107.3) * mm});
            skLineSegment(sketch, "E1327", {"start": v(-729.03, 107.3) * mm, "end": v(-716.8, 119.54) * mm});
            skLineSegment(sketch, "E1328", {"start": v(-716.8, 119.54) * mm, "end": v(-702.83, 119.54) * mm});
            skLineSegment(sketch, "E1329", {"start": v(-702.83, 119.54) * mm, "end": v(-690.6, 107.3) * mm});
            skLineSegment(sketch, "E1330", {"start": v(-690.6, 107.3) * mm, "end": v(-690.6, 92.88) * mm});
            skArc(sketch, "E1331", {"start": v(-690.7, 92.6) * mm, "mid": v(-690.62, 92.73) * mm, "end": v(-690.6, 92.88) * mm});
            skArc(sketch, "E1332", {"start": v(-690.7, 92.6) * mm, "mid": v(-690.6, 87.99) * mm, "end": v(-685.97, 87.88) * mm});
            skArc(sketch, "E1333", {"start": v(-685.7, 87.99) * mm, "mid": v(-685.85, 87.96) * mm, "end": v(-685.97, 87.88) * mm});
            skLineSegment(sketch, "E1334", {"start": v(-685.7, 87.99) * mm, "end": v(-634.81, 87.99) * mm});
            skLineSegment(sketch, "E1335", {"start": v(-634.81, 87.99) * mm, "end": v(-634.81, 75.29) * mm});
            skArc(sketch, "E1336", {"start": v(-641.81, 68.29) * mm, "mid": v(-636.86, 70.34) * mm, "end": v(-634.81, 75.29) * mm});
            skArc(sketch, "E1337", {"start": v(-703.3, -285.97) * mm, "mid": v(-703.27, -286.12) * mm, "end": v(-703.19, -286.24) * mm});
            skArc(sketch, "E1338", {"start": v(-641.81, 68.29) * mm, "mid": v(-646.76, 66.24) * mm, "end": v(-648.81, 61.29) * mm});
            skLineSegment(sketch, "E1339", {"start": v(-648.81, -245.31) * mm, "end": v(-648.81, 61.29) * mm});
            skArc(sketch, "E1340", {"start": v(-648.81, -245.31) * mm, "mid": v(-646.76, -250.26) * mm, "end": v(-641.81, -252.31) * mm});
            skArc(sketch, "E1341", {"start": v(-634.81, -259.31) * mm, "mid": v(-636.86, -254.36) * mm, "end": v(-641.81, -252.31) * mm});
            skLineSegment(sketch, "E1342", {"start": v(-634.81, -272.01) * mm, "end": v(-634.81, -259.31) * mm});
            skLineSegment(sketch, "E1343", {"start": v(-685.7, -272.01) * mm, "end": v(-634.81, -272.01) * mm});
            skArc(sketch, "E1344", {"start": v(-685.97, -271.9) * mm, "mid": v(-685.85, -271.99) * mm, "end": v(-685.7, -272.01) * mm});
            skArc(sketch, "E1345", {"start": v(-685.97, -271.9) * mm, "mid": v(-690.6, -272.01) * mm, "end": v(-690.7, -276.63) * mm});
            skArc(sketch, "E1346", {"start": v(-690.6, -276.9) * mm, "mid": v(-690.62, -276.76) * mm, "end": v(-690.7, -276.63) * mm});
            skLineSegment(sketch, "E1347", {"start": v(-690.6, -291.32) * mm, "end": v(-690.6, -276.9) * mm});
            skLineSegment(sketch, "E1348", {"start": v(-702.83, -303.56) * mm, "end": v(-690.6, -291.32) * mm});
            skLineSegment(sketch, "E1349", {"start": v(-716.8, -303.56) * mm, "end": v(-702.83, -303.56) * mm});
            skLineSegment(sketch, "E1350", {"start": v(-729.03, -291.32) * mm, "end": v(-716.8, -303.56) * mm});
            skLineSegment(sketch, "E1351", {"start": v(-729.03, -276.9) * mm, "end": v(-729.03, -291.32) * mm});
            skArc(sketch, "E1352", {"start": v(-728.93, -276.63) * mm, "mid": v(-729, -276.76) * mm, "end": v(-729.03, -276.9) * mm});
            skArc(sketch, "E1353", {"start": v(-728.93, -276.63) * mm, "mid": v(-729.03, -272.01) * mm, "end": v(-733.65, -271.9) * mm});
            skArc(sketch, "E1354", {"start": v(-707.91, 93.23) * mm, "mid": v(-708.04, 93.31) * mm, "end": v(-708.18, 93.34) * mm});
            skArc(sketch, "E1355", {"start": v(-733.92, -272.01) * mm, "mid": v(-733.78, -271.99) * mm, "end": v(-733.65, -271.9) * mm});
            skLineSegment(sketch, "E1356", {"start": v(-770.81, -272.01) * mm, "end": v(-733.92, -272.01) * mm});
            skLineSegment(sketch, "E1357", {"start": v(-770.81, -258.91) * mm, "end": v(-770.81, -272.01) * mm});
            skArc(sketch, "E1358", {"start": v(-770.81, -258.91) * mm, "mid": v(-772.86, -253.96) * mm, "end": v(-777.81, -251.91) * mm});
            skArc(sketch, "E1359", {"start": v(-784.81, -244.91) * mm, "mid": v(-782.76, -249.86) * mm, "end": v(-777.81, -251.91) * mm});
            skLineSegment(sketch, "E1360", {"start": v(-784.81, 60.89) * mm, "end": v(-784.81, -244.91) * mm});
            skArc(sketch, "E1361", {"start": v(-777.81, 67.89) * mm, "mid": v(-782.76, 65.84) * mm, "end": v(-784.81, 60.89) * mm});
            skArc(sketch, "E1362", {"start": v(-716.44, -286.24) * mm, "mid": v(-716.36, -286.12) * mm, "end": v(-716.33, -285.97) * mm});
            skArc(sketch, "E1363", {"start": v(-777.81, 67.89) * mm, "mid": v(-772.86, 69.94) * mm, "end": v(-770.81, 74.89) * mm});
            skArc(sketch, "E1364", {"start": v(-707.91, -290.97) * mm, "mid": v(-703.3, -290.86) * mm, "end": v(-703.19, -286.24) * mm});
            skLineSegment(sketch, "E1365", {"start": v(-703.3, -285.97) * mm, "end": v(-703.3, -282.25) * mm});
            skArc(sketch, "E1366", {"start": v(-716.44, 97.96) * mm, "mid": v(-716.36, 98.08) * mm, "end": v(-716.33, 98.23) * mm});
            skArc(sketch, "E1367", {"start": v(-703.19, -281.98) * mm, "mid": v(-703.27, -282.1) * mm, "end": v(-703.3, -282.25) * mm});
            skArc(sketch, "E1368", {"start": v(-703.19, -281.98) * mm, "mid": v(-703.3, -277.36) * mm, "end": v(-707.91, -277.26) * mm});
            skArc(sketch, "E1369", {"start": v(-708.18, -277.36) * mm, "mid": v(-708.04, -277.34) * mm, "end": v(-707.91, -277.26) * mm});
            skLineSegment(sketch, "E1370", {"start": v(-708.18, -277.36) * mm, "end": v(-711.44, -277.36) * mm});
            skArc(sketch, "E1371", {"start": v(-711.71, -277.26) * mm, "mid": v(-711.59, -277.34) * mm, "end": v(-711.44, -277.36) * mm});
            skArc(sketch, "E1372", {"start": v(-711.71, -277.26) * mm, "mid": v(-716.33, -277.36) * mm, "end": v(-716.44, -281.98) * mm});
            skArc(sketch, "E1373", {"start": v(-716.33, -282.25) * mm, "mid": v(-716.36, -282.1) * mm, "end": v(-716.44, -281.98) * mm});
            skLineSegment(sketch, "E1374", {"start": v(-716.33, -282.25) * mm, "end": v(-716.33, -285.97) * mm});
            skArc(sketch, "E1375", {"start": v(-716.44, -286.24) * mm, "mid": v(-716.33, -290.86) * mm, "end": v(-711.71, -290.97) * mm});
            skArc(sketch, "E1376", {"start": v(-711.44, -290.86) * mm, "mid": v(-711.59, -290.89) * mm, "end": v(-711.71, -290.97) * mm});
            skLineSegment(sketch, "E1377", {"start": v(-711.44, -290.86) * mm, "end": v(-708.18, -290.86) * mm});
            skLineSegment(sketch, "E1378", {"start": v(-716.33, 98.23) * mm, "end": v(-716.33, 101.95) * mm});
            skArc(sketch, "E1379", {"start": v(-716.44, 97.96) * mm, "mid": v(-716.33, 93.34) * mm, "end": v(-711.71, 93.23) * mm});
            skArc(sketch, "E1380", {"start": v(-711.44, 93.34) * mm, "mid": v(-711.59, 93.31) * mm, "end": v(-711.71, 93.23) * mm});
            skLineSegment(sketch, "E1381", {"start": v(-708.18, 93.34) * mm, "end": v(-711.44, 93.34) * mm});
            skArc(sketch, "E1382", {"start": v(-707.91, 93.23) * mm, "mid": v(-703.3, 93.34) * mm, "end": v(-703.19, 97.96) * mm});
            skArc(sketch, "E1383", {"start": v(-703.3, 98.23) * mm, "mid": v(-703.27, 98.08) * mm, "end": v(-703.19, 97.96) * mm});
            skLineSegment(sketch, "E1384", {"start": v(-703.3, 101.95) * mm, "end": v(-703.3, 98.23) * mm});
            skArc(sketch, "E1385", {"start": v(-703.19, 102.22) * mm, "mid": v(-703.27, 102.1) * mm, "end": v(-703.3, 101.95) * mm});
            skArc(sketch, "E1386", {"start": v(-703.19, 102.22) * mm, "mid": v(-703.3, 106.84) * mm, "end": v(-707.91, 106.94) * mm});
            skArc(sketch, "E1387", {"start": v(-708.18, 106.84) * mm, "mid": v(-708.04, 106.86) * mm, "end": v(-707.91, 106.94) * mm});
            skArc(sketch, "E1388", {"start": v(-711.71, 106.94) * mm, "mid": v(-711.59, 106.86) * mm, "end": v(-711.44, 106.84) * mm});
            skLineSegment(sketch, "E1389", {"start": v(-711.44, 106.84) * mm, "end": v(-708.18, 106.84) * mm});
            skArc(sketch, "E1390", {"start": v(-711.71, 106.94) * mm, "mid": v(-716.33, 106.84) * mm, "end": v(-716.44, 102.22) * mm});
            skArc(sketch, "E1391", {"start": v(-747.26, 569.16) * mm, "mid": v(-747.1, 569.46) * mm, "end": v(-747.03, 569.8) * mm});
            skArc(sketch, "E1392", {"start": v(-741.92, 217.38) * mm, "mid": v(-742.25, 217.32) * mm, "end": v(-742.55, 217.15) * mm});
            skArc(sketch, "E1393", {"start": v(-747.03, 572.6) * mm, "mid": v(-747.1, 572.94) * mm, "end": v(-747.26, 573.24) * mm});
            skLineSegment(sketch, "E1394", {"start": v(-820.81, 564.45) * mm, "end": v(-820.81, 577.55) * mm});
            skLineSegment(sketch, "E1395", {"start": v(-747.03, 569.8) * mm, "end": v(-747.03, 572.6) * mm});
            skArc(sketch, "E1396", {"start": v(-708.37, 573.24) * mm, "mid": v(-708.53, 572.94) * mm, "end": v(-708.6, 572.6) * mm});
            skArc(sketch, "E1397", {"start": v(-747.26, 569.16) * mm, "mid": v(-747.03, 564.68) * mm, "end": v(-742.55, 564.45) * mm});
            skArc(sketch, "E1398", {"start": v(-741.92, 564.68) * mm, "mid": v(-742.25, 564.62) * mm, "end": v(-742.55, 564.45) * mm});
            skLineSegment(sketch, "E1399", {"start": v(-713.7, 564.68) * mm, "end": v(-741.92, 564.68) * mm});
            skArc(sketch, "E1400", {"start": v(-696.12, 582.03) * mm, "mid": v(-695.9, 577.55) * mm, "end": v(-691.41, 577.32) * mm});
            skArc(sketch, "E1401", {"start": v(-713.07, 564.45) * mm, "mid": v(-713.37, 564.62) * mm, "end": v(-713.7, 564.68) * mm});
            skArc(sketch, "E1402", {"start": v(-713.07, 564.45) * mm, "mid": v(-708.6, 564.68) * mm, "end": v(-708.37, 569.16) * mm});
            skArc(sketch, "E1403", {"start": v(-634.81, 282.55) * mm, "mid": v(-643.6, 303.76) * mm, "end": v(-664.81, 312.55) * mm});
            skArc(sketch, "E1404", {"start": v(-708.6, 569.8) * mm, "mid": v(-708.53, 569.46) * mm, "end": v(-708.37, 569.16) * mm});
            skLineSegment(sketch, "E1405", {"start": v(-708.6, 572.6) * mm, "end": v(-708.6, 569.8) * mm});
            skArc(sketch, "E1406", {"start": v(-708.37, 573.24) * mm, "mid": v(-708.6, 577.72) * mm, "end": v(-713.07, 577.95) * mm});
            skArc(sketch, "E1407", {"start": v(-713.7, 577.72) * mm, "mid": v(-713.37, 577.78) * mm, "end": v(-713.07, 577.95) * mm});
            skLineSegment(sketch, "E1408", {"start": v(-741.92, 577.72) * mm, "end": v(-713.7, 577.72) * mm});
            skArc(sketch, "E1409", {"start": v(-742.55, 577.95) * mm, "mid": v(-742.25, 577.78) * mm, "end": v(-741.92, 577.72) * mm});
            skArc(sketch, "E1410", {"start": v(-742.55, 577.95) * mm, "mid": v(-747.03, 577.72) * mm, "end": v(-747.26, 573.24) * mm});
            skLineSegment(sketch, "E1411", {"start": v(-820.81, 577.55) * mm, "end": v(-764.85, 577.55) * mm});
            skArc(sketch, "E1412", {"start": v(-764.21, 577.32) * mm, "mid": v(-764.51, 577.5) * mm, "end": v(-764.85, 577.55) * mm});
            skArc(sketch, "E1413", {"start": v(-764.21, 577.32) * mm, "mid": v(-759.73, 577.55) * mm, "end": v(-759.5, 582.03) * mm});
            skArc(sketch, "E1414", {"start": v(-759.73, 582.66) * mm, "mid": v(-759.67, 582.33) * mm, "end": v(-759.5, 582.03) * mm});
            skLineSegment(sketch, "E1415", {"start": v(-759.73, 582.66) * mm, "end": v(-759.73, 586.46) * mm});
            skLineSegment(sketch, "E1416", {"start": v(-759.73, 586.46) * mm, "end": v(-755.94, 590.25) * mm});
            skLineSegment(sketch, "E1417", {"start": v(-755.94, 590.25) * mm, "end": v(-699.69, 590.25) * mm});
            skLineSegment(sketch, "E1418", {"start": v(-699.69, 590.25) * mm, "end": v(-695.9, 586.46) * mm});
            skLineSegment(sketch, "E1419", {"start": v(-695.9, 586.46) * mm, "end": v(-695.9, 582.66) * mm});
            skArc(sketch, "E1420", {"start": v(-696.12, 582.03) * mm, "mid": v(-695.95, 582.33) * mm, "end": v(-695.9, 582.66) * mm});
            skArc(sketch, "E1421", {"start": v(-690.78, 577.55) * mm, "mid": v(-691.11, 577.5) * mm, "end": v(-691.41, 577.32) * mm});
            skLineSegment(sketch, "E1422", {"start": v(-690.78, 577.55) * mm, "end": v(-634.81, 577.55) * mm});
            skLineSegment(sketch, "E1423", {"start": v(-634.81, 577.55) * mm, "end": v(-634.81, 512.55) * mm});
            skArc(sketch, "E1424", {"start": v(-664.81, 482.55) * mm, "mid": v(-643.6, 491.34) * mm, "end": v(-634.81, 512.55) * mm});
            skArc(sketch, "E1425", {"start": v(-664.81, 482.55) * mm, "mid": v(-686.03, 473.76) * mm, "end": v(-694.81, 452.55) * mm});
            skArc(sketch, "E1426", {"start": v(-820.81, 230.65) * mm, "mid": v(-822.86, 235.6) * mm, "end": v(-827.81, 237.65) * mm});
            skLineSegment(sketch, "E1427", {"start": v(-694.81, 342.55) * mm, "end": v(-694.81, 452.55) * mm});
            skArc(sketch, "E1428", {"start": v(-694.81, 342.55) * mm, "mid": v(-686.03, 321.34) * mm, "end": v(-664.81, 312.55) * mm});
            skLineSegment(sketch, "E1429", {"start": v(-634.81, 217.55) * mm, "end": v(-634.81, 282.55) * mm});
            skLineSegment(sketch, "E1430", {"start": v(-690.78, 217.55) * mm, "end": v(-634.81, 217.55) * mm});
            skArc(sketch, "E1431", {"start": v(-691.41, 217.78) * mm, "mid": v(-691.11, 217.6) * mm, "end": v(-690.78, 217.55) * mm});
            skArc(sketch, "E1432", {"start": v(-691.41, 217.78) * mm, "mid": v(-695.9, 217.55) * mm, "end": v(-696.12, 213.07) * mm});
            skArc(sketch, "E1433", {"start": v(-695.9, 212.44) * mm, "mid": v(-695.95, 212.77) * mm, "end": v(-696.12, 213.07) * mm});
            skLineSegment(sketch, "E1434", {"start": v(-695.9, 208.64) * mm, "end": v(-695.9, 212.44) * mm});
            skLineSegment(sketch, "E1435", {"start": v(-699.69, 204.85) * mm, "end": v(-695.9, 208.64) * mm});
            skLineSegment(sketch, "E1436", {"start": v(-755.94, 204.85) * mm, "end": v(-699.69, 204.85) * mm});
            skLineSegment(sketch, "E1437", {"start": v(-759.73, 208.64) * mm, "end": v(-755.94, 204.85) * mm});
            skLineSegment(sketch, "E1438", {"start": v(-759.73, 212.44) * mm, "end": v(-759.73, 208.64) * mm});
            skArc(sketch, "E1439", {"start": v(-759.5, 213.07) * mm, "mid": v(-759.67, 212.77) * mm, "end": v(-759.73, 212.44) * mm});
            skArc(sketch, "E1440", {"start": v(-759.5, 213.07) * mm, "mid": v(-759.73, 217.55) * mm, "end": v(-764.21, 217.78) * mm});
            skArc(sketch, "E1441", {"start": v(-764.85, 217.55) * mm, "mid": v(-764.51, 217.6) * mm, "end": v(-764.21, 217.78) * mm});
            skArc(sketch, "E1442", {"start": v(-742.55, 230.65) * mm, "mid": v(-747.03, 230.42) * mm, "end": v(-747.26, 225.94) * mm});
            skLineSegment(sketch, "E1443", {"start": v(-820.81, 217.55) * mm, "end": v(-764.85, 217.55) * mm});
            skLineSegment(sketch, "E1444", {"start": v(-820.81, 230.65) * mm, "end": v(-820.81, 217.55) * mm});
            skArc(sketch, "E1445", {"start": v(-834.81, 244.65) * mm, "mid": v(-832.76, 239.7) * mm, "end": v(-827.81, 237.65) * mm});
            skLineSegment(sketch, "E1446", {"start": v(-834.81, 550.45) * mm, "end": v(-834.81, 244.65) * mm});
            skArc(sketch, "E1447", {"start": v(-827.81, 557.45) * mm, "mid": v(-832.76, 555.4) * mm, "end": v(-834.81, 550.45) * mm});
            skArc(sketch, "E1448", {"start": v(-827.81, 557.45) * mm, "mid": v(-822.86, 559.5) * mm, "end": v(-820.81, 564.45) * mm});
            skArc(sketch, "E1449", {"start": v(-713.07, 217.15) * mm, "mid": v(-713.37, 217.32) * mm, "end": v(-713.7, 217.38) * mm});
            skLineSegment(sketch, "E1450", {"start": v(-741.92, 217.38) * mm, "end": v(-713.7, 217.38) * mm});
            skArc(sketch, "E1451", {"start": v(-713.07, 217.15) * mm, "mid": v(-708.6, 217.38) * mm, "end": v(-708.37, 221.86) * mm});
            skArc(sketch, "E1452", {"start": v(-708.6, 222.5) * mm, "mid": v(-708.53, 222.16) * mm, "end": v(-708.37, 221.86) * mm});
            skArc(sketch, "E1453", {"start": v(-708.37, 225.94) * mm, "mid": v(-708.53, 225.64) * mm, "end": v(-708.6, 225.3) * mm});
            skLineSegment(sketch, "E1454", {"start": v(-708.6, 222.5) * mm, "end": v(-708.6, 225.3) * mm});
            skArc(sketch, "E1455", {"start": v(-708.37, 225.94) * mm, "mid": v(-708.6, 230.42) * mm, "end": v(-713.07, 230.65) * mm});
            skArc(sketch, "E1456", {"start": v(-713.7, 230.42) * mm, "mid": v(-713.37, 230.48) * mm, "end": v(-713.07, 230.65) * mm});
            skArc(sketch, "E1457", {"start": v(-742.55, 230.65) * mm, "mid": v(-742.25, 230.48) * mm, "end": v(-741.92, 230.42) * mm});
            skLineSegment(sketch, "E1458", {"start": v(-713.7, 230.42) * mm, "end": v(-741.92, 230.42) * mm});
            skArc(sketch, "E1459", {"start": v(-747.03, 225.3) * mm, "mid": v(-747.1, 225.64) * mm, "end": v(-747.26, 225.94) * mm});
            skArc(sketch, "E1460", {"start": v(-747.26, 221.86) * mm, "mid": v(-747.1, 222.16) * mm, "end": v(-747.03, 222.5) * mm});
            skLineSegment(sketch, "E1461", {"start": v(-747.03, 225.3) * mm, "end": v(-747.03, 222.5) * mm});
            skArc(sketch, "E1462", {"start": v(-747.26, 221.86) * mm, "mid": v(-747.03, 217.38) * mm, "end": v(-742.55, 217.15) * mm});
            skArc(sketch, "E1463", {"start": v(-957.44, 230.65) * mm, "mid": v(-957.14, 230.48) * mm, "end": v(-956.8, 230.42) * mm});
            skArc(sketch, "E1464", {"start": v(-923.14, 222.5) * mm, "mid": v(-923.08, 222.16) * mm, "end": v(-922.92, 221.86) * mm});
            skArc(sketch, "E1465", {"start": v(-928.25, 577.72) * mm, "mid": v(-927.92, 577.78) * mm, "end": v(-927.62, 577.95) * mm});
            skLineSegment(sketch, "E1466", {"start": v(-881.53, 230.65) * mm, "end": v(-881.53, 217.55) * mm});
            skLineSegment(sketch, "E1467", {"start": v(-923.14, 225.3) * mm, "end": v(-923.14, 222.5) * mm});
            skArc(sketch, "E1468", {"start": v(-922.92, 225.94) * mm, "mid": v(-923.08, 225.64) * mm, "end": v(-923.14, 225.3) * mm});
            skArc(sketch, "E1469", {"start": v(-928.25, 230.42) * mm, "mid": v(-927.92, 230.48) * mm, "end": v(-927.62, 230.65) * mm});
            skArc(sketch, "E1470", {"start": v(-922.92, 225.94) * mm, "mid": v(-923.14, 230.42) * mm, "end": v(-927.62, 230.65) * mm});
            skLineSegment(sketch, "E1471", {"start": v(-956.8, 230.42) * mm, "end": v(-928.25, 230.42) * mm});
            skArc(sketch, "E1472", {"start": v(-905.96, 217.78) * mm, "mid": v(-905.66, 217.6) * mm, "end": v(-905.33, 217.55) * mm});
            skArc(sketch, "E1473", {"start": v(-957.44, 230.65) * mm, "mid": v(-961.92, 230.42) * mm, "end": v(-962.15, 225.94) * mm});
            skArc(sketch, "E1474", {"start": v(-961.92, 225.3) * mm, "mid": v(-961.98, 225.64) * mm, "end": v(-962.15, 225.94) * mm});
            skLineSegment(sketch, "E1475", {"start": v(-961.92, 222.5) * mm, "end": v(-961.92, 225.3) * mm});
            skArc(sketch, "E1476", {"start": v(-962.15, 221.86) * mm, "mid": v(-961.92, 217.38) * mm, "end": v(-957.44, 217.15) * mm});
            skArc(sketch, "E1477", {"start": v(-962.15, 221.86) * mm, "mid": v(-961.98, 222.16) * mm, "end": v(-961.92, 222.5) * mm});
            skArc(sketch, "E1478", {"start": v(-956.8, 217.38) * mm, "mid": v(-957.14, 217.32) * mm, "end": v(-957.44, 217.15) * mm});
            skLineSegment(sketch, "E1479", {"start": v(-928.25, 217.38) * mm, "end": v(-956.8, 217.38) * mm});
            skArc(sketch, "E1480", {"start": v(-927.62, 217.15) * mm, "mid": v(-927.92, 217.32) * mm, "end": v(-928.25, 217.38) * mm});
            skArc(sketch, "E1481", {"start": v(-927.62, 217.15) * mm, "mid": v(-923.14, 217.38) * mm, "end": v(-922.92, 221.86) * mm});
            skLineSegment(sketch, "E1482", {"start": v(-881.53, 217.55) * mm, "end": v(-905.33, 217.55) * mm});
            skArc(sketch, "E1483", {"start": v(-910.44, 212.44) * mm, "mid": v(-910.5, 212.77) * mm, "end": v(-910.67, 213.07) * mm});
            skArc(sketch, "E1484", {"start": v(-905.96, 217.78) * mm, "mid": v(-910.44, 217.55) * mm, "end": v(-910.67, 213.07) * mm});
            skLineSegment(sketch, "E1485", {"start": v(-910.44, 212.44) * mm, "end": v(-910.44, 208.64) * mm});
            skLineSegment(sketch, "E1486", {"start": v(-910.44, 208.64) * mm, "end": v(-914.23, 204.85) * mm});
            skLineSegment(sketch, "E1487", {"start": v(-914.23, 204.85) * mm, "end": v(-970.83, 204.85) * mm});
            skLineSegment(sketch, "E1488", {"start": v(-970.83, 204.85) * mm, "end": v(-974.62, 208.64) * mm});
            skLineSegment(sketch, "E1489", {"start": v(-974.62, 208.64) * mm, "end": v(-974.62, 212.44) * mm});
            skArc(sketch, "E1490", {"start": v(-974.4, 213.07) * mm, "mid": v(-974.56, 212.77) * mm, "end": v(-974.62, 212.44) * mm});
            skArc(sketch, "E1491", {"start": v(-974.4, 213.07) * mm, "mid": v(-974.62, 217.55) * mm, "end": v(-979.1, 217.78) * mm});
            skArc(sketch, "E1492", {"start": v(-979.73, 217.55) * mm, "mid": v(-979.4, 217.6) * mm, "end": v(-979.1, 217.78) * mm});
            skLineSegment(sketch, "E1493", {"start": v(-979.73, 217.55) * mm, "end": v(-1017.53, 217.55) * mm});
            skLineSegment(sketch, "E1494", {"start": v(-1017.53, 217.55) * mm, "end": v(-1017.53, 230.25) * mm});
            skArc(sketch, "E1495", {"start": v(-1010.53, 237.25) * mm, "mid": v(-1015.48, 235.2) * mm, "end": v(-1017.53, 230.25) * mm});
            skArc(sketch, "E1496", {"start": v(-1010.53, 237.25) * mm, "mid": v(-1005.58, 239.3) * mm, "end": v(-1003.53, 244.25) * mm});
            skLineSegment(sketch, "E1497", {"start": v(-1003.53, 550.85) * mm, "end": v(-1003.53, 244.25) * mm});
            skArc(sketch, "E1498", {"start": v(-1003.53, 550.85) * mm, "mid": v(-1005.58, 555.8) * mm, "end": v(-1010.53, 557.85) * mm});
            skArc(sketch, "E1499", {"start": v(-1017.53, 564.85) * mm, "mid": v(-1015.48, 559.9) * mm, "end": v(-1010.53, 557.85) * mm});
            skLineSegment(sketch, "E1500", {"start": v(-1017.53, 577.55) * mm, "end": v(-1017.53, 564.85) * mm});
            skArc(sketch, "E1501", {"start": v(-979.1, 577.32) * mm, "mid": v(-979.4, 577.5) * mm, "end": v(-979.73, 577.55) * mm});
            skLineSegment(sketch, "E1502", {"start": v(-979.73, 577.55) * mm, "end": v(-1017.53, 577.55) * mm});
            skArc(sketch, "E1503", {"start": v(-874.53, 237.65) * mm, "mid": v(-879.48, 235.6) * mm, "end": v(-881.53, 230.65) * mm});
            skArc(sketch, "E1504", {"start": v(-979.1, 577.32) * mm, "mid": v(-974.62, 577.55) * mm, "end": v(-974.4, 582.03) * mm});
            skArc(sketch, "E1505", {"start": v(-974.62, 582.66) * mm, "mid": v(-974.56, 582.33) * mm, "end": v(-974.4, 582.03) * mm});
            skLineSegment(sketch, "E1506", {"start": v(-974.62, 586.46) * mm, "end": v(-974.62, 582.66) * mm});
            skLineSegment(sketch, "E1507", {"start": v(-970.83, 590.25) * mm, "end": v(-974.62, 586.46) * mm});
            skLineSegment(sketch, "E1508", {"start": v(-914.23, 590.25) * mm, "end": v(-970.83, 590.25) * mm});
            skArc(sketch, "E1509", {"start": v(-957.44, 577.95) * mm, "mid": v(-961.92, 577.72) * mm, "end": v(-962.15, 573.24) * mm});
            skLineSegment(sketch, "E1510", {"start": v(-910.44, 586.46) * mm, "end": v(-914.23, 590.25) * mm});
            skArc(sketch, "E1511", {"start": v(-910.67, 582.03) * mm, "mid": v(-910.5, 582.33) * mm, "end": v(-910.44, 582.66) * mm});
            skLineSegment(sketch, "E1512", {"start": v(-910.44, 582.66) * mm, "end": v(-910.44, 586.46) * mm});
            skArc(sketch, "E1513", {"start": v(-910.67, 582.03) * mm, "mid": v(-910.44, 577.55) * mm, "end": v(-905.96, 577.32) * mm});
            skArc(sketch, "E1514", {"start": v(-905.33, 577.55) * mm, "mid": v(-905.66, 577.5) * mm, "end": v(-905.96, 577.32) * mm});
            skLineSegment(sketch, "E1515", {"start": v(-881.53, 577.55) * mm, "end": v(-905.33, 577.55) * mm});
            skLineSegment(sketch, "E1516", {"start": v(-881.53, 564.45) * mm, "end": v(-881.53, 577.55) * mm});
            skArc(sketch, "E1517", {"start": v(-867.53, 550.45) * mm, "mid": v(-869.58, 555.4) * mm, "end": v(-874.53, 557.45) * mm});
            skArc(sketch, "E1518", {"start": v(-881.53, 564.45) * mm, "mid": v(-879.48, 559.5) * mm, "end": v(-874.53, 557.45) * mm});
            skLineSegment(sketch, "E1519", {"start": v(-867.53, 244.65) * mm, "end": v(-867.53, 550.45) * mm});
            skArc(sketch, "E1520", {"start": v(-874.53, 237.65) * mm, "mid": v(-869.58, 239.7) * mm, "end": v(-867.53, 244.65) * mm});
            skLineSegment(sketch, "E1521", {"start": v(-928.25, 577.72) * mm, "end": v(-956.8, 577.72) * mm});
            skArc(sketch, "E1522", {"start": v(-957.44, 577.95) * mm, "mid": v(-957.14, 577.78) * mm, "end": v(-956.8, 577.72) * mm});
            skArc(sketch, "E1523", {"start": v(-961.92, 572.6) * mm, "mid": v(-961.98, 572.94) * mm, "end": v(-962.15, 573.24) * mm});
            skArc(sketch, "E1524", {"start": v(-922.92, 573.24) * mm, "mid": v(-923.14, 577.72) * mm, "end": v(-927.62, 577.95) * mm});
            skLineSegment(sketch, "E1525", {"start": v(-961.92, 572.6) * mm, "end": v(-961.92, 569.8) * mm});
            skArc(sketch, "E1526", {"start": v(-962.15, 569.16) * mm, "mid": v(-961.98, 569.46) * mm, "end": v(-961.92, 569.8) * mm});
            skArc(sketch, "E1527", {"start": v(-962.15, 569.16) * mm, "mid": v(-961.92, 564.68) * mm, "end": v(-957.44, 564.45) * mm});
            skArc(sketch, "E1528", {"start": v(-956.8, 564.68) * mm, "mid": v(-957.14, 564.62) * mm, "end": v(-957.44, 564.45) * mm});
            skLineSegment(sketch, "E1529", {"start": v(-956.8, 564.68) * mm, "end": v(-928.25, 564.68) * mm});
            skArc(sketch, "E1530", {"start": v(-927.62, 564.45) * mm, "mid": v(-927.92, 564.62) * mm, "end": v(-928.25, 564.68) * mm});
            skArc(sketch, "E1531", {"start": v(-927.62, 564.45) * mm, "mid": v(-923.14, 564.68) * mm, "end": v(-922.92, 569.16) * mm});
            skArc(sketch, "E1532", {"start": v(-923.14, 569.8) * mm, "mid": v(-923.08, 569.46) * mm, "end": v(-922.92, 569.16) * mm});
            skArc(sketch, "E1533", {"start": v(-922.92, 573.24) * mm, "mid": v(-923.08, 572.94) * mm, "end": v(-923.14, 572.6) * mm});
            skLineSegment(sketch, "E1534", {"start": v(-923.14, 569.8) * mm, "end": v(-923.14, 572.6) * mm});
            skArc(sketch, "E1535", {"start": v(-1144.87, 569.16) * mm, "mid": v(-1144.7, 569.46) * mm, "end": v(-1144.64, 569.8) * mm});
            skArc(sketch, "E1536", {"start": v(-1139.53, 217.38) * mm, "mid": v(-1139.86, 217.32) * mm, "end": v(-1140.16, 217.15) * mm});
            skArc(sketch, "E1537", {"start": v(-1144.64, 572.6) * mm, "mid": v(-1144.7, 572.94) * mm, "end": v(-1144.87, 573.24) * mm});
            skLineSegment(sketch, "E1538", {"start": v(-1186.25, 564.45) * mm, "end": v(-1186.25, 577.55) * mm});
            skLineSegment(sketch, "E1539", {"start": v(-1144.64, 569.8) * mm, "end": v(-1144.64, 572.6) * mm});
            skArc(sketch, "E1540", {"start": v(-1144.87, 569.16) * mm, "mid": v(-1144.64, 564.68) * mm, "end": v(-1140.16, 564.45) * mm});
            skArc(sketch, "E1541", {"start": v(-1139.53, 564.68) * mm, "mid": v(-1139.86, 564.62) * mm, "end": v(-1140.16, 564.45) * mm});
            skArc(sketch, "E1542", {"start": v(-1110.34, 564.45) * mm, "mid": v(-1110.64, 564.62) * mm, "end": v(-1110.97, 564.68) * mm});
            skLineSegment(sketch, "E1543", {"start": v(-1110.97, 564.68) * mm, "end": v(-1139.53, 564.68) * mm});
            skArc(sketch, "E1544", {"start": v(-1105.86, 569.8) * mm, "mid": v(-1105.8, 569.46) * mm, "end": v(-1105.63, 569.16) * mm});
            skArc(sketch, "E1545", {"start": v(-1110.34, 564.45) * mm, "mid": v(-1105.86, 564.68) * mm, "end": v(-1105.63, 569.16) * mm});
            skLineSegment(sketch, "E1546", {"start": v(-1105.86, 572.6) * mm, "end": v(-1105.86, 569.8) * mm});
            skArc(sketch, "E1547", {"start": v(-1105.63, 573.24) * mm, "mid": v(-1105.86, 577.72) * mm, "end": v(-1110.34, 577.95) * mm});
            skArc(sketch, "E1548", {"start": v(-1105.63, 573.24) * mm, "mid": v(-1105.8, 572.94) * mm, "end": v(-1105.86, 572.6) * mm});
            skArc(sketch, "E1549", {"start": v(-1110.97, 577.72) * mm, "mid": v(-1110.64, 577.78) * mm, "end": v(-1110.34, 577.95) * mm});
            skLineSegment(sketch, "E1550", {"start": v(-1139.53, 577.72) * mm, "end": v(-1110.97, 577.72) * mm});
            skArc(sketch, "E1551", {"start": v(-1140.16, 577.95) * mm, "mid": v(-1139.86, 577.78) * mm, "end": v(-1139.53, 577.72) * mm});
            skArc(sketch, "E1552", {"start": v(-1140.16, 577.95) * mm, "mid": v(-1144.64, 577.72) * mm, "end": v(-1144.87, 573.24) * mm});
            skLineSegment(sketch, "E1553", {"start": v(-1186.25, 577.55) * mm, "end": v(-1162.45, 577.55) * mm});
            skArc(sketch, "E1554", {"start": v(-1161.82, 577.32) * mm, "mid": v(-1162.12, 577.5) * mm, "end": v(-1162.45, 577.55) * mm});
            skArc(sketch, "E1555", {"start": v(-1161.82, 577.32) * mm, "mid": v(-1157.34, 577.55) * mm, "end": v(-1157.11, 582.03) * mm});
            skArc(sketch, "E1556", {"start": v(-1157.34, 582.66) * mm, "mid": v(-1157.28, 582.33) * mm, "end": v(-1157.11, 582.03) * mm});
            skLineSegment(sketch, "E1557", {"start": v(-1157.34, 586.46) * mm, "end": v(-1153.55, 590.25) * mm});
            skLineSegment(sketch, "E1558", {"start": v(-1157.34, 582.66) * mm, "end": v(-1157.34, 586.46) * mm});
            skLineSegment(sketch, "E1559", {"start": v(-1153.55, 590.25) * mm, "end": v(-1096.95, 590.25) * mm});
            skLineSegment(sketch, "E1560", {"start": v(-1096.95, 590.25) * mm, "end": v(-1093.16, 586.46) * mm});
            skArc(sketch, "E1561", {"start": v(-1093.39, 582.03) * mm, "mid": v(-1093.22, 582.33) * mm, "end": v(-1093.16, 582.66) * mm});
            skLineSegment(sketch, "E1562", {"start": v(-1093.16, 586.46) * mm, "end": v(-1093.16, 582.66) * mm});
            skArc(sketch, "E1563", {"start": v(-1088.05, 577.55) * mm, "mid": v(-1088.38, 577.5) * mm, "end": v(-1088.68, 577.32) * mm});
            skArc(sketch, "E1564", {"start": v(-1093.39, 582.03) * mm, "mid": v(-1093.16, 577.55) * mm, "end": v(-1088.68, 577.32) * mm});
            skLineSegment(sketch, "E1565", {"start": v(-1088.05, 577.55) * mm, "end": v(-1050.25, 577.55) * mm});
            skLineSegment(sketch, "E1566", {"start": v(-1050.25, 577.55) * mm, "end": v(-1050.25, 564.85) * mm});
            skArc(sketch, "E1567", {"start": v(-1057.25, 557.85) * mm, "mid": v(-1052.3, 559.9) * mm, "end": v(-1050.25, 564.85) * mm});
            skArc(sketch, "E1568", {"start": v(-1057.25, 557.85) * mm, "mid": v(-1062.2, 555.8) * mm, "end": v(-1064.25, 550.85) * mm});
            skArc(sketch, "E1569", {"start": v(-1064.25, 244.25) * mm, "mid": v(-1062.2, 239.3) * mm, "end": v(-1057.25, 237.25) * mm});
            skLineSegment(sketch, "E1570", {"start": v(-1064.25, 244.25) * mm, "end": v(-1064.25, 550.85) * mm});
            skArc(sketch, "E1571", {"start": v(-1050.25, 230.25) * mm, "mid": v(-1052.3, 235.2) * mm, "end": v(-1057.25, 237.25) * mm});
            skLineSegment(sketch, "E1572", {"start": v(-1050.25, 217.55) * mm, "end": v(-1050.25, 230.25) * mm});
            skLineSegment(sketch, "E1573", {"start": v(-1088.05, 217.55) * mm, "end": v(-1050.25, 217.55) * mm});
            skArc(sketch, "E1574", {"start": v(-1088.68, 217.78) * mm, "mid": v(-1088.38, 217.6) * mm, "end": v(-1088.05, 217.55) * mm});
            skArc(sketch, "E1575", {"start": v(-1088.68, 217.78) * mm, "mid": v(-1093.16, 217.55) * mm, "end": v(-1093.39, 213.07) * mm});
            skArc(sketch, "E1576", {"start": v(-1093.16, 212.44) * mm, "mid": v(-1093.22, 212.77) * mm, "end": v(-1093.39, 213.07) * mm});
            skLineSegment(sketch, "E1577", {"start": v(-1093.16, 208.64) * mm, "end": v(-1093.16, 212.44) * mm});
            skLineSegment(sketch, "E1578", {"start": v(-1096.95, 204.85) * mm, "end": v(-1093.16, 208.64) * mm});
            skLineSegment(sketch, "E1579", {"start": v(-1153.55, 204.85) * mm, "end": v(-1096.95, 204.85) * mm});
            skLineSegment(sketch, "E1580", {"start": v(-1157.34, 208.64) * mm, "end": v(-1153.55, 204.85) * mm});
            skLineSegment(sketch, "E1581", {"start": v(-1157.34, 212.44) * mm, "end": v(-1157.34, 208.64) * mm});
            skArc(sketch, "E1582", {"start": v(-1157.11, 213.07) * mm, "mid": v(-1157.28, 212.77) * mm, "end": v(-1157.34, 212.44) * mm});
            skArc(sketch, "E1583", {"start": v(-1157.11, 213.07) * mm, "mid": v(-1157.34, 217.55) * mm, "end": v(-1161.82, 217.78) * mm});
            skArc(sketch, "E1584", {"start": v(-1162.45, 217.55) * mm, "mid": v(-1162.12, 217.6) * mm, "end": v(-1161.82, 217.78) * mm});
            skLineSegment(sketch, "E1585", {"start": v(-1186.25, 217.55) * mm, "end": v(-1162.45, 217.55) * mm});
            skArc(sketch, "E1586", {"start": v(-1186.25, 230.65) * mm, "mid": v(-1188.3, 235.6) * mm, "end": v(-1193.25, 237.65) * mm});
            skLineSegment(sketch, "E1587", {"start": v(-1186.25, 230.65) * mm, "end": v(-1186.25, 217.55) * mm});
            skArc(sketch, "E1588", {"start": v(-1200.25, 244.65) * mm, "mid": v(-1198.2, 239.7) * mm, "end": v(-1193.25, 237.65) * mm});
            skLineSegment(sketch, "E1589", {"start": v(-1200.25, 550.45) * mm, "end": v(-1200.25, 244.65) * mm});
            skArc(sketch, "E1590", {"start": v(-1193.25, 557.45) * mm, "mid": v(-1198.2, 555.4) * mm, "end": v(-1200.25, 550.45) * mm});
            skArc(sketch, "E1591", {"start": v(-1193.25, 557.45) * mm, "mid": v(-1188.3, 559.5) * mm, "end": v(-1186.25, 564.45) * mm});
            skLineSegment(sketch, "E1592", {"start": v(-1139.53, 217.38) * mm, "end": v(-1110.97, 217.38) * mm});
            skArc(sketch, "E1593", {"start": v(-1110.34, 217.15) * mm, "mid": v(-1110.64, 217.32) * mm, "end": v(-1110.97, 217.38) * mm});
            skArc(sketch, "E1594", {"start": v(-1110.34, 217.15) * mm, "mid": v(-1105.86, 217.38) * mm, "end": v(-1105.63, 221.86) * mm});
            skArc(sketch, "E1595", {"start": v(-1105.86, 222.5) * mm, "mid": v(-1105.8, 222.16) * mm, "end": v(-1105.63, 221.86) * mm});
            skLineSegment(sketch, "E1596", {"start": v(-1105.86, 222.5) * mm, "end": v(-1105.86, 225.3) * mm});
            skArc(sketch, "E1597", {"start": v(-1105.63, 225.94) * mm, "mid": v(-1105.8, 225.64) * mm, "end": v(-1105.86, 225.3) * mm});
            skArc(sketch, "E1598", {"start": v(-1105.63, 225.94) * mm, "mid": v(-1105.86, 230.42) * mm, "end": v(-1110.34, 230.65) * mm});
            skArc(sketch, "E1599", {"start": v(-1110.97, 230.42) * mm, "mid": v(-1110.64, 230.48) * mm, "end": v(-1110.34, 230.65) * mm});
            skLineSegment(sketch, "E1600", {"start": v(-1110.97, 230.42) * mm, "end": v(-1139.53, 230.42) * mm});
            skArc(sketch, "E1601", {"start": v(-1140.16, 230.65) * mm, "mid": v(-1139.86, 230.48) * mm, "end": v(-1139.53, 230.42) * mm});
            skArc(sketch, "E1602", {"start": v(-1140.16, 230.65) * mm, "mid": v(-1144.64, 230.42) * mm, "end": v(-1144.87, 225.94) * mm});
            skArc(sketch, "E1603", {"start": v(-1144.64, 225.3) * mm, "mid": v(-1144.7, 225.64) * mm, "end": v(-1144.87, 225.94) * mm});
            skLineSegment(sketch, "E1604", {"start": v(-1144.64, 225.3) * mm, "end": v(-1144.64, 222.5) * mm});
            skArc(sketch, "E1605", {"start": v(-1144.87, 221.86) * mm, "mid": v(-1144.7, 222.16) * mm, "end": v(-1144.64, 222.5) * mm});
            skArc(sketch, "E1606", {"start": v(-1144.87, 221.86) * mm, "mid": v(-1144.64, 217.38) * mm, "end": v(-1140.16, 217.15) * mm});
            skArc(sketch, "E1607", {"start": v(-1037.25, 68.29) * mm, "mid": v(-1042.2, 66.24) * mm, "end": v(-1044.25, 61.29) * mm});
            skArc(sketch, "E1608", {"start": v(-1109.64, 82.78) * mm, "mid": v(-1109.7, 83.2) * mm, "end": v(-1109.9, 83.56) * mm});
            skLineSegment(sketch, "E1609", {"start": v(-1044.25, -245.31) * mm, "end": v(-1044.25, 61.29) * mm});
            skArc(sketch, "E1610", {"start": v(-1075.29, -272.28) * mm, "mid": v(-1075.65, -272.08) * mm, "end": v(-1076.07, -272.01) * mm});
            skArc(sketch, "E1611", {"start": v(-1044.25, -245.31) * mm, "mid": v(-1042.2, -250.26) * mm, "end": v(-1037.25, -252.31) * mm});
            skArc(sketch, "E1612", {"start": v(-1030.25, -259.31) * mm, "mid": v(-1032.3, -254.36) * mm, "end": v(-1037.25, -252.31) * mm});
            skLineSegment(sketch, "E1613", {"start": v(-1030.25, -272.01) * mm, "end": v(-1030.25, -259.31) * mm});
            skLineSegment(sketch, "E1614", {"start": v(-1058.16, -272.01) * mm, "end": v(-1030.25, -272.01) * mm});
            skLineSegment(sketch, "E1615", {"start": v(-1058.16, -278.36) * mm, "end": v(-1058.16, -272.01) * mm});
            skLineSegment(sketch, "E1616", {"start": v(-1064.5, -284.71) * mm, "end": v(-1058.16, -278.36) * mm});
            skLineSegment(sketch, "E1617", {"start": v(-1116, -284.71) * mm, "end": v(-1064.5, -284.71) * mm});
            skLineSegment(sketch, "E1618", {"start": v(-1122.34, -278.36) * mm, "end": v(-1116, -284.71) * mm});
            skLineSegment(sketch, "E1619", {"start": v(-1122.34, -272.01) * mm, "end": v(-1122.34, -278.36) * mm});
            skLineSegment(sketch, "E1620", {"start": v(-1200.25, -272.01) * mm, "end": v(-1122.34, -272.01) * mm});
            skLineSegment(sketch, "E1621", {"start": v(-1200.25, 87.99) * mm, "end": v(-1200.25, -272.01) * mm});
            skLineSegment(sketch, "E1622", {"start": v(-1200.25, 87.99) * mm, "end": v(-1122.34, 87.99) * mm});
            skLineSegment(sketch, "E1623", {"start": v(-1122.34, 87.99) * mm, "end": v(-1122.34, 94.34) * mm});
            skLineSegment(sketch, "E1624", {"start": v(-1122.34, 94.34) * mm, "end": v(-1116, 100.69) * mm});
            skLineSegment(sketch, "E1625", {"start": v(-1116, 100.69) * mm, "end": v(-1064.5, 100.69) * mm});
            skLineSegment(sketch, "E1626", {"start": v(-1064.5, 100.69) * mm, "end": v(-1058.16, 94.34) * mm});
            skLineSegment(sketch, "E1627", {"start": v(-1058.16, 94.34) * mm, "end": v(-1058.16, 87.99) * mm});
            skLineSegment(sketch, "E1628", {"start": v(-1058.16, 87.99) * mm, "end": v(-1030.25, 87.99) * mm});
            skLineSegment(sketch, "E1629", {"start": v(-1030.25, 87.99) * mm, "end": v(-1030.25, 75.29) * mm});
            skArc(sketch, "E1630", {"start": v(-1037.25, 68.29) * mm, "mid": v(-1032.3, 70.34) * mm, "end": v(-1030.25, 75.29) * mm});
            skArc(sketch, "E1631", {"start": v(-1075.29, -272.28) * mm, "mid": v(-1070.86, -272.01) * mm, "end": v(-1070.6, -267.59) * mm});
            skArc(sketch, "E1632", {"start": v(-1070.86, -266.8) * mm, "mid": v(-1070.8, -267.22) * mm, "end": v(-1070.6, -267.59) * mm});
            skArc(sketch, "E1633", {"start": v(-1070.6, -263.74) * mm, "mid": v(-1070.8, -264.1) * mm, "end": v(-1070.86, -264.52) * mm});
            skLineSegment(sketch, "E1634", {"start": v(-1070.86, -266.8) * mm, "end": v(-1070.86, -264.52) * mm});
            skArc(sketch, "E1635", {"start": v(-1070.6, -263.74) * mm, "mid": v(-1070.86, -259.31) * mm, "end": v(-1075.29, -259.04) * mm});
            skArc(sketch, "E1636", {"start": v(-1076.07, -259.31) * mm, "mid": v(-1075.65, -259.24) * mm, "end": v(-1075.29, -259.04) * mm});
            skLineSegment(sketch, "E1637", {"start": v(-1076.07, -259.31) * mm, "end": v(-1104.43, -259.31) * mm});
            skArc(sketch, "E1638", {"start": v(-1105.21, -259.04) * mm, "mid": v(-1104.85, -259.24) * mm, "end": v(-1104.43, -259.31) * mm});
            skArc(sketch, "E1639", {"start": v(-1105.21, -259.04) * mm, "mid": v(-1109.64, -259.31) * mm, "end": v(-1109.9, -263.74) * mm});
            skArc(sketch, "E1640", {"start": v(-1109.64, -264.52) * mm, "mid": v(-1109.7, -264.1) * mm, "end": v(-1109.9, -263.74) * mm});
            skLineSegment(sketch, "E1641", {"start": v(-1109.64, -264.52) * mm, "end": v(-1109.64, -266.8) * mm});
            skArc(sketch, "E1642", {"start": v(-1109.9, -267.59) * mm, "mid": v(-1109.7, -267.22) * mm, "end": v(-1109.64, -266.8) * mm});
            skArc(sketch, "E1643", {"start": v(-1075.29, 75.02) * mm, "mid": v(-1070.86, 75.29) * mm, "end": v(-1070.6, 79.71) * mm});
            skArc(sketch, "E1644", {"start": v(-1109.9, -267.59) * mm, "mid": v(-1109.64, -272.01) * mm, "end": v(-1105.21, -272.28) * mm});
            skArc(sketch, "E1645", {"start": v(-1104.43, -272.01) * mm, "mid": v(-1104.85, -272.08) * mm, "end": v(-1105.21, -272.28) * mm});
            skLineSegment(sketch, "E1646", {"start": v(-1104.43, -272.01) * mm, "end": v(-1076.07, -272.01) * mm});
            skLineSegment(sketch, "E1647", {"start": v(-1109.64, 80.5) * mm, "end": v(-1109.64, 82.78) * mm});
            skArc(sketch, "E1648", {"start": v(-1109.9, 79.71) * mm, "mid": v(-1109.7, 80.08) * mm, "end": v(-1109.64, 80.5) * mm});
            skArc(sketch, "E1649", {"start": v(-1109.9, 79.71) * mm, "mid": v(-1109.64, 75.29) * mm, "end": v(-1105.21, 75.02) * mm});
            skArc(sketch, "E1650", {"start": v(-1104.43, 75.29) * mm, "mid": v(-1104.85, 75.22) * mm, "end": v(-1105.21, 75.02) * mm});
            skLineSegment(sketch, "E1651", {"start": v(-1076.07, 75.29) * mm, "end": v(-1104.43, 75.29) * mm});
            skArc(sketch, "E1652", {"start": v(-1075.29, 75.02) * mm, "mid": v(-1075.65, 75.22) * mm, "end": v(-1076.07, 75.29) * mm});
            skArc(sketch, "E1653", {"start": v(-1070.86, 80.5) * mm, "mid": v(-1070.8, 80.08) * mm, "end": v(-1070.6, 79.71) * mm});
            skArc(sketch, "E1654", {"start": v(-1105.21, 88.26) * mm, "mid": v(-1104.85, 88.06) * mm, "end": v(-1104.43, 87.99) * mm});
            skLineSegment(sketch, "E1655", {"start": v(-1070.86, 82.78) * mm, "end": v(-1070.86, 80.5) * mm});
            skArc(sketch, "E1656", {"start": v(-1070.6, 83.56) * mm, "mid": v(-1070.8, 83.2) * mm, "end": v(-1070.86, 82.78) * mm});
            skArc(sketch, "E1657", {"start": v(-1070.6, 83.56) * mm, "mid": v(-1070.86, 87.99) * mm, "end": v(-1075.29, 88.26) * mm});
            skArc(sketch, "E1658", {"start": v(-1076.07, 87.99) * mm, "mid": v(-1075.65, 88.06) * mm, "end": v(-1075.29, 88.26) * mm});
            skLineSegment(sketch, "E1659", {"start": v(-1104.43, 87.99) * mm, "end": v(-1076.07, 87.99) * mm});
            skArc(sketch, "E1660", {"start": v(-1105.21, 88.26) * mm, "mid": v(-1109.64, 87.99) * mm, "end": v(-1109.9, 83.56) * mm});
            skArc(sketch, "E1661", {"start": v(-1182.66, -455.4) * mm, "mid": v(-1182.8, -455.42) * mm, "end": v(-1182.93, -455.5) * mm});
            skArc(sketch, "E1662", {"start": v(-808.97, -425.23) * mm, "mid": v(-808.77, -424.86) * mm, "end": v(-808.7, -424.45) * mm});
            skLineSegment(sketch, "E1663", {"start": v(-954.27, -542.8) * mm, "end": v(-1019.64, -551.88) * mm});
            skArc(sketch, "E1664", {"start": v(-789.75, -446.98) * mm, "mid": v(-789.82, -447.1) * mm, "end": v(-789.85, -447.25) * mm});
            skLineSegment(sketch, "E1665", {"start": v(-926.13, -565.85) * mm, "end": v(-930.68, -533.1) * mm});
            skArc(sketch, "E1666", {"start": v(-1019.64, -551.88) * mm, "mid": v(-1029.87, -565.41) * mm, "end": v(-1016.34, -575.65) * mm});
            skLineSegment(sketch, "E1667", {"start": v(-1016.34, -575.65) * mm, "end": v(-950.96, -566.57) * mm});
            skArc(sketch, "E1668", {"start": v(-950.96, -566.57) * mm, "mid": v(-940.73, -553.03) * mm, "end": v(-954.27, -542.8) * mm});
            skArc(sketch, "E1669", {"start": v(-804.27, -467.83) * mm, "mid": v(-808.7, -468.1) * mm, "end": v(-808.97, -472.52) * mm});
            skLineSegment(sketch, "E1670", {"start": v(-934.66, -577.13) * mm, "end": v(-926.13, -565.85) * mm});
            skLineSegment(sketch, "E1671", {"start": v(-1040.43, -581.72) * mm, "end": v(-1029.15, -590.25) * mm});
            skLineSegment(sketch, "E1672", {"start": v(-1029.15, -590.25) * mm, "end": v(-934.66, -577.13) * mm});
            skLineSegment(sketch, "E1673", {"start": v(-1044.98, -548.98) * mm, "end": v(-1040.43, -581.72) * mm});
            skArc(sketch, "E1674", {"start": v(-1044.98, -548.98) * mm, "mid": v(-1042.27, -545.4) * mm, "end": v(-1045.85, -542.7) * mm});
            skLineSegment(sketch, "E1675", {"start": v(-1168.7, -559.76) * mm, "end": v(-1045.85, -542.7) * mm});
            skLineSegment(sketch, "E1676", {"start": v(-1168.7, -559.76) * mm, "end": v(-1168.7, -473.3) * mm});
            skArc(sketch, "E1677", {"start": v(-1168.43, -472.52) * mm, "mid": v(-1168.63, -472.9) * mm, "end": v(-1168.7, -473.3) * mm});
            skArc(sketch, "E1678", {"start": v(-1168.43, -472.52) * mm, "mid": v(-1168.7, -468.1) * mm, "end": v(-1173.13, -467.83) * mm});
            skArc(sketch, "E1679", {"start": v(-1173.9, -468.1) * mm, "mid": v(-1173.5, -468.03) * mm, "end": v(-1173.13, -467.83) * mm});
            skLineSegment(sketch, "E1680", {"start": v(-1173.9, -468.1) * mm, "end": v(-1187.7, -468.1) * mm});
            skLineSegment(sketch, "E1681", {"start": v(-1187.7, -468.1) * mm, "end": v(-1200.25, -455.54) * mm});
            skLineSegment(sketch, "E1682", {"start": v(-1200.25, -455.54) * mm, "end": v(-1200.25, -442.21) * mm});
            skLineSegment(sketch, "E1683", {"start": v(-1200.25, -442.21) * mm, "end": v(-1187.7, -429.66) * mm});
            skLineSegment(sketch, "E1684", {"start": v(-1187.7, -429.66) * mm, "end": v(-1173.9, -429.66) * mm});
            skArc(sketch, "E1685", {"start": v(-1173.13, -429.93) * mm, "mid": v(-1173.5, -429.73) * mm, "end": v(-1173.9, -429.66) * mm});
            skArc(sketch, "E1686", {"start": v(-1173.13, -429.93) * mm, "mid": v(-1168.7, -429.66) * mm, "end": v(-1168.43, -425.23) * mm});
            skArc(sketch, "E1687", {"start": v(-1168.7, -424.45) * mm, "mid": v(-1168.63, -424.86) * mm, "end": v(-1168.43, -425.23) * mm});
            skLineSegment(sketch, "E1688", {"start": v(-1168.7, -424.45) * mm, "end": v(-1168.7, -388.88) * mm});
            skLineSegment(sketch, "E1689", {"start": v(-1168.7, -388.88) * mm, "end": v(-1156, -388.88) * mm});
            skArc(sketch, "E1690", {"start": v(-1149, -395.88) * mm, "mid": v(-1151.05, -390.93) * mm, "end": v(-1156, -388.88) * mm});
            skArc(sketch, "E1691", {"start": v(-1149, -395.88) * mm, "mid": v(-1146.95, -400.83) * mm, "end": v(-1142, -402.88) * mm});
            skLineSegment(sketch, "E1692", {"start": v(-835.4, -402.88) * mm, "end": v(-1142, -402.88) * mm});
            skArc(sketch, "E1693", {"start": v(-835.4, -402.88) * mm, "mid": v(-830.45, -400.83) * mm, "end": v(-828.4, -395.88) * mm});
            skArc(sketch, "E1694", {"start": v(-821.4, -388.88) * mm, "mid": v(-826.35, -390.93) * mm, "end": v(-828.4, -395.88) * mm});
            skLineSegment(sketch, "E1695", {"start": v(-808.7, -388.88) * mm, "end": v(-821.4, -388.88) * mm});
            skLineSegment(sketch, "E1696", {"start": v(-808.7, -424.45) * mm, "end": v(-808.7, -388.88) * mm});
            skArc(sketch, "E1697", {"start": v(-808.97, -425.23) * mm, "mid": v(-808.7, -429.66) * mm, "end": v(-804.27, -429.93) * mm});
            skArc(sketch, "E1698", {"start": v(-803.5, -429.66) * mm, "mid": v(-803.9, -429.73) * mm, "end": v(-804.27, -429.93) * mm});
            skLineSegment(sketch, "E1699", {"start": v(-789.7, -429.66) * mm, "end": v(-803.5, -429.66) * mm});
            skLineSegment(sketch, "E1700", {"start": v(-777.15, -442.21) * mm, "end": v(-789.7, -429.66) * mm});
            skLineSegment(sketch, "E1701", {"start": v(-777.15, -455.54) * mm, "end": v(-777.15, -442.21) * mm});
            skLineSegment(sketch, "E1702", {"start": v(-789.7, -468.1) * mm, "end": v(-777.15, -455.54) * mm});
            skLineSegment(sketch, "E1703", {"start": v(-803.5, -468.1) * mm, "end": v(-789.7, -468.1) * mm});
            skArc(sketch, "E1704", {"start": v(-804.27, -467.83) * mm, "mid": v(-803.9, -468.03) * mm, "end": v(-803.5, -468.1) * mm});
            skArc(sketch, "E1705", {"start": v(-808.7, -473.3) * mm, "mid": v(-808.77, -472.9) * mm, "end": v(-808.97, -472.52) * mm});
            skLineSegment(sketch, "E1706", {"start": v(-808.7, -509.76) * mm, "end": v(-808.7, -473.3) * mm});
            skLineSegment(sketch, "E1707", {"start": v(-931.55, -526.82) * mm, "end": v(-808.7, -509.76) * mm});
            skArc(sketch, "E1708", {"start": v(-931.55, -526.82) * mm, "mid": v(-934.26, -530.4) * mm, "end": v(-930.68, -533.1) * mm});
            skArc(sketch, "E1709", {"start": v(-789.75, -446.98) * mm, "mid": v(-789.85, -442.36) * mm, "end": v(-794.47, -442.25) * mm});
            skArc(sketch, "E1710", {"start": v(-794.74, -442.36) * mm, "mid": v(-794.6, -442.33) * mm, "end": v(-794.47, -442.25) * mm});
            skLineSegment(sketch, "E1711", {"start": v(-794.74, -442.36) * mm, "end": v(-798.46, -442.36) * mm});
            skArc(sketch, "E1712", {"start": v(-798.73, -442.25) * mm, "mid": v(-798.6, -442.33) * mm, "end": v(-798.46, -442.36) * mm});
            skArc(sketch, "E1713", {"start": v(-798.73, -442.25) * mm, "mid": v(-803.35, -442.36) * mm, "end": v(-803.45, -446.98) * mm});
            skArc(sketch, "E1714", {"start": v(-803.35, -447.25) * mm, "mid": v(-803.38, -447.1) * mm, "end": v(-803.45, -446.98) * mm});
            skLineSegment(sketch, "E1715", {"start": v(-803.35, -447.25) * mm, "end": v(-803.35, -450.5) * mm});
            skArc(sketch, "E1716", {"start": v(-803.45, -450.77) * mm, "mid": v(-803.38, -450.65) * mm, "end": v(-803.35, -450.5) * mm});
            skArc(sketch, "E1717", {"start": v(-798.46, -455.4) * mm, "mid": v(-798.6, -455.42) * mm, "end": v(-798.73, -455.5) * mm});
            skArc(sketch, "E1718", {"start": v(-803.45, -450.77) * mm, "mid": v(-803.35, -455.4) * mm, "end": v(-798.73, -455.5) * mm});
            skLineSegment(sketch, "E1719", {"start": v(-798.46, -455.4) * mm, "end": v(-794.74, -455.4) * mm});
            skArc(sketch, "E1720", {"start": v(-794.47, -455.5) * mm, "mid": v(-794.6, -455.42) * mm, "end": v(-794.74, -455.4) * mm});
            skArc(sketch, "E1721", {"start": v(-794.47, -455.5) * mm, "mid": v(-789.85, -455.4) * mm, "end": v(-789.75, -450.77) * mm});
            skArc(sketch, "E1722", {"start": v(-789.85, -450.5) * mm, "mid": v(-789.82, -450.65) * mm, "end": v(-789.75, -450.77) * mm});
            skLineSegment(sketch, "E1723", {"start": v(-789.85, -450.5) * mm, "end": v(-789.85, -447.25) * mm});
            skLineSegment(sketch, "E1724", {"start": v(-1178.94, -455.4) * mm, "end": v(-1182.66, -455.4) * mm});
            skArc(sketch, "E1725", {"start": v(-1178.67, -455.5) * mm, "mid": v(-1178.8, -455.42) * mm, "end": v(-1178.94, -455.4) * mm});
            skArc(sketch, "E1726", {"start": v(-1178.67, -455.5) * mm, "mid": v(-1174.05, -455.4) * mm, "end": v(-1173.95, -450.77) * mm});
            skArc(sketch, "E1727", {"start": v(-1174.05, -450.5) * mm, "mid": v(-1174.02, -450.65) * mm, "end": v(-1173.95, -450.77) * mm});
            skLineSegment(sketch, "E1728", {"start": v(-1174.05, -447.25) * mm, "end": v(-1174.05, -450.5) * mm});
            skArc(sketch, "E1729", {"start": v(-1173.95, -446.98) * mm, "mid": v(-1174.02, -447.1) * mm, "end": v(-1174.05, -447.25) * mm});
            skArc(sketch, "E1730", {"start": v(-1173.95, -446.98) * mm, "mid": v(-1174.05, -442.36) * mm, "end": v(-1178.67, -442.25) * mm});
            skArc(sketch, "E1731", {"start": v(-1178.94, -442.36) * mm, "mid": v(-1178.8, -442.33) * mm, "end": v(-1178.67, -442.25) * mm});
            skLineSegment(sketch, "E1732", {"start": v(-1182.66, -442.36) * mm, "end": v(-1178.94, -442.36) * mm});
            skArc(sketch, "E1733", {"start": v(-1182.93, -442.25) * mm, "mid": v(-1182.8, -442.33) * mm, "end": v(-1182.66, -442.36) * mm});
            skArc(sketch, "E1734", {"start": v(-1182.93, -442.25) * mm, "mid": v(-1187.55, -442.36) * mm, "end": v(-1187.65, -446.98) * mm});
            skArc(sketch, "E1735", {"start": v(-1187.55, -447.25) * mm, "mid": v(-1187.58, -447.1) * mm, "end": v(-1187.65, -446.98) * mm});
            skLineSegment(sketch, "E1736", {"start": v(-1187.55, -450.5) * mm, "end": v(-1187.55, -447.25) * mm});
            skArc(sketch, "E1737", {"start": v(-1187.65, -450.77) * mm, "mid": v(-1187.58, -450.65) * mm, "end": v(-1187.55, -450.5) * mm});
            skArc(sketch, "E1738", {"start": v(-1187.65, -450.77) * mm, "mid": v(-1187.55, -455.4) * mm, "end": v(-1182.93, -455.5) * mm});
            skSolve(sketch);
        }
        {
            var Q0;
            Q0 = qSketchRegion(id + "F0", true);
            extrude(context, id + "F1", {"entities" : qUnion([Q0]), "depth" : 35 * mm});
        }
    });
